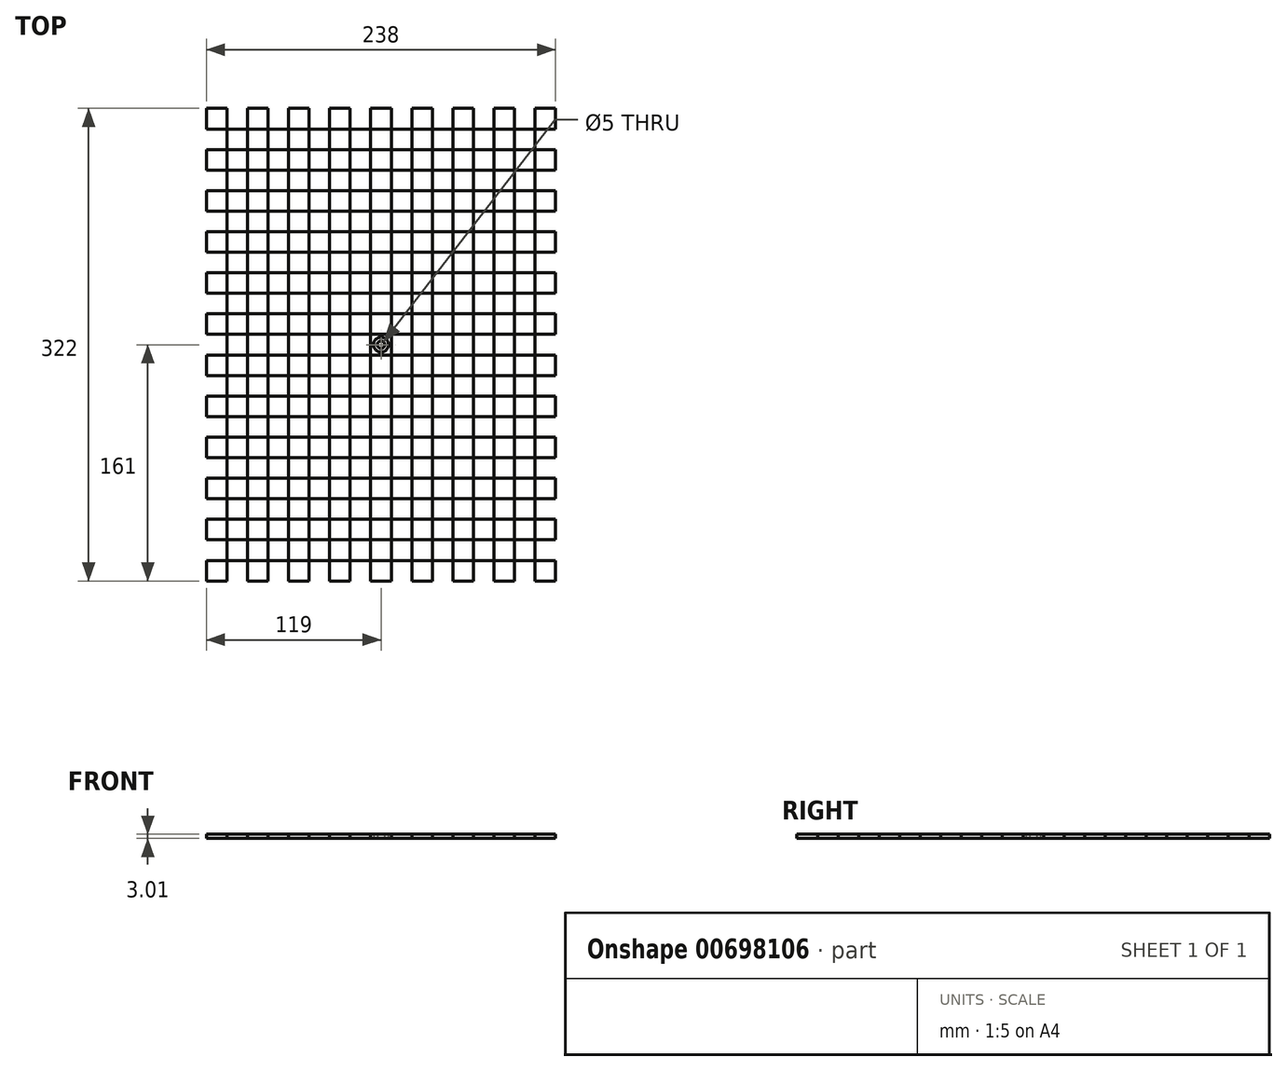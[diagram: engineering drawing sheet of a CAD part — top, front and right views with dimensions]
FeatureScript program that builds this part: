
annotation { "Feature Type Name" : "Feature", "Feature Type Description" : "" }
export const myFeature = defineFeature(function(context is Context, id is Id, definition is map)
    precondition{}
    {
        {
            var Q0;
            Q0=qCreatedBy(makeId("Top.planeOp"),FACE);
            var sketch = newSketch(context, id + "F0", { "sketchPlane" : qUnion([Q0])});
            skLineSegment(sketch, "E0.bottom", {"start": v(145.7, -177.6) * mm, "end": v(-139.3, -177.6) * mm});
            skLineSegment(sketch, "E0.top", {"start": v(145.7, 189.9) * mm, "end": v(-139.3, 189.9) * mm});
            skLineSegment(sketch, "E0.left", {"start": v(145.7, -177.6) * mm, "end": v(145.7, 189.9) * mm});
            skLineSegment(sketch, "E0.right", {"start": v(-139.3, -177.6) * mm, "end": v(-139.3, 189.9) * mm});
            skSolve(sketch);
        }
        {
            var Q0;
            Q0=qCreatedBy(makeId("Top.planeOp"),FACE);
            var sketch = newSketch(context, id + "F1", { "sketchPlane" : qUnion([Q0])});
            skLineSegment(sketch, "E1.bottom", {"start": v(-115.8, -155.6) * mm, "end": v(-101.8, -155.6) * mm});
            skLineSegment(sketch, "E1.top", {"start": v(-115.8, -141.6) * mm, "end": v(-101.8, -141.6) * mm});
            skLineSegment(sketch, "E1.left", {"start": v(-115.8, -155.6) * mm, "end": v(-115.8, -141.6) * mm});
            skLineSegment(sketch, "E1.right", {"start": v(-101.8, -155.6) * mm, "end": v(-101.8, -141.6) * mm});
            skLineSegment(sketch, "E2.direction1", {"start": v(-115.8, -155.6) * mm, "end": v(-87.8, -155.6) * mm, "construction": true});
            skLineSegment(sketch, "E2.direction2", {"start": v(-115.8, -155.6) * mm, "end": v(-115.8, -127.6) * mm, "construction": true});
            skLineSegment(sketch, "E3.bottom", {"start": v(94.2, -127.6) * mm, "end": v(108.2, -127.6) * mm});
            skLineSegment(sketch, "E3.top", {"start": v(94.2, -141.6) * mm, "end": v(108.2, -141.6) * mm});
            skLineSegment(sketch, "E3.left", {"start": v(94.2, -127.6) * mm, "end": v(94.2, -141.6) * mm});
            skLineSegment(sketch, "E3.right", {"start": v(108.2, -127.6) * mm, "end": v(108.2, -141.6) * mm});
            skLineSegment(sketch, "E4.direction1", {"start": v(94.2, -141.6) * mm, "end": v(66.2, -141.6) * mm, "construction": true});
            skLineSegment(sketch, "E4.direction2", {"start": v(94.2, -141.6) * mm, "end": v(94.2, -113.6) * mm, "construction": true});
            skLineSegment(sketch, "E5.0.1.0", {"start": v(-87.8, -155.6) * mm, "end": v(-73.8, -155.6) * mm});
            skLineSegment(sketch, "E5.3.1.0", {"start": v(-87.8, -141.6) * mm, "end": v(-73.8, -141.6) * mm});
            skLineSegment(sketch, "E5.6.1.0", {"start": v(-87.8, -155.6) * mm, "end": v(-87.8, -141.6) * mm});
            skLineSegment(sketch, "E5.9.1.0", {"start": v(-73.8, -155.6) * mm, "end": v(-73.8, -141.6) * mm});
            skLineSegment(sketch, "E5.0.2.0", {"start": v(-59.8, -155.6) * mm, "end": v(-45.8, -155.6) * mm});
            skLineSegment(sketch, "E5.3.2.0", {"start": v(-59.8, -141.6) * mm, "end": v(-45.8, -141.6) * mm});
            skLineSegment(sketch, "E5.6.2.0", {"start": v(-59.8, -155.6) * mm, "end": v(-59.8, -141.6) * mm});
            skLineSegment(sketch, "E5.9.2.0", {"start": v(-45.8, -155.6) * mm, "end": v(-45.8, -141.6) * mm});
            skLineSegment(sketch, "E5.0.3.0", {"start": v(-31.8, -155.6) * mm, "end": v(-17.8, -155.6) * mm});
            skLineSegment(sketch, "E5.3.3.0", {"start": v(-31.8, -141.6) * mm, "end": v(-17.8, -141.6) * mm});
            skLineSegment(sketch, "E5.6.3.0", {"start": v(-31.8, -155.6) * mm, "end": v(-31.8, -141.6) * mm});
            skLineSegment(sketch, "E5.9.3.0", {"start": v(-17.8, -155.6) * mm, "end": v(-17.8, -141.6) * mm});
            skLineSegment(sketch, "E5.0.4.0", {"start": v(-3.8, -155.6) * mm, "end": v(10.2, -155.6) * mm});
            skLineSegment(sketch, "E5.3.4.0", {"start": v(-3.8, -141.6) * mm, "end": v(10.2, -141.6) * mm});
            skLineSegment(sketch, "E5.6.4.0", {"start": v(-3.8, -155.6) * mm, "end": v(-3.8, -141.6) * mm});
            skLineSegment(sketch, "E5.9.4.0", {"start": v(10.2, -155.6) * mm, "end": v(10.2, -141.6) * mm});
            skLineSegment(sketch, "E5.0.5.0", {"start": v(24.2, -155.6) * mm, "end": v(38.2, -155.6) * mm});
            skLineSegment(sketch, "E5.3.5.0", {"start": v(24.2, -141.6) * mm, "end": v(38.2, -141.6) * mm});
            skLineSegment(sketch, "E5.6.5.0", {"start": v(24.2, -155.6) * mm, "end": v(24.2, -141.6) * mm});
            skLineSegment(sketch, "E5.9.5.0", {"start": v(38.2, -155.6) * mm, "end": v(38.2, -141.6) * mm});
            skLineSegment(sketch, "E5.0.6.0", {"start": v(52.2, -155.6) * mm, "end": v(66.2, -155.6) * mm});
            skLineSegment(sketch, "E5.3.6.0", {"start": v(52.2, -141.6) * mm, "end": v(66.2, -141.6) * mm});
            skLineSegment(sketch, "E5.6.6.0", {"start": v(52.2, -155.6) * mm, "end": v(52.2, -141.6) * mm});
            skLineSegment(sketch, "E5.9.6.0", {"start": v(66.2, -155.6) * mm, "end": v(66.2, -141.6) * mm});
            skLineSegment(sketch, "E5.0.7.0", {"start": v(80.2, -155.6) * mm, "end": v(94.2, -155.6) * mm});
            skLineSegment(sketch, "E5.3.7.0", {"start": v(80.2, -141.6) * mm, "end": v(94.2, -141.6) * mm});
            skLineSegment(sketch, "E5.6.7.0", {"start": v(80.2, -155.6) * mm, "end": v(80.2, -141.6) * mm});
            skLineSegment(sketch, "E5.9.7.0", {"start": v(94.2, -155.6) * mm, "end": v(94.2, -141.6) * mm});
            skLineSegment(sketch, "E5.0.8.0", {"start": v(108.2, -155.6) * mm, "end": v(122.2, -155.6) * mm});
            skLineSegment(sketch, "E5.3.8.0", {"start": v(108.2, -141.6) * mm, "end": v(122.2, -141.6) * mm});
            skLineSegment(sketch, "E5.6.8.0", {"start": v(108.2, -155.6) * mm, "end": v(108.2, -141.6) * mm});
            skLineSegment(sketch, "E5.9.8.0", {"start": v(122.2, -155.6) * mm, "end": v(122.2, -141.6) * mm});
            skLineSegment(sketch, "E6.0.0.1", {"start": v(-115.8, -127.6) * mm, "end": v(-101.8, -127.6) * mm});
            skLineSegment(sketch, "E6.3.0.1", {"start": v(-115.8, -113.6) * mm, "end": v(-101.8, -113.6) * mm});
            skLineSegment(sketch, "E6.6.0.1", {"start": v(-115.8, -127.6) * mm, "end": v(-115.8, -113.6) * mm});
            skLineSegment(sketch, "E6.9.0.1", {"start": v(-101.8, -127.6) * mm, "end": v(-101.8, -113.6) * mm});
            skLineSegment(sketch, "E6.0.0.2", {"start": v(-115.8, -99.6) * mm, "end": v(-101.8, -99.6) * mm});
            skLineSegment(sketch, "E6.3.0.2", {"start": v(-115.8, -85.6) * mm, "end": v(-101.8, -85.6) * mm});
            skLineSegment(sketch, "E6.6.0.2", {"start": v(-115.8, -99.6) * mm, "end": v(-115.8, -85.6) * mm});
            skLineSegment(sketch, "E6.9.0.2", {"start": v(-101.8, -99.6) * mm, "end": v(-101.8, -85.6) * mm});
            skLineSegment(sketch, "E6.0.0.3", {"start": v(-115.8, -71.6) * mm, "end": v(-101.8, -71.6) * mm});
            skLineSegment(sketch, "E6.3.0.3", {"start": v(-115.8, -57.6) * mm, "end": v(-101.8, -57.6) * mm});
            skLineSegment(sketch, "E6.6.0.3", {"start": v(-115.8, -71.6) * mm, "end": v(-115.8, -57.6) * mm});
            skLineSegment(sketch, "E6.9.0.3", {"start": v(-101.8, -71.6) * mm, "end": v(-101.8, -57.6) * mm});
            skLineSegment(sketch, "E6.0.0.4", {"start": v(-115.8, -43.6) * mm, "end": v(-101.8, -43.6) * mm});
            skLineSegment(sketch, "E6.3.0.4", {"start": v(-115.8, -29.6) * mm, "end": v(-101.8, -29.6) * mm});
            skLineSegment(sketch, "E6.6.0.4", {"start": v(-115.8, -43.6) * mm, "end": v(-115.8, -29.6) * mm});
            skLineSegment(sketch, "E6.9.0.4", {"start": v(-101.8, -43.6) * mm, "end": v(-101.8, -29.6) * mm});
            skLineSegment(sketch, "E6.0.0.5", {"start": v(-115.8, -15.6) * mm, "end": v(-101.8, -15.6) * mm});
            skLineSegment(sketch, "E6.3.0.5", {"start": v(-115.8, -1.6) * mm, "end": v(-101.8, -1.6) * mm});
            skLineSegment(sketch, "E6.6.0.5", {"start": v(-115.8, -15.6) * mm, "end": v(-115.8, -1.6) * mm});
            skLineSegment(sketch, "E6.9.0.5", {"start": v(-101.8, -15.6) * mm, "end": v(-101.8, -1.6) * mm});
            skLineSegment(sketch, "E6.0.0.6", {"start": v(-115.8, 12.4) * mm, "end": v(-101.8, 12.4) * mm});
            skLineSegment(sketch, "E6.3.0.6", {"start": v(-115.8, 26.4) * mm, "end": v(-101.8, 26.4) * mm});
            skLineSegment(sketch, "E6.6.0.6", {"start": v(-115.8, 12.4) * mm, "end": v(-115.8, 26.4) * mm});
            skLineSegment(sketch, "E6.9.0.6", {"start": v(-101.8, 12.4) * mm, "end": v(-101.8, 26.4) * mm});
            skLineSegment(sketch, "E6.0.0.7", {"start": v(-115.8, 40.4) * mm, "end": v(-101.8, 40.4) * mm});
            skLineSegment(sketch, "E6.3.0.7", {"start": v(-115.8, 54.4) * mm, "end": v(-101.8, 54.4) * mm});
            skLineSegment(sketch, "E6.6.0.7", {"start": v(-115.8, 40.4) * mm, "end": v(-115.8, 54.4) * mm});
            skLineSegment(sketch, "E6.9.0.7", {"start": v(-101.8, 40.4) * mm, "end": v(-101.8, 54.4) * mm});
            skLineSegment(sketch, "E6.0.0.8", {"start": v(-115.8, 68.4) * mm, "end": v(-101.8, 68.4) * mm});
            skLineSegment(sketch, "E6.3.0.8", {"start": v(-115.8, 82.4) * mm, "end": v(-101.8, 82.4) * mm});
            skLineSegment(sketch, "E6.6.0.8", {"start": v(-115.8, 68.4) * mm, "end": v(-115.8, 82.4) * mm});
            skLineSegment(sketch, "E6.9.0.8", {"start": v(-101.8, 68.4) * mm, "end": v(-101.8, 82.4) * mm});
            skLineSegment(sketch, "E6.0.0.9", {"start": v(-115.8, 96.4) * mm, "end": v(-101.8, 96.4) * mm});
            skLineSegment(sketch, "E6.3.0.9", {"start": v(-115.8, 110.4) * mm, "end": v(-101.8, 110.4) * mm});
            skLineSegment(sketch, "E6.6.0.9", {"start": v(-115.8, 96.4) * mm, "end": v(-115.8, 110.4) * mm});
            skLineSegment(sketch, "E6.9.0.9", {"start": v(-101.8, 96.4) * mm, "end": v(-101.8, 110.4) * mm});
            skLineSegment(sketch, "E6.0.0.10", {"start": v(-115.8, 124.4) * mm, "end": v(-101.8, 124.4) * mm});
            skLineSegment(sketch, "E6.3.0.10", {"start": v(-115.8, 138.4) * mm, "end": v(-101.8, 138.4) * mm});
            skLineSegment(sketch, "E6.6.0.10", {"start": v(-115.8, 124.4) * mm, "end": v(-115.8, 138.4) * mm});
            skLineSegment(sketch, "E6.9.0.10", {"start": v(-101.8, 124.4) * mm, "end": v(-101.8, 138.4) * mm});
            skLineSegment(sketch, "E6.0.0.11", {"start": v(-115.8, 152.4) * mm, "end": v(-101.8, 152.4) * mm});
            skLineSegment(sketch, "E6.3.0.11", {"start": v(-115.8, 166.4) * mm, "end": v(-101.8, 166.4) * mm});
            skLineSegment(sketch, "E6.6.0.11", {"start": v(-115.8, 152.4) * mm, "end": v(-115.8, 166.4) * mm});
            skLineSegment(sketch, "E6.9.0.11", {"start": v(-101.8, 152.4) * mm, "end": v(-101.8, 166.4) * mm});
            skLineSegment(sketch, "E6.0.1.1", {"start": v(-87.8, -127.6) * mm, "end": v(-73.8, -127.6) * mm});
            skLineSegment(sketch, "E6.3.1.1", {"start": v(-87.8, -113.6) * mm, "end": v(-73.8, -113.6) * mm});
            skLineSegment(sketch, "E6.6.1.1", {"start": v(-87.8, -127.6) * mm, "end": v(-87.8, -113.6) * mm});
            skLineSegment(sketch, "E6.9.1.1", {"start": v(-73.8, -127.6) * mm, "end": v(-73.8, -113.6) * mm});
            skLineSegment(sketch, "E6.0.1.2", {"start": v(-87.8, -99.6) * mm, "end": v(-73.8, -99.6) * mm});
            skLineSegment(sketch, "E6.3.1.2", {"start": v(-87.8, -85.6) * mm, "end": v(-73.8, -85.6) * mm});
            skLineSegment(sketch, "E6.6.1.2", {"start": v(-87.8, -99.6) * mm, "end": v(-87.8, -85.6) * mm});
            skLineSegment(sketch, "E6.9.1.2", {"start": v(-73.8, -99.6) * mm, "end": v(-73.8, -85.6) * mm});
            skLineSegment(sketch, "E6.0.1.3", {"start": v(-87.8, -71.6) * mm, "end": v(-73.8, -71.6) * mm});
            skLineSegment(sketch, "E6.3.1.3", {"start": v(-87.8, -57.6) * mm, "end": v(-73.8, -57.6) * mm});
            skLineSegment(sketch, "E6.6.1.3", {"start": v(-87.8, -71.6) * mm, "end": v(-87.8, -57.6) * mm});
            skLineSegment(sketch, "E6.9.1.3", {"start": v(-73.8, -71.6) * mm, "end": v(-73.8, -57.6) * mm});
            skLineSegment(sketch, "E6.0.1.4", {"start": v(-87.8, -43.6) * mm, "end": v(-73.8, -43.6) * mm});
            skLineSegment(sketch, "E6.3.1.4", {"start": v(-87.8, -29.6) * mm, "end": v(-73.8, -29.6) * mm});
            skLineSegment(sketch, "E6.6.1.4", {"start": v(-87.8, -43.6) * mm, "end": v(-87.8, -29.6) * mm});
            skLineSegment(sketch, "E6.9.1.4", {"start": v(-73.8, -43.6) * mm, "end": v(-73.8, -29.6) * mm});
            skLineSegment(sketch, "E6.0.1.5", {"start": v(-87.8, -15.6) * mm, "end": v(-73.8, -15.6) * mm});
            skLineSegment(sketch, "E6.3.1.5", {"start": v(-87.8, -1.6) * mm, "end": v(-73.8, -1.6) * mm});
            skLineSegment(sketch, "E6.6.1.5", {"start": v(-87.8, -15.6) * mm, "end": v(-87.8, -1.6) * mm});
            skLineSegment(sketch, "E6.9.1.5", {"start": v(-73.8, -15.6) * mm, "end": v(-73.8, -1.6) * mm});
            skLineSegment(sketch, "E6.0.1.6", {"start": v(-87.8, 12.4) * mm, "end": v(-73.8, 12.4) * mm});
            skLineSegment(sketch, "E6.3.1.6", {"start": v(-87.8, 26.4) * mm, "end": v(-73.8, 26.4) * mm});
            skLineSegment(sketch, "E6.6.1.6", {"start": v(-87.8, 12.4) * mm, "end": v(-87.8, 26.4) * mm});
            skLineSegment(sketch, "E6.9.1.6", {"start": v(-73.8, 12.4) * mm, "end": v(-73.8, 26.4) * mm});
            skLineSegment(sketch, "E6.0.1.7", {"start": v(-87.8, 40.4) * mm, "end": v(-73.8, 40.4) * mm});
            skLineSegment(sketch, "E6.3.1.7", {"start": v(-87.8, 54.4) * mm, "end": v(-73.8, 54.4) * mm});
            skLineSegment(sketch, "E6.6.1.7", {"start": v(-87.8, 40.4) * mm, "end": v(-87.8, 54.4) * mm});
            skLineSegment(sketch, "E6.9.1.7", {"start": v(-73.8, 40.4) * mm, "end": v(-73.8, 54.4) * mm});
            skLineSegment(sketch, "E6.0.1.8", {"start": v(-87.8, 68.4) * mm, "end": v(-73.8, 68.4) * mm});
            skLineSegment(sketch, "E6.3.1.8", {"start": v(-87.8, 82.4) * mm, "end": v(-73.8, 82.4) * mm});
            skLineSegment(sketch, "E6.6.1.8", {"start": v(-87.8, 68.4) * mm, "end": v(-87.8, 82.4) * mm});
            skLineSegment(sketch, "E6.9.1.8", {"start": v(-73.8, 68.4) * mm, "end": v(-73.8, 82.4) * mm});
            skLineSegment(sketch, "E6.0.1.9", {"start": v(-87.8, 96.4) * mm, "end": v(-73.8, 96.4) * mm});
            skLineSegment(sketch, "E6.3.1.9", {"start": v(-87.8, 110.4) * mm, "end": v(-73.8, 110.4) * mm});
            skLineSegment(sketch, "E6.6.1.9", {"start": v(-87.8, 96.4) * mm, "end": v(-87.8, 110.4) * mm});
            skLineSegment(sketch, "E6.9.1.9", {"start": v(-73.8, 96.4) * mm, "end": v(-73.8, 110.4) * mm});
            skLineSegment(sketch, "E6.0.1.10", {"start": v(-87.8, 124.4) * mm, "end": v(-73.8, 124.4) * mm});
            skLineSegment(sketch, "E6.3.1.10", {"start": v(-87.8, 138.4) * mm, "end": v(-73.8, 138.4) * mm});
            skLineSegment(sketch, "E6.6.1.10", {"start": v(-87.8, 124.4) * mm, "end": v(-87.8, 138.4) * mm});
            skLineSegment(sketch, "E6.9.1.10", {"start": v(-73.8, 124.4) * mm, "end": v(-73.8, 138.4) * mm});
            skLineSegment(sketch, "E6.0.1.11", {"start": v(-87.8, 152.4) * mm, "end": v(-73.8, 152.4) * mm});
            skLineSegment(sketch, "E6.3.1.11", {"start": v(-87.8, 166.4) * mm, "end": v(-73.8, 166.4) * mm});
            skLineSegment(sketch, "E6.6.1.11", {"start": v(-87.8, 152.4) * mm, "end": v(-87.8, 166.4) * mm});
            skLineSegment(sketch, "E6.9.1.11", {"start": v(-73.8, 152.4) * mm, "end": v(-73.8, 166.4) * mm});
            skLineSegment(sketch, "E6.0.2.1", {"start": v(-59.8, -127.6) * mm, "end": v(-45.8, -127.6) * mm});
            skLineSegment(sketch, "E6.3.2.1", {"start": v(-59.8, -113.6) * mm, "end": v(-45.8, -113.6) * mm});
            skLineSegment(sketch, "E6.6.2.1", {"start": v(-59.8, -127.6) * mm, "end": v(-59.8, -113.6) * mm});
            skLineSegment(sketch, "E6.9.2.1", {"start": v(-45.8, -127.6) * mm, "end": v(-45.8, -113.6) * mm});
            skLineSegment(sketch, "E6.0.2.2", {"start": v(-59.8, -99.6) * mm, "end": v(-45.8, -99.6) * mm});
            skLineSegment(sketch, "E6.3.2.2", {"start": v(-59.8, -85.6) * mm, "end": v(-45.8, -85.6) * mm});
            skLineSegment(sketch, "E6.6.2.2", {"start": v(-59.8, -99.6) * mm, "end": v(-59.8, -85.6) * mm});
            skLineSegment(sketch, "E6.9.2.2", {"start": v(-45.8, -99.6) * mm, "end": v(-45.8, -85.6) * mm});
            skLineSegment(sketch, "E6.0.2.3", {"start": v(-59.8, -71.6) * mm, "end": v(-45.8, -71.6) * mm});
            skLineSegment(sketch, "E6.3.2.3", {"start": v(-59.8, -57.6) * mm, "end": v(-45.8, -57.6) * mm});
            skLineSegment(sketch, "E6.6.2.3", {"start": v(-59.8, -71.6) * mm, "end": v(-59.8, -57.6) * mm});
            skLineSegment(sketch, "E6.9.2.3", {"start": v(-45.8, -71.6) * mm, "end": v(-45.8, -57.6) * mm});
            skLineSegment(sketch, "E6.0.2.4", {"start": v(-59.8, -43.6) * mm, "end": v(-45.8, -43.6) * mm});
            skLineSegment(sketch, "E6.3.2.4", {"start": v(-59.8, -29.6) * mm, "end": v(-45.8, -29.6) * mm});
            skLineSegment(sketch, "E6.6.2.4", {"start": v(-59.8, -43.6) * mm, "end": v(-59.8, -29.6) * mm});
            skLineSegment(sketch, "E6.9.2.4", {"start": v(-45.8, -43.6) * mm, "end": v(-45.8, -29.6) * mm});
            skLineSegment(sketch, "E6.0.2.5", {"start": v(-59.8, -15.6) * mm, "end": v(-45.8, -15.6) * mm});
            skLineSegment(sketch, "E6.3.2.5", {"start": v(-59.8, -1.6) * mm, "end": v(-45.8, -1.6) * mm});
            skLineSegment(sketch, "E6.6.2.5", {"start": v(-59.8, -15.6) * mm, "end": v(-59.8, -1.6) * mm});
            skLineSegment(sketch, "E6.9.2.5", {"start": v(-45.8, -15.6) * mm, "end": v(-45.8, -1.6) * mm});
            skLineSegment(sketch, "E6.0.2.6", {"start": v(-59.8, 12.4) * mm, "end": v(-45.8, 12.4) * mm});
            skLineSegment(sketch, "E6.3.2.6", {"start": v(-59.8, 26.4) * mm, "end": v(-45.8, 26.4) * mm});
            skLineSegment(sketch, "E6.6.2.6", {"start": v(-59.8, 12.4) * mm, "end": v(-59.8, 26.4) * mm});
            skLineSegment(sketch, "E6.9.2.6", {"start": v(-45.8, 12.4) * mm, "end": v(-45.8, 26.4) * mm});
            skLineSegment(sketch, "E6.0.2.7", {"start": v(-59.8, 40.4) * mm, "end": v(-45.8, 40.4) * mm});
            skLineSegment(sketch, "E6.3.2.7", {"start": v(-59.8, 54.4) * mm, "end": v(-45.8, 54.4) * mm});
            skLineSegment(sketch, "E6.6.2.7", {"start": v(-59.8, 40.4) * mm, "end": v(-59.8, 54.4) * mm});
            skLineSegment(sketch, "E6.9.2.7", {"start": v(-45.8, 40.4) * mm, "end": v(-45.8, 54.4) * mm});
            skLineSegment(sketch, "E6.0.2.8", {"start": v(-59.8, 68.4) * mm, "end": v(-45.8, 68.4) * mm});
            skLineSegment(sketch, "E6.3.2.8", {"start": v(-59.8, 82.4) * mm, "end": v(-45.8, 82.4) * mm});
            skLineSegment(sketch, "E6.6.2.8", {"start": v(-59.8, 68.4) * mm, "end": v(-59.8, 82.4) * mm});
            skLineSegment(sketch, "E6.9.2.8", {"start": v(-45.8, 68.4) * mm, "end": v(-45.8, 82.4) * mm});
            skLineSegment(sketch, "E6.0.2.9", {"start": v(-59.8, 96.4) * mm, "end": v(-45.8, 96.4) * mm});
            skLineSegment(sketch, "E6.3.2.9", {"start": v(-59.8, 110.4) * mm, "end": v(-45.8, 110.4) * mm});
            skLineSegment(sketch, "E6.6.2.9", {"start": v(-59.8, 96.4) * mm, "end": v(-59.8, 110.4) * mm});
            skLineSegment(sketch, "E6.9.2.9", {"start": v(-45.8, 96.4) * mm, "end": v(-45.8, 110.4) * mm});
            skLineSegment(sketch, "E6.0.2.10", {"start": v(-59.8, 124.4) * mm, "end": v(-45.8, 124.4) * mm});
            skLineSegment(sketch, "E6.3.2.10", {"start": v(-59.8, 138.4) * mm, "end": v(-45.8, 138.4) * mm});
            skLineSegment(sketch, "E6.6.2.10", {"start": v(-59.8, 124.4) * mm, "end": v(-59.8, 138.4) * mm});
            skLineSegment(sketch, "E6.9.2.10", {"start": v(-45.8, 124.4) * mm, "end": v(-45.8, 138.4) * mm});
            skLineSegment(sketch, "E6.0.2.11", {"start": v(-59.8, 152.4) * mm, "end": v(-45.8, 152.4) * mm});
            skLineSegment(sketch, "E6.3.2.11", {"start": v(-59.8, 166.4) * mm, "end": v(-45.8, 166.4) * mm});
            skLineSegment(sketch, "E6.6.2.11", {"start": v(-59.8, 152.4) * mm, "end": v(-59.8, 166.4) * mm});
            skLineSegment(sketch, "E6.9.2.11", {"start": v(-45.8, 152.4) * mm, "end": v(-45.8, 166.4) * mm});
            skLineSegment(sketch, "E6.0.3.1", {"start": v(-31.8, -127.6) * mm, "end": v(-17.8, -127.6) * mm});
            skLineSegment(sketch, "E6.3.3.1", {"start": v(-31.8, -113.6) * mm, "end": v(-17.8, -113.6) * mm});
            skLineSegment(sketch, "E6.6.3.1", {"start": v(-31.8, -127.6) * mm, "end": v(-31.8, -113.6) * mm});
            skLineSegment(sketch, "E6.9.3.1", {"start": v(-17.8, -127.6) * mm, "end": v(-17.8, -113.6) * mm});
            skLineSegment(sketch, "E6.0.3.2", {"start": v(-31.8, -99.6) * mm, "end": v(-17.8, -99.6) * mm});
            skLineSegment(sketch, "E6.3.3.2", {"start": v(-31.8, -85.6) * mm, "end": v(-17.8, -85.6) * mm});
            skLineSegment(sketch, "E6.6.3.2", {"start": v(-31.8, -99.6) * mm, "end": v(-31.8, -85.6) * mm});
            skLineSegment(sketch, "E6.9.3.2", {"start": v(-17.8, -99.6) * mm, "end": v(-17.8, -85.6) * mm});
            skLineSegment(sketch, "E6.0.3.3", {"start": v(-31.8, -71.6) * mm, "end": v(-17.8, -71.6) * mm});
            skLineSegment(sketch, "E6.3.3.3", {"start": v(-31.8, -57.6) * mm, "end": v(-17.8, -57.6) * mm});
            skLineSegment(sketch, "E6.6.3.3", {"start": v(-31.8, -71.6) * mm, "end": v(-31.8, -57.6) * mm});
            skLineSegment(sketch, "E6.9.3.3", {"start": v(-17.8, -71.6) * mm, "end": v(-17.8, -57.6) * mm});
            skLineSegment(sketch, "E6.0.3.4", {"start": v(-31.8, -43.6) * mm, "end": v(-17.8, -43.6) * mm});
            skLineSegment(sketch, "E6.3.3.4", {"start": v(-31.8, -29.6) * mm, "end": v(-17.8, -29.6) * mm});
            skLineSegment(sketch, "E6.6.3.4", {"start": v(-31.8, -43.6) * mm, "end": v(-31.8, -29.6) * mm});
            skLineSegment(sketch, "E6.9.3.4", {"start": v(-17.8, -43.6) * mm, "end": v(-17.8, -29.6) * mm});
            skLineSegment(sketch, "E6.0.3.5", {"start": v(-31.8, -15.6) * mm, "end": v(-17.8, -15.6) * mm});
            skLineSegment(sketch, "E6.3.3.5", {"start": v(-31.8, -1.6) * mm, "end": v(-17.8, -1.6) * mm});
            skLineSegment(sketch, "E6.6.3.5", {"start": v(-31.8, -15.6) * mm, "end": v(-31.8, -1.6) * mm});
            skLineSegment(sketch, "E6.9.3.5", {"start": v(-17.8, -15.6) * mm, "end": v(-17.8, -1.6) * mm});
            skLineSegment(sketch, "E6.0.3.6", {"start": v(-31.8, 12.4) * mm, "end": v(-17.8, 12.4) * mm});
            skLineSegment(sketch, "E6.3.3.6", {"start": v(-31.8, 26.4) * mm, "end": v(-17.8, 26.4) * mm});
            skLineSegment(sketch, "E6.6.3.6", {"start": v(-31.8, 12.4) * mm, "end": v(-31.8, 26.4) * mm});
            skLineSegment(sketch, "E6.9.3.6", {"start": v(-17.8, 12.4) * mm, "end": v(-17.8, 26.4) * mm});
            skLineSegment(sketch, "E6.0.3.7", {"start": v(-31.8, 40.4) * mm, "end": v(-17.8, 40.4) * mm});
            skLineSegment(sketch, "E6.3.3.7", {"start": v(-31.8, 54.4) * mm, "end": v(-17.8, 54.4) * mm});
            skLineSegment(sketch, "E6.6.3.7", {"start": v(-31.8, 40.4) * mm, "end": v(-31.8, 54.4) * mm});
            skLineSegment(sketch, "E6.9.3.7", {"start": v(-17.8, 40.4) * mm, "end": v(-17.8, 54.4) * mm});
            skLineSegment(sketch, "E6.0.3.8", {"start": v(-31.8, 68.4) * mm, "end": v(-17.8, 68.4) * mm});
            skLineSegment(sketch, "E6.3.3.8", {"start": v(-31.8, 82.4) * mm, "end": v(-17.8, 82.4) * mm});
            skLineSegment(sketch, "E6.6.3.8", {"start": v(-31.8, 68.4) * mm, "end": v(-31.8, 82.4) * mm});
            skLineSegment(sketch, "E6.9.3.8", {"start": v(-17.8, 68.4) * mm, "end": v(-17.8, 82.4) * mm});
            skLineSegment(sketch, "E6.0.3.9", {"start": v(-31.8, 96.4) * mm, "end": v(-17.8, 96.4) * mm});
            skLineSegment(sketch, "E6.3.3.9", {"start": v(-31.8, 110.4) * mm, "end": v(-17.8, 110.4) * mm});
            skLineSegment(sketch, "E6.6.3.9", {"start": v(-31.8, 96.4) * mm, "end": v(-31.8, 110.4) * mm});
            skLineSegment(sketch, "E6.9.3.9", {"start": v(-17.8, 96.4) * mm, "end": v(-17.8, 110.4) * mm});
            skLineSegment(sketch, "E6.0.3.10", {"start": v(-31.8, 124.4) * mm, "end": v(-17.8, 124.4) * mm});
            skLineSegment(sketch, "E6.3.3.10", {"start": v(-31.8, 138.4) * mm, "end": v(-17.8, 138.4) * mm});
            skLineSegment(sketch, "E6.6.3.10", {"start": v(-31.8, 124.4) * mm, "end": v(-31.8, 138.4) * mm});
            skLineSegment(sketch, "E6.9.3.10", {"start": v(-17.8, 124.4) * mm, "end": v(-17.8, 138.4) * mm});
            skLineSegment(sketch, "E6.0.3.11", {"start": v(-31.8, 152.4) * mm, "end": v(-17.8, 152.4) * mm});
            skLineSegment(sketch, "E6.3.3.11", {"start": v(-31.8, 166.4) * mm, "end": v(-17.8, 166.4) * mm});
            skLineSegment(sketch, "E6.6.3.11", {"start": v(-31.8, 152.4) * mm, "end": v(-31.8, 166.4) * mm});
            skLineSegment(sketch, "E6.9.3.11", {"start": v(-17.8, 152.4) * mm, "end": v(-17.8, 166.4) * mm});
            skLineSegment(sketch, "E6.0.4.1", {"start": v(-3.8, -127.6) * mm, "end": v(10.2, -127.6) * mm});
            skLineSegment(sketch, "E6.3.4.1", {"start": v(-3.8, -113.6) * mm, "end": v(10.2, -113.6) * mm});
            skLineSegment(sketch, "E6.6.4.1", {"start": v(-3.8, -127.6) * mm, "end": v(-3.8, -113.6) * mm});
            skLineSegment(sketch, "E6.9.4.1", {"start": v(10.2, -127.6) * mm, "end": v(10.2, -113.6) * mm});
            skLineSegment(sketch, "E6.0.4.2", {"start": v(-3.8, -99.6) * mm, "end": v(10.2, -99.6) * mm});
            skLineSegment(sketch, "E6.3.4.2", {"start": v(-3.8, -85.6) * mm, "end": v(10.2, -85.6) * mm});
            skLineSegment(sketch, "E6.6.4.2", {"start": v(-3.8, -99.6) * mm, "end": v(-3.8, -85.6) * mm});
            skLineSegment(sketch, "E6.9.4.2", {"start": v(10.2, -99.6) * mm, "end": v(10.2, -85.6) * mm});
            skLineSegment(sketch, "E6.0.4.3", {"start": v(-3.8, -71.6) * mm, "end": v(10.2, -71.6) * mm});
            skLineSegment(sketch, "E6.3.4.3", {"start": v(-3.8, -57.6) * mm, "end": v(10.2, -57.6) * mm});
            skLineSegment(sketch, "E6.6.4.3", {"start": v(-3.8, -71.6) * mm, "end": v(-3.8, -57.6) * mm});
            skLineSegment(sketch, "E6.9.4.3", {"start": v(10.2, -71.6) * mm, "end": v(10.2, -57.6) * mm});
            skLineSegment(sketch, "E6.0.4.4", {"start": v(-3.8, -43.6) * mm, "end": v(10.2, -43.6) * mm});
            skLineSegment(sketch, "E6.3.4.4", {"start": v(-3.8, -29.6) * mm, "end": v(10.2, -29.6) * mm});
            skLineSegment(sketch, "E6.6.4.4", {"start": v(-3.8, -43.6) * mm, "end": v(-3.8, -29.6) * mm});
            skLineSegment(sketch, "E6.9.4.4", {"start": v(10.2, -43.6) * mm, "end": v(10.2, -29.6) * mm});
            skLineSegment(sketch, "E6.0.4.5", {"start": v(-3.8, -15.6) * mm, "end": v(10.2, -15.6) * mm});
            skLineSegment(sketch, "E6.3.4.5", {"start": v(-3.8, -1.6) * mm, "end": v(10.2, -1.6) * mm});
            skLineSegment(sketch, "E6.6.4.5", {"start": v(-3.8, -15.6) * mm, "end": v(-3.8, -1.6) * mm});
            skLineSegment(sketch, "E6.9.4.5", {"start": v(10.2, -15.6) * mm, "end": v(10.2, -1.6) * mm});
            skLineSegment(sketch, "E6.0.4.6", {"start": v(-3.8, 12.4) * mm, "end": v(10.2, 12.4) * mm});
            skLineSegment(sketch, "E6.3.4.6", {"start": v(-3.8, 26.4) * mm, "end": v(10.2, 26.4) * mm});
            skLineSegment(sketch, "E6.6.4.6", {"start": v(-3.8, 12.4) * mm, "end": v(-3.8, 26.4) * mm});
            skLineSegment(sketch, "E6.9.4.6", {"start": v(10.2, 12.4) * mm, "end": v(10.2, 26.4) * mm});
            skLineSegment(sketch, "E6.0.4.7", {"start": v(-3.8, 40.4) * mm, "end": v(10.2, 40.4) * mm});
            skLineSegment(sketch, "E6.3.4.7", {"start": v(-3.8, 54.4) * mm, "end": v(10.2, 54.4) * mm});
            skLineSegment(sketch, "E6.6.4.7", {"start": v(-3.8, 40.4) * mm, "end": v(-3.8, 54.4) * mm});
            skLineSegment(sketch, "E6.9.4.7", {"start": v(10.2, 40.4) * mm, "end": v(10.2, 54.4) * mm});
            skLineSegment(sketch, "E6.0.4.8", {"start": v(-3.8, 68.4) * mm, "end": v(10.2, 68.4) * mm});
            skLineSegment(sketch, "E6.3.4.8", {"start": v(-3.8, 82.4) * mm, "end": v(10.2, 82.4) * mm});
            skLineSegment(sketch, "E6.6.4.8", {"start": v(-3.8, 68.4) * mm, "end": v(-3.8, 82.4) * mm});
            skLineSegment(sketch, "E6.9.4.8", {"start": v(10.2, 68.4) * mm, "end": v(10.2, 82.4) * mm});
            skLineSegment(sketch, "E6.0.4.9", {"start": v(-3.8, 96.4) * mm, "end": v(10.2, 96.4) * mm});
            skLineSegment(sketch, "E6.3.4.9", {"start": v(-3.8, 110.4) * mm, "end": v(10.2, 110.4) * mm});
            skLineSegment(sketch, "E6.6.4.9", {"start": v(-3.8, 96.4) * mm, "end": v(-3.8, 110.4) * mm});
            skLineSegment(sketch, "E6.9.4.9", {"start": v(10.2, 96.4) * mm, "end": v(10.2, 110.4) * mm});
            skLineSegment(sketch, "E6.0.4.10", {"start": v(-3.8, 124.4) * mm, "end": v(10.2, 124.4) * mm});
            skLineSegment(sketch, "E6.3.4.10", {"start": v(-3.8, 138.4) * mm, "end": v(10.2, 138.4) * mm});
            skLineSegment(sketch, "E6.6.4.10", {"start": v(-3.8, 124.4) * mm, "end": v(-3.8, 138.4) * mm});
            skLineSegment(sketch, "E6.9.4.10", {"start": v(10.2, 124.4) * mm, "end": v(10.2, 138.4) * mm});
            skLineSegment(sketch, "E6.0.4.11", {"start": v(-3.8, 152.4) * mm, "end": v(10.2, 152.4) * mm});
            skLineSegment(sketch, "E6.3.4.11", {"start": v(-3.8, 166.4) * mm, "end": v(10.2, 166.4) * mm});
            skLineSegment(sketch, "E6.6.4.11", {"start": v(-3.8, 152.4) * mm, "end": v(-3.8, 166.4) * mm});
            skLineSegment(sketch, "E6.9.4.11", {"start": v(10.2, 152.4) * mm, "end": v(10.2, 166.4) * mm});
            skLineSegment(sketch, "E6.0.5.1", {"start": v(24.2, -127.6) * mm, "end": v(38.2, -127.6) * mm});
            skLineSegment(sketch, "E6.3.5.1", {"start": v(24.2, -113.6) * mm, "end": v(38.2, -113.6) * mm});
            skLineSegment(sketch, "E6.6.5.1", {"start": v(24.2, -127.6) * mm, "end": v(24.2, -113.6) * mm});
            skLineSegment(sketch, "E6.9.5.1", {"start": v(38.2, -127.6) * mm, "end": v(38.2, -113.6) * mm});
            skLineSegment(sketch, "E6.0.5.2", {"start": v(24.2, -99.6) * mm, "end": v(38.2, -99.6) * mm});
            skLineSegment(sketch, "E6.3.5.2", {"start": v(24.2, -85.6) * mm, "end": v(38.2, -85.6) * mm});
            skLineSegment(sketch, "E6.6.5.2", {"start": v(24.2, -99.6) * mm, "end": v(24.2, -85.6) * mm});
            skLineSegment(sketch, "E6.9.5.2", {"start": v(38.2, -99.6) * mm, "end": v(38.2, -85.6) * mm});
            skLineSegment(sketch, "E6.0.5.3", {"start": v(24.2, -71.6) * mm, "end": v(38.2, -71.6) * mm});
            skLineSegment(sketch, "E6.3.5.3", {"start": v(24.2, -57.6) * mm, "end": v(38.2, -57.6) * mm});
            skLineSegment(sketch, "E6.6.5.3", {"start": v(24.2, -71.6) * mm, "end": v(24.2, -57.6) * mm});
            skLineSegment(sketch, "E6.9.5.3", {"start": v(38.2, -71.6) * mm, "end": v(38.2, -57.6) * mm});
            skLineSegment(sketch, "E6.0.5.4", {"start": v(24.2, -43.6) * mm, "end": v(38.2, -43.6) * mm});
            skLineSegment(sketch, "E6.3.5.4", {"start": v(24.2, -29.6) * mm, "end": v(38.2, -29.6) * mm});
            skLineSegment(sketch, "E6.6.5.4", {"start": v(24.2, -43.6) * mm, "end": v(24.2, -29.6) * mm});
            skLineSegment(sketch, "E6.9.5.4", {"start": v(38.2, -43.6) * mm, "end": v(38.2, -29.6) * mm});
            skLineSegment(sketch, "E6.0.5.5", {"start": v(24.2, -15.6) * mm, "end": v(38.2, -15.6) * mm});
            skLineSegment(sketch, "E6.3.5.5", {"start": v(24.2, -1.6) * mm, "end": v(38.2, -1.6) * mm});
            skLineSegment(sketch, "E6.6.5.5", {"start": v(24.2, -15.6) * mm, "end": v(24.2, -1.6) * mm});
            skLineSegment(sketch, "E6.9.5.5", {"start": v(38.2, -15.6) * mm, "end": v(38.2, -1.6) * mm});
            skLineSegment(sketch, "E6.0.5.6", {"start": v(24.2, 12.4) * mm, "end": v(38.2, 12.4) * mm});
            skLineSegment(sketch, "E6.3.5.6", {"start": v(24.2, 26.4) * mm, "end": v(38.2, 26.4) * mm});
            skLineSegment(sketch, "E6.6.5.6", {"start": v(24.2, 12.4) * mm, "end": v(24.2, 26.4) * mm});
            skLineSegment(sketch, "E6.9.5.6", {"start": v(38.2, 12.4) * mm, "end": v(38.2, 26.4) * mm});
            skLineSegment(sketch, "E6.0.5.7", {"start": v(24.2, 40.4) * mm, "end": v(38.2, 40.4) * mm});
            skLineSegment(sketch, "E6.3.5.7", {"start": v(24.2, 54.4) * mm, "end": v(38.2, 54.4) * mm});
            skLineSegment(sketch, "E6.6.5.7", {"start": v(24.2, 40.4) * mm, "end": v(24.2, 54.4) * mm});
            skLineSegment(sketch, "E6.9.5.7", {"start": v(38.2, 40.4) * mm, "end": v(38.2, 54.4) * mm});
            skLineSegment(sketch, "E6.0.5.8", {"start": v(24.2, 68.4) * mm, "end": v(38.2, 68.4) * mm});
            skLineSegment(sketch, "E6.3.5.8", {"start": v(24.2, 82.4) * mm, "end": v(38.2, 82.4) * mm});
            skLineSegment(sketch, "E6.6.5.8", {"start": v(24.2, 68.4) * mm, "end": v(24.2, 82.4) * mm});
            skLineSegment(sketch, "E6.9.5.8", {"start": v(38.2, 68.4) * mm, "end": v(38.2, 82.4) * mm});
            skLineSegment(sketch, "E6.0.5.9", {"start": v(24.2, 96.4) * mm, "end": v(38.2, 96.4) * mm});
            skLineSegment(sketch, "E6.3.5.9", {"start": v(24.2, 110.4) * mm, "end": v(38.2, 110.4) * mm});
            skLineSegment(sketch, "E6.6.5.9", {"start": v(24.2, 96.4) * mm, "end": v(24.2, 110.4) * mm});
            skLineSegment(sketch, "E6.9.5.9", {"start": v(38.2, 96.4) * mm, "end": v(38.2, 110.4) * mm});
            skLineSegment(sketch, "E6.0.5.10", {"start": v(24.2, 124.4) * mm, "end": v(38.2, 124.4) * mm});
            skLineSegment(sketch, "E6.3.5.10", {"start": v(24.2, 138.4) * mm, "end": v(38.2, 138.4) * mm});
            skLineSegment(sketch, "E6.6.5.10", {"start": v(24.2, 124.4) * mm, "end": v(24.2, 138.4) * mm});
            skLineSegment(sketch, "E6.9.5.10", {"start": v(38.2, 124.4) * mm, "end": v(38.2, 138.4) * mm});
            skLineSegment(sketch, "E6.0.5.11", {"start": v(24.2, 152.4) * mm, "end": v(38.2, 152.4) * mm});
            skLineSegment(sketch, "E6.3.5.11", {"start": v(24.2, 166.4) * mm, "end": v(38.2, 166.4) * mm});
            skLineSegment(sketch, "E6.6.5.11", {"start": v(24.2, 152.4) * mm, "end": v(24.2, 166.4) * mm});
            skLineSegment(sketch, "E6.9.5.11", {"start": v(38.2, 152.4) * mm, "end": v(38.2, 166.4) * mm});
            skLineSegment(sketch, "E6.0.6.1", {"start": v(52.2, -127.6) * mm, "end": v(66.2, -127.6) * mm});
            skLineSegment(sketch, "E6.3.6.1", {"start": v(52.2, -113.6) * mm, "end": v(66.2, -113.6) * mm});
            skLineSegment(sketch, "E6.6.6.1", {"start": v(52.2, -127.6) * mm, "end": v(52.2, -113.6) * mm});
            skLineSegment(sketch, "E6.9.6.1", {"start": v(66.2, -127.6) * mm, "end": v(66.2, -113.6) * mm});
            skLineSegment(sketch, "E6.0.6.2", {"start": v(52.2, -99.6) * mm, "end": v(66.2, -99.6) * mm});
            skLineSegment(sketch, "E6.3.6.2", {"start": v(52.2, -85.6) * mm, "end": v(66.2, -85.6) * mm});
            skLineSegment(sketch, "E6.6.6.2", {"start": v(52.2, -99.6) * mm, "end": v(52.2, -85.6) * mm});
            skLineSegment(sketch, "E6.9.6.2", {"start": v(66.2, -99.6) * mm, "end": v(66.2, -85.6) * mm});
            skLineSegment(sketch, "E6.0.6.3", {"start": v(52.2, -71.6) * mm, "end": v(66.2, -71.6) * mm});
            skLineSegment(sketch, "E6.3.6.3", {"start": v(52.2, -57.6) * mm, "end": v(66.2, -57.6) * mm});
            skLineSegment(sketch, "E6.6.6.3", {"start": v(52.2, -71.6) * mm, "end": v(52.2, -57.6) * mm});
            skLineSegment(sketch, "E6.9.6.3", {"start": v(66.2, -71.6) * mm, "end": v(66.2, -57.6) * mm});
            skLineSegment(sketch, "E6.0.6.4", {"start": v(52.2, -43.6) * mm, "end": v(66.2, -43.6) * mm});
            skLineSegment(sketch, "E6.3.6.4", {"start": v(52.2, -29.6) * mm, "end": v(66.2, -29.6) * mm});
            skLineSegment(sketch, "E6.6.6.4", {"start": v(52.2, -43.6) * mm, "end": v(52.2, -29.6) * mm});
            skLineSegment(sketch, "E6.9.6.4", {"start": v(66.2, -43.6) * mm, "end": v(66.2, -29.6) * mm});
            skLineSegment(sketch, "E6.0.6.5", {"start": v(52.2, -15.6) * mm, "end": v(66.2, -15.6) * mm});
            skLineSegment(sketch, "E6.3.6.5", {"start": v(52.2, -1.6) * mm, "end": v(66.2, -1.6) * mm});
            skLineSegment(sketch, "E6.6.6.5", {"start": v(52.2, -15.6) * mm, "end": v(52.2, -1.6) * mm});
            skLineSegment(sketch, "E6.9.6.5", {"start": v(66.2, -15.6) * mm, "end": v(66.2, -1.6) * mm});
            skLineSegment(sketch, "E6.0.6.6", {"start": v(52.2, 12.4) * mm, "end": v(66.2, 12.4) * mm});
            skLineSegment(sketch, "E6.3.6.6", {"start": v(52.2, 26.4) * mm, "end": v(66.2, 26.4) * mm});
            skLineSegment(sketch, "E6.6.6.6", {"start": v(52.2, 12.4) * mm, "end": v(52.2, 26.4) * mm});
            skLineSegment(sketch, "E6.9.6.6", {"start": v(66.2, 12.4) * mm, "end": v(66.2, 26.4) * mm});
            skLineSegment(sketch, "E6.0.6.7", {"start": v(52.2, 40.4) * mm, "end": v(66.2, 40.4) * mm});
            skLineSegment(sketch, "E6.3.6.7", {"start": v(52.2, 54.4) * mm, "end": v(66.2, 54.4) * mm});
            skLineSegment(sketch, "E6.6.6.7", {"start": v(52.2, 40.4) * mm, "end": v(52.2, 54.4) * mm});
            skLineSegment(sketch, "E6.9.6.7", {"start": v(66.2, 40.4) * mm, "end": v(66.2, 54.4) * mm});
            skLineSegment(sketch, "E6.0.6.8", {"start": v(52.2, 68.4) * mm, "end": v(66.2, 68.4) * mm});
            skLineSegment(sketch, "E6.3.6.8", {"start": v(52.2, 82.4) * mm, "end": v(66.2, 82.4) * mm});
            skLineSegment(sketch, "E6.6.6.8", {"start": v(52.2, 68.4) * mm, "end": v(52.2, 82.4) * mm});
            skLineSegment(sketch, "E6.9.6.8", {"start": v(66.2, 68.4) * mm, "end": v(66.2, 82.4) * mm});
            skLineSegment(sketch, "E6.0.6.9", {"start": v(52.2, 96.4) * mm, "end": v(66.2, 96.4) * mm});
            skLineSegment(sketch, "E6.3.6.9", {"start": v(52.2, 110.4) * mm, "end": v(66.2, 110.4) * mm});
            skLineSegment(sketch, "E6.6.6.9", {"start": v(52.2, 96.4) * mm, "end": v(52.2, 110.4) * mm});
            skLineSegment(sketch, "E6.9.6.9", {"start": v(66.2, 96.4) * mm, "end": v(66.2, 110.4) * mm});
            skLineSegment(sketch, "E6.0.6.10", {"start": v(52.2, 124.4) * mm, "end": v(66.2, 124.4) * mm});
            skLineSegment(sketch, "E6.3.6.10", {"start": v(52.2, 138.4) * mm, "end": v(66.2, 138.4) * mm});
            skLineSegment(sketch, "E6.6.6.10", {"start": v(52.2, 124.4) * mm, "end": v(52.2, 138.4) * mm});
            skLineSegment(sketch, "E6.9.6.10", {"start": v(66.2, 124.4) * mm, "end": v(66.2, 138.4) * mm});
            skLineSegment(sketch, "E6.0.6.11", {"start": v(52.2, 152.4) * mm, "end": v(66.2, 152.4) * mm});
            skLineSegment(sketch, "E6.3.6.11", {"start": v(52.2, 166.4) * mm, "end": v(66.2, 166.4) * mm});
            skLineSegment(sketch, "E6.6.6.11", {"start": v(52.2, 152.4) * mm, "end": v(52.2, 166.4) * mm});
            skLineSegment(sketch, "E6.9.6.11", {"start": v(66.2, 152.4) * mm, "end": v(66.2, 166.4) * mm});
            skLineSegment(sketch, "E6.0.7.1", {"start": v(80.2, -127.6) * mm, "end": v(94.2, -127.6) * mm});
            skLineSegment(sketch, "E6.3.7.1", {"start": v(80.2, -113.6) * mm, "end": v(94.2, -113.6) * mm});
            skLineSegment(sketch, "E6.6.7.1", {"start": v(80.2, -127.6) * mm, "end": v(80.2, -113.6) * mm});
            skLineSegment(sketch, "E6.9.7.1", {"start": v(94.2, -127.6) * mm, "end": v(94.2, -113.6) * mm});
            skLineSegment(sketch, "E6.0.7.2", {"start": v(80.2, -99.6) * mm, "end": v(94.2, -99.6) * mm});
            skLineSegment(sketch, "E6.3.7.2", {"start": v(80.2, -85.6) * mm, "end": v(94.2, -85.6) * mm});
            skLineSegment(sketch, "E6.6.7.2", {"start": v(80.2, -99.6) * mm, "end": v(80.2, -85.6) * mm});
            skLineSegment(sketch, "E6.9.7.2", {"start": v(94.2, -99.6) * mm, "end": v(94.2, -85.6) * mm});
            skLineSegment(sketch, "E6.0.7.3", {"start": v(80.2, -71.6) * mm, "end": v(94.2, -71.6) * mm});
            skLineSegment(sketch, "E6.3.7.3", {"start": v(80.2, -57.6) * mm, "end": v(94.2, -57.6) * mm});
            skLineSegment(sketch, "E6.6.7.3", {"start": v(80.2, -71.6) * mm, "end": v(80.2, -57.6) * mm});
            skLineSegment(sketch, "E6.9.7.3", {"start": v(94.2, -71.6) * mm, "end": v(94.2, -57.6) * mm});
            skLineSegment(sketch, "E6.0.7.4", {"start": v(80.2, -43.6) * mm, "end": v(94.2, -43.6) * mm});
            skLineSegment(sketch, "E6.3.7.4", {"start": v(80.2, -29.6) * mm, "end": v(94.2, -29.6) * mm});
            skLineSegment(sketch, "E6.6.7.4", {"start": v(80.2, -43.6) * mm, "end": v(80.2, -29.6) * mm});
            skLineSegment(sketch, "E6.9.7.4", {"start": v(94.2, -43.6) * mm, "end": v(94.2, -29.6) * mm});
            skLineSegment(sketch, "E6.0.7.5", {"start": v(80.2, -15.6) * mm, "end": v(94.2, -15.6) * mm});
            skLineSegment(sketch, "E6.3.7.5", {"start": v(80.2, -1.6) * mm, "end": v(94.2, -1.6) * mm});
            skLineSegment(sketch, "E6.6.7.5", {"start": v(80.2, -15.6) * mm, "end": v(80.2, -1.6) * mm});
            skLineSegment(sketch, "E6.9.7.5", {"start": v(94.2, -15.6) * mm, "end": v(94.2, -1.6) * mm});
            skLineSegment(sketch, "E6.0.7.6", {"start": v(80.2, 12.4) * mm, "end": v(94.2, 12.4) * mm});
            skLineSegment(sketch, "E6.3.7.6", {"start": v(80.2, 26.4) * mm, "end": v(94.2, 26.4) * mm});
            skLineSegment(sketch, "E6.6.7.6", {"start": v(80.2, 12.4) * mm, "end": v(80.2, 26.4) * mm});
            skLineSegment(sketch, "E6.9.7.6", {"start": v(94.2, 12.4) * mm, "end": v(94.2, 26.4) * mm});
            skLineSegment(sketch, "E6.0.7.7", {"start": v(80.2, 40.4) * mm, "end": v(94.2, 40.4) * mm});
            skLineSegment(sketch, "E6.3.7.7", {"start": v(80.2, 54.4) * mm, "end": v(94.2, 54.4) * mm});
            skLineSegment(sketch, "E6.6.7.7", {"start": v(80.2, 40.4) * mm, "end": v(80.2, 54.4) * mm});
            skLineSegment(sketch, "E6.9.7.7", {"start": v(94.2, 40.4) * mm, "end": v(94.2, 54.4) * mm});
            skLineSegment(sketch, "E6.0.7.8", {"start": v(80.2, 68.4) * mm, "end": v(94.2, 68.4) * mm});
            skLineSegment(sketch, "E6.3.7.8", {"start": v(80.2, 82.4) * mm, "end": v(94.2, 82.4) * mm});
            skLineSegment(sketch, "E6.6.7.8", {"start": v(80.2, 68.4) * mm, "end": v(80.2, 82.4) * mm});
            skLineSegment(sketch, "E6.9.7.8", {"start": v(94.2, 68.4) * mm, "end": v(94.2, 82.4) * mm});
            skLineSegment(sketch, "E6.0.7.9", {"start": v(80.2, 96.4) * mm, "end": v(94.2, 96.4) * mm});
            skLineSegment(sketch, "E6.3.7.9", {"start": v(80.2, 110.4) * mm, "end": v(94.2, 110.4) * mm});
            skLineSegment(sketch, "E6.6.7.9", {"start": v(80.2, 96.4) * mm, "end": v(80.2, 110.4) * mm});
            skLineSegment(sketch, "E6.9.7.9", {"start": v(94.2, 96.4) * mm, "end": v(94.2, 110.4) * mm});
            skLineSegment(sketch, "E6.0.7.10", {"start": v(80.2, 124.4) * mm, "end": v(94.2, 124.4) * mm});
            skLineSegment(sketch, "E6.3.7.10", {"start": v(80.2, 138.4) * mm, "end": v(94.2, 138.4) * mm});
            skLineSegment(sketch, "E6.6.7.10", {"start": v(80.2, 124.4) * mm, "end": v(80.2, 138.4) * mm});
            skLineSegment(sketch, "E6.9.7.10", {"start": v(94.2, 124.4) * mm, "end": v(94.2, 138.4) * mm});
            skLineSegment(sketch, "E6.0.7.11", {"start": v(80.2, 152.4) * mm, "end": v(94.2, 152.4) * mm});
            skLineSegment(sketch, "E6.3.7.11", {"start": v(80.2, 166.4) * mm, "end": v(94.2, 166.4) * mm});
            skLineSegment(sketch, "E6.6.7.11", {"start": v(80.2, 152.4) * mm, "end": v(80.2, 166.4) * mm});
            skLineSegment(sketch, "E6.9.7.11", {"start": v(94.2, 152.4) * mm, "end": v(94.2, 166.4) * mm});
            skLineSegment(sketch, "E6.0.8.1", {"start": v(108.2, -127.6) * mm, "end": v(122.2, -127.6) * mm});
            skLineSegment(sketch, "E6.3.8.1", {"start": v(108.2, -113.6) * mm, "end": v(122.2, -113.6) * mm});
            skLineSegment(sketch, "E6.6.8.1", {"start": v(108.2, -127.6) * mm, "end": v(108.2, -113.6) * mm});
            skLineSegment(sketch, "E6.9.8.1", {"start": v(122.2, -127.6) * mm, "end": v(122.2, -113.6) * mm});
            skLineSegment(sketch, "E6.0.8.2", {"start": v(108.2, -99.6) * mm, "end": v(122.2, -99.6) * mm});
            skLineSegment(sketch, "E6.3.8.2", {"start": v(108.2, -85.6) * mm, "end": v(122.2, -85.6) * mm});
            skLineSegment(sketch, "E6.6.8.2", {"start": v(108.2, -99.6) * mm, "end": v(108.2, -85.6) * mm});
            skLineSegment(sketch, "E6.9.8.2", {"start": v(122.2, -99.6) * mm, "end": v(122.2, -85.6) * mm});
            skLineSegment(sketch, "E6.0.8.3", {"start": v(108.2, -71.6) * mm, "end": v(122.2, -71.6) * mm});
            skLineSegment(sketch, "E6.3.8.3", {"start": v(108.2, -57.6) * mm, "end": v(122.2, -57.6) * mm});
            skLineSegment(sketch, "E6.6.8.3", {"start": v(108.2, -71.6) * mm, "end": v(108.2, -57.6) * mm});
            skLineSegment(sketch, "E6.9.8.3", {"start": v(122.2, -71.6) * mm, "end": v(122.2, -57.6) * mm});
            skLineSegment(sketch, "E6.0.8.4", {"start": v(108.2, -43.6) * mm, "end": v(122.2, -43.6) * mm});
            skLineSegment(sketch, "E6.3.8.4", {"start": v(108.2, -29.6) * mm, "end": v(122.2, -29.6) * mm});
            skLineSegment(sketch, "E6.6.8.4", {"start": v(108.2, -43.6) * mm, "end": v(108.2, -29.6) * mm});
            skLineSegment(sketch, "E6.9.8.4", {"start": v(122.2, -43.6) * mm, "end": v(122.2, -29.6) * mm});
            skLineSegment(sketch, "E6.0.8.5", {"start": v(108.2, -15.6) * mm, "end": v(122.2, -15.6) * mm});
            skLineSegment(sketch, "E6.3.8.5", {"start": v(108.2, -1.6) * mm, "end": v(122.2, -1.6) * mm});
            skLineSegment(sketch, "E6.6.8.5", {"start": v(108.2, -15.6) * mm, "end": v(108.2, -1.6) * mm});
            skLineSegment(sketch, "E6.9.8.5", {"start": v(122.2, -15.6) * mm, "end": v(122.2, -1.6) * mm});
            skLineSegment(sketch, "E6.0.8.6", {"start": v(108.2, 12.4) * mm, "end": v(122.2, 12.4) * mm});
            skLineSegment(sketch, "E6.3.8.6", {"start": v(108.2, 26.4) * mm, "end": v(122.2, 26.4) * mm});
            skLineSegment(sketch, "E6.6.8.6", {"start": v(108.2, 12.4) * mm, "end": v(108.2, 26.4) * mm});
            skLineSegment(sketch, "E6.9.8.6", {"start": v(122.2, 12.4) * mm, "end": v(122.2, 26.4) * mm});
            skLineSegment(sketch, "E6.0.8.7", {"start": v(108.2, 40.4) * mm, "end": v(122.2, 40.4) * mm});
            skLineSegment(sketch, "E6.3.8.7", {"start": v(108.2, 54.4) * mm, "end": v(122.2, 54.4) * mm});
            skLineSegment(sketch, "E6.6.8.7", {"start": v(108.2, 40.4) * mm, "end": v(108.2, 54.4) * mm});
            skLineSegment(sketch, "E6.9.8.7", {"start": v(122.2, 40.4) * mm, "end": v(122.2, 54.4) * mm});
            skLineSegment(sketch, "E6.0.8.8", {"start": v(108.2, 68.4) * mm, "end": v(122.2, 68.4) * mm});
            skLineSegment(sketch, "E6.3.8.8", {"start": v(108.2, 82.4) * mm, "end": v(122.2, 82.4) * mm});
            skLineSegment(sketch, "E6.6.8.8", {"start": v(108.2, 68.4) * mm, "end": v(108.2, 82.4) * mm});
            skLineSegment(sketch, "E6.9.8.8", {"start": v(122.2, 68.4) * mm, "end": v(122.2, 82.4) * mm});
            skLineSegment(sketch, "E6.0.8.9", {"start": v(108.2, 96.4) * mm, "end": v(122.2, 96.4) * mm});
            skLineSegment(sketch, "E6.3.8.9", {"start": v(108.2, 110.4) * mm, "end": v(122.2, 110.4) * mm});
            skLineSegment(sketch, "E6.6.8.9", {"start": v(108.2, 96.4) * mm, "end": v(108.2, 110.4) * mm});
            skLineSegment(sketch, "E6.9.8.9", {"start": v(122.2, 96.4) * mm, "end": v(122.2, 110.4) * mm});
            skLineSegment(sketch, "E6.0.8.10", {"start": v(108.2, 124.4) * mm, "end": v(122.2, 124.4) * mm});
            skLineSegment(sketch, "E6.3.8.10", {"start": v(108.2, 138.4) * mm, "end": v(122.2, 138.4) * mm});
            skLineSegment(sketch, "E6.6.8.10", {"start": v(108.2, 124.4) * mm, "end": v(108.2, 138.4) * mm});
            skLineSegment(sketch, "E6.9.8.10", {"start": v(122.2, 124.4) * mm, "end": v(122.2, 138.4) * mm});
            skLineSegment(sketch, "E6.0.8.11", {"start": v(108.2, 152.4) * mm, "end": v(122.2, 152.4) * mm});
            skLineSegment(sketch, "E6.3.8.11", {"start": v(108.2, 166.4) * mm, "end": v(122.2, 166.4) * mm});
            skLineSegment(sketch, "E6.6.8.11", {"start": v(108.2, 152.4) * mm, "end": v(108.2, 166.4) * mm});
            skLineSegment(sketch, "E6.9.8.11", {"start": v(122.2, 152.4) * mm, "end": v(122.2, 166.4) * mm});
            skLineSegment(sketch, "E7.0.0.1", {"start": v(94.2, -113.6) * mm, "end": v(108.2, -113.6) * mm});
            skLineSegment(sketch, "E7.3.0.1", {"start": v(94.2, -99.6) * mm, "end": v(108.2, -99.6) * mm});
            skLineSegment(sketch, "E7.6.0.1", {"start": v(108.2, -99.6) * mm, "end": v(108.2, -113.6) * mm});
            skLineSegment(sketch, "E7.9.0.1", {"start": v(94.2, -99.6) * mm, "end": v(94.2, -113.6) * mm});
            skLineSegment(sketch, "E7.0.0.2", {"start": v(94.2, -85.6) * mm, "end": v(108.2, -85.6) * mm});
            skLineSegment(sketch, "E7.3.0.2", {"start": v(94.2, -71.6) * mm, "end": v(108.2, -71.6) * mm});
            skLineSegment(sketch, "E7.6.0.2", {"start": v(108.2, -71.6) * mm, "end": v(108.2, -85.6) * mm});
            skLineSegment(sketch, "E7.9.0.2", {"start": v(94.2, -71.6) * mm, "end": v(94.2, -85.6) * mm});
            skLineSegment(sketch, "E7.0.0.3", {"start": v(94.2, -57.6) * mm, "end": v(108.2, -57.6) * mm});
            skLineSegment(sketch, "E7.3.0.3", {"start": v(94.2, -43.6) * mm, "end": v(108.2, -43.6) * mm});
            skLineSegment(sketch, "E7.6.0.3", {"start": v(108.2, -43.6) * mm, "end": v(108.2, -57.6) * mm});
            skLineSegment(sketch, "E7.9.0.3", {"start": v(94.2, -43.6) * mm, "end": v(94.2, -57.6) * mm});
            skLineSegment(sketch, "E7.0.0.4", {"start": v(94.2, -29.6) * mm, "end": v(108.2, -29.6) * mm});
            skLineSegment(sketch, "E7.3.0.4", {"start": v(94.2, -15.6) * mm, "end": v(108.2, -15.6) * mm});
            skLineSegment(sketch, "E7.6.0.4", {"start": v(108.2, -15.6) * mm, "end": v(108.2, -29.6) * mm});
            skLineSegment(sketch, "E7.9.0.4", {"start": v(94.2, -15.6) * mm, "end": v(94.2, -29.6) * mm});
            skLineSegment(sketch, "E7.0.0.5", {"start": v(94.2, -1.6) * mm, "end": v(108.2, -1.6) * mm});
            skLineSegment(sketch, "E7.3.0.5", {"start": v(94.2, 12.4) * mm, "end": v(108.2, 12.4) * mm});
            skLineSegment(sketch, "E7.6.0.5", {"start": v(108.2, 12.4) * mm, "end": v(108.2, -1.6) * mm});
            skLineSegment(sketch, "E7.9.0.5", {"start": v(94.2, 12.4) * mm, "end": v(94.2, -1.6) * mm});
            skLineSegment(sketch, "E7.0.0.6", {"start": v(94.2, 26.4) * mm, "end": v(108.2, 26.4) * mm});
            skLineSegment(sketch, "E7.3.0.6", {"start": v(94.2, 40.4) * mm, "end": v(108.2, 40.4) * mm});
            skLineSegment(sketch, "E7.6.0.6", {"start": v(108.2, 40.4) * mm, "end": v(108.2, 26.4) * mm});
            skLineSegment(sketch, "E7.9.0.6", {"start": v(94.2, 40.4) * mm, "end": v(94.2, 26.4) * mm});
            skLineSegment(sketch, "E7.0.0.7", {"start": v(94.2, 54.4) * mm, "end": v(108.2, 54.4) * mm});
            skLineSegment(sketch, "E7.3.0.7", {"start": v(94.2, 68.4) * mm, "end": v(108.2, 68.4) * mm});
            skLineSegment(sketch, "E7.6.0.7", {"start": v(108.2, 68.4) * mm, "end": v(108.2, 54.4) * mm});
            skLineSegment(sketch, "E7.9.0.7", {"start": v(94.2, 68.4) * mm, "end": v(94.2, 54.4) * mm});
            skLineSegment(sketch, "E7.0.0.8", {"start": v(94.2, 82.4) * mm, "end": v(108.2, 82.4) * mm});
            skLineSegment(sketch, "E7.3.0.8", {"start": v(94.2, 96.4) * mm, "end": v(108.2, 96.4) * mm});
            skLineSegment(sketch, "E7.6.0.8", {"start": v(108.2, 96.4) * mm, "end": v(108.2, 82.4) * mm});
            skLineSegment(sketch, "E7.9.0.8", {"start": v(94.2, 96.4) * mm, "end": v(94.2, 82.4) * mm});
            skLineSegment(sketch, "E7.0.0.9", {"start": v(94.2, 110.4) * mm, "end": v(108.2, 110.4) * mm});
            skLineSegment(sketch, "E7.3.0.9", {"start": v(94.2, 124.4) * mm, "end": v(108.2, 124.4) * mm});
            skLineSegment(sketch, "E7.6.0.9", {"start": v(108.2, 124.4) * mm, "end": v(108.2, 110.4) * mm});
            skLineSegment(sketch, "E7.9.0.9", {"start": v(94.2, 124.4) * mm, "end": v(94.2, 110.4) * mm});
            skLineSegment(sketch, "E7.0.0.10", {"start": v(94.2, 138.4) * mm, "end": v(108.2, 138.4) * mm});
            skLineSegment(sketch, "E7.3.0.10", {"start": v(94.2, 152.4) * mm, "end": v(108.2, 152.4) * mm});
            skLineSegment(sketch, "E7.6.0.10", {"start": v(108.2, 152.4) * mm, "end": v(108.2, 138.4) * mm});
            skLineSegment(sketch, "E7.9.0.10", {"start": v(94.2, 152.4) * mm, "end": v(94.2, 138.4) * mm});
            skLineSegment(sketch, "E8.0.1.0", {"start": v(66.2, -141.6) * mm, "end": v(80.2, -141.6) * mm});
            skLineSegment(sketch, "E8.3.1.0", {"start": v(66.2, -127.6) * mm, "end": v(80.2, -127.6) * mm});
            skLineSegment(sketch, "E8.6.1.0", {"start": v(80.2, -127.6) * mm, "end": v(80.2, -141.6) * mm});
            skLineSegment(sketch, "E8.9.1.0", {"start": v(66.2, -127.6) * mm, "end": v(66.2, -141.6) * mm});
            skLineSegment(sketch, "E8.0.1.1", {"start": v(66.2, -113.6) * mm, "end": v(80.2, -113.6) * mm});
            skLineSegment(sketch, "E8.3.1.1", {"start": v(66.2, -99.6) * mm, "end": v(80.2, -99.6) * mm});
            skLineSegment(sketch, "E8.6.1.1", {"start": v(80.2, -99.6) * mm, "end": v(80.2, -113.6) * mm});
            skLineSegment(sketch, "E8.9.1.1", {"start": v(66.2, -99.6) * mm, "end": v(66.2, -113.6) * mm});
            skLineSegment(sketch, "E8.0.1.2", {"start": v(66.2, -85.6) * mm, "end": v(80.2, -85.6) * mm});
            skLineSegment(sketch, "E8.3.1.2", {"start": v(66.2, -71.6) * mm, "end": v(80.2, -71.6) * mm});
            skLineSegment(sketch, "E8.6.1.2", {"start": v(80.2, -71.6) * mm, "end": v(80.2, -85.6) * mm});
            skLineSegment(sketch, "E8.9.1.2", {"start": v(66.2, -71.6) * mm, "end": v(66.2, -85.6) * mm});
            skLineSegment(sketch, "E8.0.1.3", {"start": v(66.2, -57.6) * mm, "end": v(80.2, -57.6) * mm});
            skLineSegment(sketch, "E8.3.1.3", {"start": v(66.2, -43.6) * mm, "end": v(80.2, -43.6) * mm});
            skLineSegment(sketch, "E8.6.1.3", {"start": v(80.2, -43.6) * mm, "end": v(80.2, -57.6) * mm});
            skLineSegment(sketch, "E8.9.1.3", {"start": v(66.2, -43.6) * mm, "end": v(66.2, -57.6) * mm});
            skLineSegment(sketch, "E8.0.1.4", {"start": v(66.2, -29.6) * mm, "end": v(80.2, -29.6) * mm});
            skLineSegment(sketch, "E8.3.1.4", {"start": v(66.2, -15.6) * mm, "end": v(80.2, -15.6) * mm});
            skLineSegment(sketch, "E8.6.1.4", {"start": v(80.2, -15.6) * mm, "end": v(80.2, -29.6) * mm});
            skLineSegment(sketch, "E8.9.1.4", {"start": v(66.2, -15.6) * mm, "end": v(66.2, -29.6) * mm});
            skLineSegment(sketch, "E8.0.1.5", {"start": v(66.2, -1.6) * mm, "end": v(80.2, -1.6) * mm});
            skLineSegment(sketch, "E8.3.1.5", {"start": v(66.2, 12.4) * mm, "end": v(80.2, 12.4) * mm});
            skLineSegment(sketch, "E8.6.1.5", {"start": v(80.2, 12.4) * mm, "end": v(80.2, -1.6) * mm});
            skLineSegment(sketch, "E8.9.1.5", {"start": v(66.2, 12.4) * mm, "end": v(66.2, -1.6) * mm});
            skLineSegment(sketch, "E8.0.1.6", {"start": v(66.2, 26.4) * mm, "end": v(80.2, 26.4) * mm});
            skLineSegment(sketch, "E8.3.1.6", {"start": v(66.2, 40.4) * mm, "end": v(80.2, 40.4) * mm});
            skLineSegment(sketch, "E8.6.1.6", {"start": v(80.2, 40.4) * mm, "end": v(80.2, 26.4) * mm});
            skLineSegment(sketch, "E8.9.1.6", {"start": v(66.2, 40.4) * mm, "end": v(66.2, 26.4) * mm});
            skLineSegment(sketch, "E8.0.1.7", {"start": v(66.2, 54.4) * mm, "end": v(80.2, 54.4) * mm});
            skLineSegment(sketch, "E8.3.1.7", {"start": v(66.2, 68.4) * mm, "end": v(80.2, 68.4) * mm});
            skLineSegment(sketch, "E8.6.1.7", {"start": v(80.2, 68.4) * mm, "end": v(80.2, 54.4) * mm});
            skLineSegment(sketch, "E8.9.1.7", {"start": v(66.2, 68.4) * mm, "end": v(66.2, 54.4) * mm});
            skLineSegment(sketch, "E8.0.1.8", {"start": v(66.2, 82.4) * mm, "end": v(80.2, 82.4) * mm});
            skLineSegment(sketch, "E8.3.1.8", {"start": v(66.2, 96.4) * mm, "end": v(80.2, 96.4) * mm});
            skLineSegment(sketch, "E8.6.1.8", {"start": v(80.2, 96.4) * mm, "end": v(80.2, 82.4) * mm});
            skLineSegment(sketch, "E8.9.1.8", {"start": v(66.2, 96.4) * mm, "end": v(66.2, 82.4) * mm});
            skLineSegment(sketch, "E8.0.1.9", {"start": v(66.2, 110.4) * mm, "end": v(80.2, 110.4) * mm});
            skLineSegment(sketch, "E8.3.1.9", {"start": v(66.2, 124.4) * mm, "end": v(80.2, 124.4) * mm});
            skLineSegment(sketch, "E8.6.1.9", {"start": v(80.2, 124.4) * mm, "end": v(80.2, 110.4) * mm});
            skLineSegment(sketch, "E8.9.1.9", {"start": v(66.2, 124.4) * mm, "end": v(66.2, 110.4) * mm});
            skLineSegment(sketch, "E8.0.1.10", {"start": v(66.2, 138.4) * mm, "end": v(80.2, 138.4) * mm});
            skLineSegment(sketch, "E8.3.1.10", {"start": v(66.2, 152.4) * mm, "end": v(80.2, 152.4) * mm});
            skLineSegment(sketch, "E8.6.1.10", {"start": v(80.2, 152.4) * mm, "end": v(80.2, 138.4) * mm});
            skLineSegment(sketch, "E8.9.1.10", {"start": v(66.2, 152.4) * mm, "end": v(66.2, 138.4) * mm});
            skLineSegment(sketch, "E8.0.2.0", {"start": v(38.2, -141.6) * mm, "end": v(52.2, -141.6) * mm});
            skLineSegment(sketch, "E8.3.2.0", {"start": v(38.2, -127.6) * mm, "end": v(52.2, -127.6) * mm});
            skLineSegment(sketch, "E8.6.2.0", {"start": v(52.2, -127.6) * mm, "end": v(52.2, -141.6) * mm});
            skLineSegment(sketch, "E8.9.2.0", {"start": v(38.2, -127.6) * mm, "end": v(38.2, -141.6) * mm});
            skLineSegment(sketch, "E8.0.2.1", {"start": v(38.2, -113.6) * mm, "end": v(52.2, -113.6) * mm});
            skLineSegment(sketch, "E8.3.2.1", {"start": v(38.2, -99.6) * mm, "end": v(52.2, -99.6) * mm});
            skLineSegment(sketch, "E8.6.2.1", {"start": v(52.2, -99.6) * mm, "end": v(52.2, -113.6) * mm});
            skLineSegment(sketch, "E8.9.2.1", {"start": v(38.2, -99.6) * mm, "end": v(38.2, -113.6) * mm});
            skLineSegment(sketch, "E8.0.2.2", {"start": v(38.2, -85.6) * mm, "end": v(52.2, -85.6) * mm});
            skLineSegment(sketch, "E8.3.2.2", {"start": v(38.2, -71.6) * mm, "end": v(52.2, -71.6) * mm});
            skLineSegment(sketch, "E8.6.2.2", {"start": v(52.2, -71.6) * mm, "end": v(52.2, -85.6) * mm});
            skLineSegment(sketch, "E8.9.2.2", {"start": v(38.2, -71.6) * mm, "end": v(38.2, -85.6) * mm});
            skLineSegment(sketch, "E8.0.2.3", {"start": v(38.2, -57.6) * mm, "end": v(52.2, -57.6) * mm});
            skLineSegment(sketch, "E8.3.2.3", {"start": v(38.2, -43.6) * mm, "end": v(52.2, -43.6) * mm});
            skLineSegment(sketch, "E8.6.2.3", {"start": v(52.2, -43.6) * mm, "end": v(52.2, -57.6) * mm});
            skLineSegment(sketch, "E8.9.2.3", {"start": v(38.2, -43.6) * mm, "end": v(38.2, -57.6) * mm});
            skLineSegment(sketch, "E8.0.2.4", {"start": v(38.2, -29.6) * mm, "end": v(52.2, -29.6) * mm});
            skLineSegment(sketch, "E8.3.2.4", {"start": v(38.2, -15.6) * mm, "end": v(52.2, -15.6) * mm});
            skLineSegment(sketch, "E8.6.2.4", {"start": v(52.2, -15.6) * mm, "end": v(52.2, -29.6) * mm});
            skLineSegment(sketch, "E8.9.2.4", {"start": v(38.2, -15.6) * mm, "end": v(38.2, -29.6) * mm});
            skLineSegment(sketch, "E8.0.2.5", {"start": v(38.2, -1.6) * mm, "end": v(52.2, -1.6) * mm});
            skLineSegment(sketch, "E8.3.2.5", {"start": v(38.2, 12.4) * mm, "end": v(52.2, 12.4) * mm});
            skLineSegment(sketch, "E8.6.2.5", {"start": v(52.2, 12.4) * mm, "end": v(52.2, -1.6) * mm});
            skLineSegment(sketch, "E8.9.2.5", {"start": v(38.2, 12.4) * mm, "end": v(38.2, -1.6) * mm});
            skLineSegment(sketch, "E8.0.2.6", {"start": v(38.2, 26.4) * mm, "end": v(52.2, 26.4) * mm});
            skLineSegment(sketch, "E8.3.2.6", {"start": v(38.2, 40.4) * mm, "end": v(52.2, 40.4) * mm});
            skLineSegment(sketch, "E8.6.2.6", {"start": v(52.2, 40.4) * mm, "end": v(52.2, 26.4) * mm});
            skLineSegment(sketch, "E8.9.2.6", {"start": v(38.2, 40.4) * mm, "end": v(38.2, 26.4) * mm});
            skLineSegment(sketch, "E8.0.2.7", {"start": v(38.2, 54.4) * mm, "end": v(52.2, 54.4) * mm});
            skLineSegment(sketch, "E8.3.2.7", {"start": v(38.2, 68.4) * mm, "end": v(52.2, 68.4) * mm});
            skLineSegment(sketch, "E8.6.2.7", {"start": v(52.2, 68.4) * mm, "end": v(52.2, 54.4) * mm});
            skLineSegment(sketch, "E8.9.2.7", {"start": v(38.2, 68.4) * mm, "end": v(38.2, 54.4) * mm});
            skLineSegment(sketch, "E8.0.2.8", {"start": v(38.2, 82.4) * mm, "end": v(52.2, 82.4) * mm});
            skLineSegment(sketch, "E8.3.2.8", {"start": v(38.2, 96.4) * mm, "end": v(52.2, 96.4) * mm});
            skLineSegment(sketch, "E8.6.2.8", {"start": v(52.2, 96.4) * mm, "end": v(52.2, 82.4) * mm});
            skLineSegment(sketch, "E8.9.2.8", {"start": v(38.2, 96.4) * mm, "end": v(38.2, 82.4) * mm});
            skLineSegment(sketch, "E8.0.2.9", {"start": v(38.2, 110.4) * mm, "end": v(52.2, 110.4) * mm});
            skLineSegment(sketch, "E8.3.2.9", {"start": v(38.2, 124.4) * mm, "end": v(52.2, 124.4) * mm});
            skLineSegment(sketch, "E8.6.2.9", {"start": v(52.2, 124.4) * mm, "end": v(52.2, 110.4) * mm});
            skLineSegment(sketch, "E8.9.2.9", {"start": v(38.2, 124.4) * mm, "end": v(38.2, 110.4) * mm});
            skLineSegment(sketch, "E8.0.2.10", {"start": v(38.2, 138.4) * mm, "end": v(52.2, 138.4) * mm});
            skLineSegment(sketch, "E8.3.2.10", {"start": v(38.2, 152.4) * mm, "end": v(52.2, 152.4) * mm});
            skLineSegment(sketch, "E8.6.2.10", {"start": v(52.2, 152.4) * mm, "end": v(52.2, 138.4) * mm});
            skLineSegment(sketch, "E8.9.2.10", {"start": v(38.2, 152.4) * mm, "end": v(38.2, 138.4) * mm});
            skLineSegment(sketch, "E8.0.3.0", {"start": v(10.2, -141.6) * mm, "end": v(24.2, -141.6) * mm});
            skLineSegment(sketch, "E8.3.3.0", {"start": v(10.2, -127.6) * mm, "end": v(24.2, -127.6) * mm});
            skLineSegment(sketch, "E8.6.3.0", {"start": v(24.2, -127.6) * mm, "end": v(24.2, -141.6) * mm});
            skLineSegment(sketch, "E8.9.3.0", {"start": v(10.2, -127.6) * mm, "end": v(10.2, -141.6) * mm});
            skLineSegment(sketch, "E8.0.3.1", {"start": v(10.2, -113.6) * mm, "end": v(24.2, -113.6) * mm});
            skLineSegment(sketch, "E8.3.3.1", {"start": v(10.2, -99.6) * mm, "end": v(24.2, -99.6) * mm});
            skLineSegment(sketch, "E8.6.3.1", {"start": v(24.2, -99.6) * mm, "end": v(24.2, -113.6) * mm});
            skLineSegment(sketch, "E8.9.3.1", {"start": v(10.2, -99.6) * mm, "end": v(10.2, -113.6) * mm});
            skLineSegment(sketch, "E8.0.3.2", {"start": v(10.2, -85.6) * mm, "end": v(24.2, -85.6) * mm});
            skLineSegment(sketch, "E8.3.3.2", {"start": v(10.2, -71.6) * mm, "end": v(24.2, -71.6) * mm});
            skLineSegment(sketch, "E8.6.3.2", {"start": v(24.2, -71.6) * mm, "end": v(24.2, -85.6) * mm});
            skLineSegment(sketch, "E8.9.3.2", {"start": v(10.2, -71.6) * mm, "end": v(10.2, -85.6) * mm});
            skLineSegment(sketch, "E8.0.3.3", {"start": v(10.2, -57.6) * mm, "end": v(24.2, -57.6) * mm});
            skLineSegment(sketch, "E8.3.3.3", {"start": v(10.2, -43.6) * mm, "end": v(24.2, -43.6) * mm});
            skLineSegment(sketch, "E8.6.3.3", {"start": v(24.2, -43.6) * mm, "end": v(24.2, -57.6) * mm});
            skLineSegment(sketch, "E8.9.3.3", {"start": v(10.2, -43.6) * mm, "end": v(10.2, -57.6) * mm});
            skLineSegment(sketch, "E8.0.3.4", {"start": v(10.2, -29.6) * mm, "end": v(24.2, -29.6) * mm});
            skLineSegment(sketch, "E8.3.3.4", {"start": v(10.2, -15.6) * mm, "end": v(24.2, -15.6) * mm});
            skLineSegment(sketch, "E8.6.3.4", {"start": v(24.2, -15.6) * mm, "end": v(24.2, -29.6) * mm});
            skLineSegment(sketch, "E8.9.3.4", {"start": v(10.2, -15.6) * mm, "end": v(10.2, -29.6) * mm});
            skLineSegment(sketch, "E8.0.3.5", {"start": v(10.2, -1.6) * mm, "end": v(24.2, -1.6) * mm});
            skLineSegment(sketch, "E8.3.3.5", {"start": v(10.2, 12.4) * mm, "end": v(24.2, 12.4) * mm});
            skLineSegment(sketch, "E8.6.3.5", {"start": v(24.2, 12.4) * mm, "end": v(24.2, -1.6) * mm});
            skLineSegment(sketch, "E8.9.3.5", {"start": v(10.2, 12.4) * mm, "end": v(10.2, -1.6) * mm});
            skLineSegment(sketch, "E8.0.3.6", {"start": v(10.2, 26.4) * mm, "end": v(24.2, 26.4) * mm});
            skLineSegment(sketch, "E8.3.3.6", {"start": v(10.2, 40.4) * mm, "end": v(24.2, 40.4) * mm});
            skLineSegment(sketch, "E8.6.3.6", {"start": v(24.2, 40.4) * mm, "end": v(24.2, 26.4) * mm});
            skLineSegment(sketch, "E8.9.3.6", {"start": v(10.2, 40.4) * mm, "end": v(10.2, 26.4) * mm});
            skLineSegment(sketch, "E8.0.3.7", {"start": v(10.2, 54.4) * mm, "end": v(24.2, 54.4) * mm});
            skLineSegment(sketch, "E8.3.3.7", {"start": v(10.2, 68.4) * mm, "end": v(24.2, 68.4) * mm});
            skLineSegment(sketch, "E8.6.3.7", {"start": v(24.2, 68.4) * mm, "end": v(24.2, 54.4) * mm});
            skLineSegment(sketch, "E8.9.3.7", {"start": v(10.2, 68.4) * mm, "end": v(10.2, 54.4) * mm});
            skLineSegment(sketch, "E8.0.3.8", {"start": v(10.2, 82.4) * mm, "end": v(24.2, 82.4) * mm});
            skLineSegment(sketch, "E8.3.3.8", {"start": v(10.2, 96.4) * mm, "end": v(24.2, 96.4) * mm});
            skLineSegment(sketch, "E8.6.3.8", {"start": v(24.2, 96.4) * mm, "end": v(24.2, 82.4) * mm});
            skLineSegment(sketch, "E8.9.3.8", {"start": v(10.2, 96.4) * mm, "end": v(10.2, 82.4) * mm});
            skLineSegment(sketch, "E8.0.3.9", {"start": v(10.2, 110.4) * mm, "end": v(24.2, 110.4) * mm});
            skLineSegment(sketch, "E8.3.3.9", {"start": v(10.2, 124.4) * mm, "end": v(24.2, 124.4) * mm});
            skLineSegment(sketch, "E8.6.3.9", {"start": v(24.2, 124.4) * mm, "end": v(24.2, 110.4) * mm});
            skLineSegment(sketch, "E8.9.3.9", {"start": v(10.2, 124.4) * mm, "end": v(10.2, 110.4) * mm});
            skLineSegment(sketch, "E8.0.3.10", {"start": v(10.2, 138.4) * mm, "end": v(24.2, 138.4) * mm});
            skLineSegment(sketch, "E8.3.3.10", {"start": v(10.2, 152.4) * mm, "end": v(24.2, 152.4) * mm});
            skLineSegment(sketch, "E8.6.3.10", {"start": v(24.2, 152.4) * mm, "end": v(24.2, 138.4) * mm});
            skLineSegment(sketch, "E8.9.3.10", {"start": v(10.2, 152.4) * mm, "end": v(10.2, 138.4) * mm});
            skLineSegment(sketch, "E8.0.4.0", {"start": v(-17.8, -141.6) * mm, "end": v(-3.8, -141.6) * mm});
            skLineSegment(sketch, "E8.3.4.0", {"start": v(-17.8, -127.6) * mm, "end": v(-3.8, -127.6) * mm});
            skLineSegment(sketch, "E8.6.4.0", {"start": v(-3.8, -127.6) * mm, "end": v(-3.8, -141.6) * mm});
            skLineSegment(sketch, "E8.9.4.0", {"start": v(-17.8, -127.6) * mm, "end": v(-17.8, -141.6) * mm});
            skLineSegment(sketch, "E8.0.4.1", {"start": v(-17.8, -113.6) * mm, "end": v(-3.8, -113.6) * mm});
            skLineSegment(sketch, "E8.3.4.1", {"start": v(-17.8, -99.6) * mm, "end": v(-3.8, -99.6) * mm});
            skLineSegment(sketch, "E8.6.4.1", {"start": v(-3.8, -99.6) * mm, "end": v(-3.8, -113.6) * mm});
            skLineSegment(sketch, "E8.9.4.1", {"start": v(-17.8, -99.6) * mm, "end": v(-17.8, -113.6) * mm});
            skLineSegment(sketch, "E8.0.4.2", {"start": v(-17.8, -85.6) * mm, "end": v(-3.8, -85.6) * mm});
            skLineSegment(sketch, "E8.3.4.2", {"start": v(-17.8, -71.6) * mm, "end": v(-3.8, -71.6) * mm});
            skLineSegment(sketch, "E8.6.4.2", {"start": v(-3.8, -71.6) * mm, "end": v(-3.8, -85.6) * mm});
            skLineSegment(sketch, "E8.9.4.2", {"start": v(-17.8, -71.6) * mm, "end": v(-17.8, -85.6) * mm});
            skLineSegment(sketch, "E8.0.4.3", {"start": v(-17.8, -57.6) * mm, "end": v(-3.8, -57.6) * mm});
            skLineSegment(sketch, "E8.3.4.3", {"start": v(-17.8, -43.6) * mm, "end": v(-3.8, -43.6) * mm});
            skLineSegment(sketch, "E8.6.4.3", {"start": v(-3.8, -43.6) * mm, "end": v(-3.8, -57.6) * mm});
            skLineSegment(sketch, "E8.9.4.3", {"start": v(-17.8, -43.6) * mm, "end": v(-17.8, -57.6) * mm});
            skLineSegment(sketch, "E8.0.4.4", {"start": v(-17.8, -29.6) * mm, "end": v(-3.8, -29.6) * mm});
            skLineSegment(sketch, "E8.3.4.4", {"start": v(-17.8, -15.6) * mm, "end": v(-3.8, -15.6) * mm});
            skLineSegment(sketch, "E8.6.4.4", {"start": v(-3.8, -15.6) * mm, "end": v(-3.8, -29.6) * mm});
            skLineSegment(sketch, "E8.9.4.4", {"start": v(-17.8, -15.6) * mm, "end": v(-17.8, -29.6) * mm});
            skLineSegment(sketch, "E8.0.4.5", {"start": v(-17.8, -1.6) * mm, "end": v(-3.8, -1.6) * mm});
            skLineSegment(sketch, "E8.3.4.5", {"start": v(-17.8, 12.4) * mm, "end": v(-3.8, 12.4) * mm});
            skLineSegment(sketch, "E8.6.4.5", {"start": v(-3.8, 12.4) * mm, "end": v(-3.8, -1.6) * mm});
            skLineSegment(sketch, "E8.9.4.5", {"start": v(-17.8, 12.4) * mm, "end": v(-17.8, -1.6) * mm});
            skLineSegment(sketch, "E8.0.4.6", {"start": v(-17.8, 26.4) * mm, "end": v(-3.8, 26.4) * mm});
            skLineSegment(sketch, "E8.3.4.6", {"start": v(-17.8, 40.4) * mm, "end": v(-3.8, 40.4) * mm});
            skLineSegment(sketch, "E8.6.4.6", {"start": v(-3.8, 40.4) * mm, "end": v(-3.8, 26.4) * mm});
            skLineSegment(sketch, "E8.9.4.6", {"start": v(-17.8, 40.4) * mm, "end": v(-17.8, 26.4) * mm});
            skLineSegment(sketch, "E8.0.4.7", {"start": v(-17.8, 54.4) * mm, "end": v(-3.8, 54.4) * mm});
            skLineSegment(sketch, "E8.3.4.7", {"start": v(-17.8, 68.4) * mm, "end": v(-3.8, 68.4) * mm});
            skLineSegment(sketch, "E8.6.4.7", {"start": v(-3.8, 68.4) * mm, "end": v(-3.8, 54.4) * mm});
            skLineSegment(sketch, "E8.9.4.7", {"start": v(-17.8, 68.4) * mm, "end": v(-17.8, 54.4) * mm});
            skLineSegment(sketch, "E8.0.4.8", {"start": v(-17.8, 82.4) * mm, "end": v(-3.8, 82.4) * mm});
            skLineSegment(sketch, "E8.3.4.8", {"start": v(-17.8, 96.4) * mm, "end": v(-3.8, 96.4) * mm});
            skLineSegment(sketch, "E8.6.4.8", {"start": v(-3.8, 96.4) * mm, "end": v(-3.8, 82.4) * mm});
            skLineSegment(sketch, "E8.9.4.8", {"start": v(-17.8, 96.4) * mm, "end": v(-17.8, 82.4) * mm});
            skLineSegment(sketch, "E8.0.4.9", {"start": v(-17.8, 110.4) * mm, "end": v(-3.8, 110.4) * mm});
            skLineSegment(sketch, "E8.3.4.9", {"start": v(-17.8, 124.4) * mm, "end": v(-3.8, 124.4) * mm});
            skLineSegment(sketch, "E8.6.4.9", {"start": v(-3.8, 124.4) * mm, "end": v(-3.8, 110.4) * mm});
            skLineSegment(sketch, "E8.9.4.9", {"start": v(-17.8, 124.4) * mm, "end": v(-17.8, 110.4) * mm});
            skLineSegment(sketch, "E8.0.4.10", {"start": v(-17.8, 138.4) * mm, "end": v(-3.8, 138.4) * mm});
            skLineSegment(sketch, "E8.3.4.10", {"start": v(-17.8, 152.4) * mm, "end": v(-3.8, 152.4) * mm});
            skLineSegment(sketch, "E8.6.4.10", {"start": v(-3.8, 152.4) * mm, "end": v(-3.8, 138.4) * mm});
            skLineSegment(sketch, "E8.9.4.10", {"start": v(-17.8, 152.4) * mm, "end": v(-17.8, 138.4) * mm});
            skLineSegment(sketch, "E8.0.5.0", {"start": v(-45.8, -141.6) * mm, "end": v(-31.8, -141.6) * mm});
            skLineSegment(sketch, "E8.3.5.0", {"start": v(-45.8, -127.6) * mm, "end": v(-31.8, -127.6) * mm});
            skLineSegment(sketch, "E8.6.5.0", {"start": v(-31.8, -127.6) * mm, "end": v(-31.8, -141.6) * mm});
            skLineSegment(sketch, "E8.9.5.0", {"start": v(-45.8, -127.6) * mm, "end": v(-45.8, -141.6) * mm});
            skLineSegment(sketch, "E8.0.5.1", {"start": v(-45.8, -113.6) * mm, "end": v(-31.8, -113.6) * mm});
            skLineSegment(sketch, "E8.3.5.1", {"start": v(-45.8, -99.6) * mm, "end": v(-31.8, -99.6) * mm});
            skLineSegment(sketch, "E8.6.5.1", {"start": v(-31.8, -99.6) * mm, "end": v(-31.8, -113.6) * mm});
            skLineSegment(sketch, "E8.9.5.1", {"start": v(-45.8, -99.6) * mm, "end": v(-45.8, -113.6) * mm});
            skLineSegment(sketch, "E8.0.5.2", {"start": v(-45.8, -85.6) * mm, "end": v(-31.8, -85.6) * mm});
            skLineSegment(sketch, "E8.3.5.2", {"start": v(-45.8, -71.6) * mm, "end": v(-31.8, -71.6) * mm});
            skLineSegment(sketch, "E8.6.5.2", {"start": v(-31.8, -71.6) * mm, "end": v(-31.8, -85.6) * mm});
            skLineSegment(sketch, "E8.9.5.2", {"start": v(-45.8, -71.6) * mm, "end": v(-45.8, -85.6) * mm});
            skLineSegment(sketch, "E8.0.5.3", {"start": v(-45.8, -57.6) * mm, "end": v(-31.8, -57.6) * mm});
            skLineSegment(sketch, "E8.3.5.3", {"start": v(-45.8, -43.6) * mm, "end": v(-31.8, -43.6) * mm});
            skLineSegment(sketch, "E8.6.5.3", {"start": v(-31.8, -43.6) * mm, "end": v(-31.8, -57.6) * mm});
            skLineSegment(sketch, "E8.9.5.3", {"start": v(-45.8, -43.6) * mm, "end": v(-45.8, -57.6) * mm});
            skLineSegment(sketch, "E8.0.5.4", {"start": v(-45.8, -29.6) * mm, "end": v(-31.8, -29.6) * mm});
            skLineSegment(sketch, "E8.3.5.4", {"start": v(-45.8, -15.6) * mm, "end": v(-31.8, -15.6) * mm});
            skLineSegment(sketch, "E8.6.5.4", {"start": v(-31.8, -15.6) * mm, "end": v(-31.8, -29.6) * mm});
            skLineSegment(sketch, "E8.9.5.4", {"start": v(-45.8, -15.6) * mm, "end": v(-45.8, -29.6) * mm});
            skLineSegment(sketch, "E8.0.5.5", {"start": v(-45.8, -1.6) * mm, "end": v(-31.8, -1.6) * mm});
            skLineSegment(sketch, "E8.3.5.5", {"start": v(-45.8, 12.4) * mm, "end": v(-31.8, 12.4) * mm});
            skLineSegment(sketch, "E8.6.5.5", {"start": v(-31.8, 12.4) * mm, "end": v(-31.8, -1.6) * mm});
            skLineSegment(sketch, "E8.9.5.5", {"start": v(-45.8, 12.4) * mm, "end": v(-45.8, -1.6) * mm});
            skLineSegment(sketch, "E8.0.5.6", {"start": v(-45.8, 26.4) * mm, "end": v(-31.8, 26.4) * mm});
            skLineSegment(sketch, "E8.3.5.6", {"start": v(-45.8, 40.4) * mm, "end": v(-31.8, 40.4) * mm});
            skLineSegment(sketch, "E8.6.5.6", {"start": v(-31.8, 40.4) * mm, "end": v(-31.8, 26.4) * mm});
            skLineSegment(sketch, "E8.9.5.6", {"start": v(-45.8, 40.4) * mm, "end": v(-45.8, 26.4) * mm});
            skLineSegment(sketch, "E8.0.5.7", {"start": v(-45.8, 54.4) * mm, "end": v(-31.8, 54.4) * mm});
            skLineSegment(sketch, "E8.3.5.7", {"start": v(-45.8, 68.4) * mm, "end": v(-31.8, 68.4) * mm});
            skLineSegment(sketch, "E8.6.5.7", {"start": v(-31.8, 68.4) * mm, "end": v(-31.8, 54.4) * mm});
            skLineSegment(sketch, "E8.9.5.7", {"start": v(-45.8, 68.4) * mm, "end": v(-45.8, 54.4) * mm});
            skLineSegment(sketch, "E8.0.5.8", {"start": v(-45.8, 82.4) * mm, "end": v(-31.8, 82.4) * mm});
            skLineSegment(sketch, "E8.3.5.8", {"start": v(-45.8, 96.4) * mm, "end": v(-31.8, 96.4) * mm});
            skLineSegment(sketch, "E8.6.5.8", {"start": v(-31.8, 96.4) * mm, "end": v(-31.8, 82.4) * mm});
            skLineSegment(sketch, "E8.9.5.8", {"start": v(-45.8, 96.4) * mm, "end": v(-45.8, 82.4) * mm});
            skLineSegment(sketch, "E8.0.5.9", {"start": v(-45.8, 110.4) * mm, "end": v(-31.8, 110.4) * mm});
            skLineSegment(sketch, "E8.3.5.9", {"start": v(-45.8, 124.4) * mm, "end": v(-31.8, 124.4) * mm});
            skLineSegment(sketch, "E8.6.5.9", {"start": v(-31.8, 124.4) * mm, "end": v(-31.8, 110.4) * mm});
            skLineSegment(sketch, "E8.9.5.9", {"start": v(-45.8, 124.4) * mm, "end": v(-45.8, 110.4) * mm});
            skLineSegment(sketch, "E8.0.5.10", {"start": v(-45.8, 138.4) * mm, "end": v(-31.8, 138.4) * mm});
            skLineSegment(sketch, "E8.3.5.10", {"start": v(-45.8, 152.4) * mm, "end": v(-31.8, 152.4) * mm});
            skLineSegment(sketch, "E8.6.5.10", {"start": v(-31.8, 152.4) * mm, "end": v(-31.8, 138.4) * mm});
            skLineSegment(sketch, "E8.9.5.10", {"start": v(-45.8, 152.4) * mm, "end": v(-45.8, 138.4) * mm});
            skLineSegment(sketch, "E8.0.6.0", {"start": v(-73.8, -141.6) * mm, "end": v(-59.8, -141.6) * mm});
            skLineSegment(sketch, "E8.3.6.0", {"start": v(-73.8, -127.6) * mm, "end": v(-59.8, -127.6) * mm});
            skLineSegment(sketch, "E8.6.6.0", {"start": v(-59.8, -127.6) * mm, "end": v(-59.8, -141.6) * mm});
            skLineSegment(sketch, "E8.9.6.0", {"start": v(-73.8, -127.6) * mm, "end": v(-73.8, -141.6) * mm});
            skLineSegment(sketch, "E8.0.6.1", {"start": v(-73.8, -113.6) * mm, "end": v(-59.8, -113.6) * mm});
            skLineSegment(sketch, "E8.3.6.1", {"start": v(-73.8, -99.6) * mm, "end": v(-59.8, -99.6) * mm});
            skLineSegment(sketch, "E8.6.6.1", {"start": v(-59.8, -99.6) * mm, "end": v(-59.8, -113.6) * mm});
            skLineSegment(sketch, "E8.9.6.1", {"start": v(-73.8, -99.6) * mm, "end": v(-73.8, -113.6) * mm});
            skLineSegment(sketch, "E8.0.6.2", {"start": v(-73.8, -85.6) * mm, "end": v(-59.8, -85.6) * mm});
            skLineSegment(sketch, "E8.3.6.2", {"start": v(-73.8, -71.6) * mm, "end": v(-59.8, -71.6) * mm});
            skLineSegment(sketch, "E8.6.6.2", {"start": v(-59.8, -71.6) * mm, "end": v(-59.8, -85.6) * mm});
            skLineSegment(sketch, "E8.9.6.2", {"start": v(-73.8, -71.6) * mm, "end": v(-73.8, -85.6) * mm});
            skLineSegment(sketch, "E8.0.6.3", {"start": v(-73.8, -57.6) * mm, "end": v(-59.8, -57.6) * mm});
            skLineSegment(sketch, "E8.3.6.3", {"start": v(-73.8, -43.6) * mm, "end": v(-59.8, -43.6) * mm});
            skLineSegment(sketch, "E8.6.6.3", {"start": v(-59.8, -43.6) * mm, "end": v(-59.8, -57.6) * mm});
            skLineSegment(sketch, "E8.9.6.3", {"start": v(-73.8, -43.6) * mm, "end": v(-73.8, -57.6) * mm});
            skLineSegment(sketch, "E8.0.6.4", {"start": v(-73.8, -29.6) * mm, "end": v(-59.8, -29.6) * mm});
            skLineSegment(sketch, "E8.3.6.4", {"start": v(-73.8, -15.6) * mm, "end": v(-59.8, -15.6) * mm});
            skLineSegment(sketch, "E8.6.6.4", {"start": v(-59.8, -15.6) * mm, "end": v(-59.8, -29.6) * mm});
            skLineSegment(sketch, "E8.9.6.4", {"start": v(-73.8, -15.6) * mm, "end": v(-73.8, -29.6) * mm});
            skLineSegment(sketch, "E8.0.6.5", {"start": v(-73.8, -1.6) * mm, "end": v(-59.8, -1.6) * mm});
            skLineSegment(sketch, "E8.3.6.5", {"start": v(-73.8, 12.4) * mm, "end": v(-59.8, 12.4) * mm});
            skLineSegment(sketch, "E8.6.6.5", {"start": v(-59.8, 12.4) * mm, "end": v(-59.8, -1.6) * mm});
            skLineSegment(sketch, "E8.9.6.5", {"start": v(-73.8, 12.4) * mm, "end": v(-73.8, -1.6) * mm});
            skLineSegment(sketch, "E8.0.6.6", {"start": v(-73.8, 26.4) * mm, "end": v(-59.8, 26.4) * mm});
            skLineSegment(sketch, "E8.3.6.6", {"start": v(-73.8, 40.4) * mm, "end": v(-59.8, 40.4) * mm});
            skLineSegment(sketch, "E8.6.6.6", {"start": v(-59.8, 40.4) * mm, "end": v(-59.8, 26.4) * mm});
            skLineSegment(sketch, "E8.9.6.6", {"start": v(-73.8, 40.4) * mm, "end": v(-73.8, 26.4) * mm});
            skLineSegment(sketch, "E8.0.6.7", {"start": v(-73.8, 54.4) * mm, "end": v(-59.8, 54.4) * mm});
            skLineSegment(sketch, "E8.3.6.7", {"start": v(-73.8, 68.4) * mm, "end": v(-59.8, 68.4) * mm});
            skLineSegment(sketch, "E8.6.6.7", {"start": v(-59.8, 68.4) * mm, "end": v(-59.8, 54.4) * mm});
            skLineSegment(sketch, "E8.9.6.7", {"start": v(-73.8, 68.4) * mm, "end": v(-73.8, 54.4) * mm});
            skLineSegment(sketch, "E8.0.6.8", {"start": v(-73.8, 82.4) * mm, "end": v(-59.8, 82.4) * mm});
            skLineSegment(sketch, "E8.3.6.8", {"start": v(-73.8, 96.4) * mm, "end": v(-59.8, 96.4) * mm});
            skLineSegment(sketch, "E8.6.6.8", {"start": v(-59.8, 96.4) * mm, "end": v(-59.8, 82.4) * mm});
            skLineSegment(sketch, "E8.9.6.8", {"start": v(-73.8, 96.4) * mm, "end": v(-73.8, 82.4) * mm});
            skLineSegment(sketch, "E8.0.6.9", {"start": v(-73.8, 110.4) * mm, "end": v(-59.8, 110.4) * mm});
            skLineSegment(sketch, "E8.3.6.9", {"start": v(-73.8, 124.4) * mm, "end": v(-59.8, 124.4) * mm});
            skLineSegment(sketch, "E8.6.6.9", {"start": v(-59.8, 124.4) * mm, "end": v(-59.8, 110.4) * mm});
            skLineSegment(sketch, "E8.9.6.9", {"start": v(-73.8, 124.4) * mm, "end": v(-73.8, 110.4) * mm});
            skLineSegment(sketch, "E8.0.6.10", {"start": v(-73.8, 138.4) * mm, "end": v(-59.8, 138.4) * mm});
            skLineSegment(sketch, "E8.3.6.10", {"start": v(-73.8, 152.4) * mm, "end": v(-59.8, 152.4) * mm});
            skLineSegment(sketch, "E8.6.6.10", {"start": v(-59.8, 152.4) * mm, "end": v(-59.8, 138.4) * mm});
            skLineSegment(sketch, "E8.9.6.10", {"start": v(-73.8, 152.4) * mm, "end": v(-73.8, 138.4) * mm});
            skLineSegment(sketch, "E8.0.7.0", {"start": v(-101.8, -141.6) * mm, "end": v(-87.8, -141.6) * mm});
            skLineSegment(sketch, "E8.3.7.0", {"start": v(-101.8, -127.6) * mm, "end": v(-87.8, -127.6) * mm});
            skLineSegment(sketch, "E8.6.7.0", {"start": v(-87.8, -127.6) * mm, "end": v(-87.8, -141.6) * mm});
            skLineSegment(sketch, "E8.9.7.0", {"start": v(-101.8, -127.6) * mm, "end": v(-101.8, -141.6) * mm});
            skLineSegment(sketch, "E8.0.7.1", {"start": v(-101.8, -113.6) * mm, "end": v(-87.8, -113.6) * mm});
            skLineSegment(sketch, "E8.3.7.1", {"start": v(-101.8, -99.6) * mm, "end": v(-87.8, -99.6) * mm});
            skLineSegment(sketch, "E8.6.7.1", {"start": v(-87.8, -99.6) * mm, "end": v(-87.8, -113.6) * mm});
            skLineSegment(sketch, "E8.9.7.1", {"start": v(-101.8, -99.6) * mm, "end": v(-101.8, -113.6) * mm});
            skLineSegment(sketch, "E8.0.7.2", {"start": v(-101.8, -85.6) * mm, "end": v(-87.8, -85.6) * mm});
            skLineSegment(sketch, "E8.3.7.2", {"start": v(-101.8, -71.6) * mm, "end": v(-87.8, -71.6) * mm});
            skLineSegment(sketch, "E8.6.7.2", {"start": v(-87.8, -71.6) * mm, "end": v(-87.8, -85.6) * mm});
            skLineSegment(sketch, "E8.9.7.2", {"start": v(-101.8, -71.6) * mm, "end": v(-101.8, -85.6) * mm});
            skLineSegment(sketch, "E8.0.7.3", {"start": v(-101.8, -57.6) * mm, "end": v(-87.8, -57.6) * mm});
            skLineSegment(sketch, "E8.3.7.3", {"start": v(-101.8, -43.6) * mm, "end": v(-87.8, -43.6) * mm});
            skLineSegment(sketch, "E8.6.7.3", {"start": v(-87.8, -43.6) * mm, "end": v(-87.8, -57.6) * mm});
            skLineSegment(sketch, "E8.9.7.3", {"start": v(-101.8, -43.6) * mm, "end": v(-101.8, -57.6) * mm});
            skLineSegment(sketch, "E8.0.7.4", {"start": v(-101.8, -29.6) * mm, "end": v(-87.8, -29.6) * mm});
            skLineSegment(sketch, "E8.3.7.4", {"start": v(-101.8, -15.6) * mm, "end": v(-87.8, -15.6) * mm});
            skLineSegment(sketch, "E8.6.7.4", {"start": v(-87.8, -15.6) * mm, "end": v(-87.8, -29.6) * mm});
            skLineSegment(sketch, "E8.9.7.4", {"start": v(-101.8, -15.6) * mm, "end": v(-101.8, -29.6) * mm});
            skLineSegment(sketch, "E8.0.7.5", {"start": v(-101.8, -1.6) * mm, "end": v(-87.8, -1.6) * mm});
            skLineSegment(sketch, "E8.3.7.5", {"start": v(-101.8, 12.4) * mm, "end": v(-87.8, 12.4) * mm});
            skLineSegment(sketch, "E8.6.7.5", {"start": v(-87.8, 12.4) * mm, "end": v(-87.8, -1.6) * mm});
            skLineSegment(sketch, "E8.9.7.5", {"start": v(-101.8, 12.4) * mm, "end": v(-101.8, -1.6) * mm});
            skLineSegment(sketch, "E8.0.7.6", {"start": v(-101.8, 26.4) * mm, "end": v(-87.8, 26.4) * mm});
            skLineSegment(sketch, "E8.3.7.6", {"start": v(-101.8, 40.4) * mm, "end": v(-87.8, 40.4) * mm});
            skLineSegment(sketch, "E8.6.7.6", {"start": v(-87.8, 40.4) * mm, "end": v(-87.8, 26.4) * mm});
            skLineSegment(sketch, "E8.9.7.6", {"start": v(-101.8, 40.4) * mm, "end": v(-101.8, 26.4) * mm});
            skLineSegment(sketch, "E8.0.7.7", {"start": v(-101.8, 54.4) * mm, "end": v(-87.8, 54.4) * mm});
            skLineSegment(sketch, "E8.3.7.7", {"start": v(-101.8, 68.4) * mm, "end": v(-87.8, 68.4) * mm});
            skLineSegment(sketch, "E8.6.7.7", {"start": v(-87.8, 68.4) * mm, "end": v(-87.8, 54.4) * mm});
            skLineSegment(sketch, "E8.9.7.7", {"start": v(-101.8, 68.4) * mm, "end": v(-101.8, 54.4) * mm});
            skLineSegment(sketch, "E8.0.7.8", {"start": v(-101.8, 82.4) * mm, "end": v(-87.8, 82.4) * mm});
            skLineSegment(sketch, "E8.3.7.8", {"start": v(-101.8, 96.4) * mm, "end": v(-87.8, 96.4) * mm});
            skLineSegment(sketch, "E8.6.7.8", {"start": v(-87.8, 96.4) * mm, "end": v(-87.8, 82.4) * mm});
            skLineSegment(sketch, "E8.9.7.8", {"start": v(-101.8, 96.4) * mm, "end": v(-101.8, 82.4) * mm});
            skLineSegment(sketch, "E8.0.7.9", {"start": v(-101.8, 110.4) * mm, "end": v(-87.8, 110.4) * mm});
            skLineSegment(sketch, "E8.3.7.9", {"start": v(-101.8, 124.4) * mm, "end": v(-87.8, 124.4) * mm});
            skLineSegment(sketch, "E8.6.7.9", {"start": v(-87.8, 124.4) * mm, "end": v(-87.8, 110.4) * mm});
            skLineSegment(sketch, "E8.9.7.9", {"start": v(-101.8, 124.4) * mm, "end": v(-101.8, 110.4) * mm});
            skLineSegment(sketch, "E8.0.7.10", {"start": v(-101.8, 138.4) * mm, "end": v(-87.8, 138.4) * mm});
            skLineSegment(sketch, "E8.3.7.10", {"start": v(-101.8, 152.4) * mm, "end": v(-87.8, 152.4) * mm});
            skLineSegment(sketch, "E8.6.7.10", {"start": v(-87.8, 152.4) * mm, "end": v(-87.8, 138.4) * mm});
            skLineSegment(sketch, "E8.9.7.10", {"start": v(-101.8, 152.4) * mm, "end": v(-101.8, 138.4) * mm});
            skSolve(sketch);
        }
        {
            var Q0;
            Q0=makeQuery(id+"F0.imprint","IMPRINT",FACE,{"disambiguationData":[TD([[makeQuery(id+"F0.imprint","IMPRINT",EDGE,{"derivedFrom":sQuery(id+"F0.wireOp",EDGE,"E0.bottom")}),-1.0]])]});
            var sketch = newSketch(context, id + "F2", { "sketchPlane" : qUnion([Q0])});
            skLineSegment(sketch, "E9.bottom", {"start": v(-102.3, -141.6) * mm, "end": v(-88.3, -141.6) * mm});
            skLineSegment(sketch, "E9.top", {"start": v(-102.3, -155.6) * mm, "end": v(-88.3, -155.6) * mm});
            skLineSegment(sketch, "E9.left", {"start": v(-102.3, -141.6) * mm, "end": v(-102.3, -155.6) * mm});
            skLineSegment(sketch, "E9.right", {"start": v(-88.3, -141.6) * mm, "end": v(-88.3, -155.6) * mm});
            skLineSegment(sketch, "E10.direction1", {"start": v(-102.3, -155.6) * mm, "end": v(-74.3, -155.6) * mm, "construction": true});
            skLineSegment(sketch, "E10.direction2", {"start": v(-102.3, -155.6) * mm, "end": v(-102.3, -127.6) * mm, "construction": true});
            skLineSegment(sketch, "E11.bottom", {"start": v(105, -147.5) * mm, "end": v(119, -147.5) * mm});
            skLineSegment(sketch, "E11.top", {"start": v(105, -133.5) * mm, "end": v(119, -133.5) * mm});
            skLineSegment(sketch, "E11.left", {"start": v(105, -147.5) * mm, "end": v(105, -133.5) * mm});
            skLineSegment(sketch, "E11.right", {"start": v(119, -147.5) * mm, "end": v(119, -133.5) * mm});
            skLineSegment(sketch, "E12.direction1", {"start": v(105, -147.5) * mm, "end": v(77, -147.5) * mm, "construction": true});
            skLineSegment(sketch, "E12.direction2", {"start": v(105, -147.5) * mm, "end": v(105, -119.5) * mm, "construction": true});
            skLineSegment(sketch, "E13.0.1.0", {"start": v(-74.3, -155.6) * mm, "end": v(-60.3, -155.6) * mm});
            skLineSegment(sketch, "E13.3.1.0", {"start": v(-60.3, -141.6) * mm, "end": v(-60.3, -155.6) * mm});
            skLineSegment(sketch, "E13.6.1.0", {"start": v(-74.3, -141.6) * mm, "end": v(-74.3, -155.6) * mm});
            skLineSegment(sketch, "E13.9.1.0", {"start": v(-74.3, -141.6) * mm, "end": v(-60.3, -141.6) * mm});
            skLineSegment(sketch, "E13.0.2.0", {"start": v(-46.3, -155.6) * mm, "end": v(-32.3, -155.6) * mm});
            skLineSegment(sketch, "E13.3.2.0", {"start": v(-32.3, -141.6) * mm, "end": v(-32.3, -155.6) * mm});
            skLineSegment(sketch, "E13.6.2.0", {"start": v(-46.3, -141.6) * mm, "end": v(-46.3, -155.6) * mm});
            skLineSegment(sketch, "E13.9.2.0", {"start": v(-46.3, -141.6) * mm, "end": v(-32.3, -141.6) * mm});
            skLineSegment(sketch, "E13.0.3.0", {"start": v(-18.3, -155.6) * mm, "end": v(-4.3, -155.6) * mm});
            skLineSegment(sketch, "E13.3.3.0", {"start": v(-4.3, -141.6) * mm, "end": v(-4.3, -155.6) * mm});
            skLineSegment(sketch, "E13.6.3.0", {"start": v(-18.3, -141.6) * mm, "end": v(-18.3, -155.6) * mm});
            skLineSegment(sketch, "E13.9.3.0", {"start": v(-18.3, -141.6) * mm, "end": v(-4.3, -141.6) * mm});
            skLineSegment(sketch, "E13.0.4.0", {"start": v(9.7, -155.6) * mm, "end": v(23.7, -155.6) * mm});
            skLineSegment(sketch, "E13.3.4.0", {"start": v(23.7, -141.6) * mm, "end": v(23.7, -155.6) * mm});
            skLineSegment(sketch, "E13.6.4.0", {"start": v(9.7, -141.6) * mm, "end": v(9.7, -155.6) * mm});
            skLineSegment(sketch, "E13.9.4.0", {"start": v(9.7, -141.6) * mm, "end": v(23.7, -141.6) * mm});
            skLineSegment(sketch, "E13.0.5.0", {"start": v(37.7, -155.6) * mm, "end": v(51.7, -155.6) * mm});
            skLineSegment(sketch, "E13.3.5.0", {"start": v(51.7, -141.6) * mm, "end": v(51.7, -155.6) * mm});
            skLineSegment(sketch, "E13.6.5.0", {"start": v(37.7, -141.6) * mm, "end": v(37.7, -155.6) * mm});
            skLineSegment(sketch, "E13.9.5.0", {"start": v(37.7, -141.6) * mm, "end": v(51.7, -141.6) * mm});
            skLineSegment(sketch, "E13.0.6.0", {"start": v(65.7, -155.6) * mm, "end": v(79.7, -155.6) * mm});
            skLineSegment(sketch, "E13.3.6.0", {"start": v(79.7, -141.6) * mm, "end": v(79.7, -155.6) * mm});
            skLineSegment(sketch, "E13.6.6.0", {"start": v(65.7, -141.6) * mm, "end": v(65.7, -155.6) * mm});
            skLineSegment(sketch, "E13.9.6.0", {"start": v(65.7, -141.6) * mm, "end": v(79.7, -141.6) * mm});
            skLineSegment(sketch, "E13.0.7.0", {"start": v(93.7, -155.6) * mm, "end": v(107.7, -155.6) * mm});
            skLineSegment(sketch, "E13.3.7.0", {"start": v(107.7, -141.6) * mm, "end": v(107.7, -155.6) * mm});
            skLineSegment(sketch, "E13.6.7.0", {"start": v(93.7, -141.6) * mm, "end": v(93.7, -155.6) * mm});
            skLineSegment(sketch, "E13.9.7.0", {"start": v(93.7, -141.6) * mm, "end": v(107.7, -141.6) * mm});
            skLineSegment(sketch, "E14.0.0.1", {"start": v(-102.3, -127.6) * mm, "end": v(-88.3, -127.6) * mm});
            skLineSegment(sketch, "E14.3.0.1", {"start": v(-88.3, -113.6) * mm, "end": v(-88.3, -127.6) * mm});
            skLineSegment(sketch, "E14.6.0.1", {"start": v(-102.3, -113.6) * mm, "end": v(-102.3, -127.6) * mm});
            skLineSegment(sketch, "E14.9.0.1", {"start": v(-102.3, -113.6) * mm, "end": v(-88.3, -113.6) * mm});
            skLineSegment(sketch, "E14.0.0.2", {"start": v(-102.3, -99.6) * mm, "end": v(-88.3, -99.6) * mm});
            skLineSegment(sketch, "E14.3.0.2", {"start": v(-88.3, -85.6) * mm, "end": v(-88.3, -99.6) * mm});
            skLineSegment(sketch, "E14.6.0.2", {"start": v(-102.3, -85.6) * mm, "end": v(-102.3, -99.6) * mm});
            skLineSegment(sketch, "E14.9.0.2", {"start": v(-102.3, -85.6) * mm, "end": v(-88.3, -85.6) * mm});
            skLineSegment(sketch, "E14.0.0.3", {"start": v(-102.3, -71.6) * mm, "end": v(-88.3, -71.6) * mm});
            skLineSegment(sketch, "E14.3.0.3", {"start": v(-88.3, -57.6) * mm, "end": v(-88.3, -71.6) * mm});
            skLineSegment(sketch, "E14.6.0.3", {"start": v(-102.3, -57.6) * mm, "end": v(-102.3, -71.6) * mm});
            skLineSegment(sketch, "E14.9.0.3", {"start": v(-102.3, -57.6) * mm, "end": v(-88.3, -57.6) * mm});
            skLineSegment(sketch, "E14.0.0.4", {"start": v(-102.3, -43.6) * mm, "end": v(-88.3, -43.6) * mm});
            skLineSegment(sketch, "E14.3.0.4", {"start": v(-88.3, -29.6) * mm, "end": v(-88.3, -43.6) * mm});
            skLineSegment(sketch, "E14.6.0.4", {"start": v(-102.3, -29.6) * mm, "end": v(-102.3, -43.6) * mm});
            skLineSegment(sketch, "E14.9.0.4", {"start": v(-102.3, -29.6) * mm, "end": v(-88.3, -29.6) * mm});
            skLineSegment(sketch, "E14.0.0.5", {"start": v(-102.3, -15.6) * mm, "end": v(-88.3, -15.6) * mm});
            skLineSegment(sketch, "E14.3.0.5", {"start": v(-88.3, -1.6) * mm, "end": v(-88.3, -15.6) * mm});
            skLineSegment(sketch, "E14.6.0.5", {"start": v(-102.3, -1.6) * mm, "end": v(-102.3, -15.6) * mm});
            skLineSegment(sketch, "E14.9.0.5", {"start": v(-102.3, -1.6) * mm, "end": v(-88.3, -1.6) * mm});
            skLineSegment(sketch, "E14.0.0.6", {"start": v(-102.3, 12.4) * mm, "end": v(-88.3, 12.4) * mm});
            skLineSegment(sketch, "E14.3.0.6", {"start": v(-88.3, 26.4) * mm, "end": v(-88.3, 12.4) * mm});
            skLineSegment(sketch, "E14.6.0.6", {"start": v(-102.3, 26.4) * mm, "end": v(-102.3, 12.4) * mm});
            skLineSegment(sketch, "E14.9.0.6", {"start": v(-102.3, 26.4) * mm, "end": v(-88.3, 26.4) * mm});
            skLineSegment(sketch, "E14.0.0.7", {"start": v(-102.3, 40.4) * mm, "end": v(-88.3, 40.4) * mm});
            skLineSegment(sketch, "E14.3.0.7", {"start": v(-88.3, 54.4) * mm, "end": v(-88.3, 40.4) * mm});
            skLineSegment(sketch, "E14.6.0.7", {"start": v(-102.3, 54.4) * mm, "end": v(-102.3, 40.4) * mm});
            skLineSegment(sketch, "E14.9.0.7", {"start": v(-102.3, 54.4) * mm, "end": v(-88.3, 54.4) * mm});
            skLineSegment(sketch, "E14.0.0.8", {"start": v(-102.3, 68.4) * mm, "end": v(-88.3, 68.4) * mm});
            skLineSegment(sketch, "E14.3.0.8", {"start": v(-88.3, 82.4) * mm, "end": v(-88.3, 68.4) * mm});
            skLineSegment(sketch, "E14.6.0.8", {"start": v(-102.3, 82.4) * mm, "end": v(-102.3, 68.4) * mm});
            skLineSegment(sketch, "E14.9.0.8", {"start": v(-102.3, 82.4) * mm, "end": v(-88.3, 82.4) * mm});
            skLineSegment(sketch, "E14.0.0.9", {"start": v(-102.3, 96.4) * mm, "end": v(-88.3, 96.4) * mm});
            skLineSegment(sketch, "E14.3.0.9", {"start": v(-88.3, 110.4) * mm, "end": v(-88.3, 96.4) * mm});
            skLineSegment(sketch, "E14.6.0.9", {"start": v(-102.3, 110.4) * mm, "end": v(-102.3, 96.4) * mm});
            skLineSegment(sketch, "E14.9.0.9", {"start": v(-102.3, 110.4) * mm, "end": v(-88.3, 110.4) * mm});
            skLineSegment(sketch, "E14.0.0.10", {"start": v(-102.3, 124.4) * mm, "end": v(-88.3, 124.4) * mm});
            skLineSegment(sketch, "E14.3.0.10", {"start": v(-88.3, 138.4) * mm, "end": v(-88.3, 124.4) * mm});
            skLineSegment(sketch, "E14.6.0.10", {"start": v(-102.3, 138.4) * mm, "end": v(-102.3, 124.4) * mm});
            skLineSegment(sketch, "E14.9.0.10", {"start": v(-102.3, 138.4) * mm, "end": v(-88.3, 138.4) * mm});
            skLineSegment(sketch, "E14.0.0.11", {"start": v(-102.3, 152.4) * mm, "end": v(-88.3, 152.4) * mm});
            skLineSegment(sketch, "E14.3.0.11", {"start": v(-88.3, 166.4) * mm, "end": v(-88.3, 152.4) * mm});
            skLineSegment(sketch, "E14.6.0.11", {"start": v(-102.3, 166.4) * mm, "end": v(-102.3, 152.4) * mm});
            skLineSegment(sketch, "E14.9.0.11", {"start": v(-102.3, 166.4) * mm, "end": v(-88.3, 166.4) * mm});
            skLineSegment(sketch, "E14.0.1.1", {"start": v(-74.3, -127.6) * mm, "end": v(-60.3, -127.6) * mm});
            skLineSegment(sketch, "E14.3.1.1", {"start": v(-60.3, -113.6) * mm, "end": v(-60.3, -127.6) * mm});
            skLineSegment(sketch, "E14.6.1.1", {"start": v(-74.3, -113.6) * mm, "end": v(-74.3, -127.6) * mm});
            skLineSegment(sketch, "E14.9.1.1", {"start": v(-74.3, -113.6) * mm, "end": v(-60.3, -113.6) * mm});
            skLineSegment(sketch, "E14.0.1.2", {"start": v(-74.3, -99.6) * mm, "end": v(-60.3, -99.6) * mm});
            skLineSegment(sketch, "E14.3.1.2", {"start": v(-60.3, -85.6) * mm, "end": v(-60.3, -99.6) * mm});
            skLineSegment(sketch, "E14.6.1.2", {"start": v(-74.3, -85.6) * mm, "end": v(-74.3, -99.6) * mm});
            skLineSegment(sketch, "E14.9.1.2", {"start": v(-74.3, -85.6) * mm, "end": v(-60.3, -85.6) * mm});
            skLineSegment(sketch, "E14.0.1.3", {"start": v(-74.3, -71.6) * mm, "end": v(-60.3, -71.6) * mm});
            skLineSegment(sketch, "E14.3.1.3", {"start": v(-60.3, -57.6) * mm, "end": v(-60.3, -71.6) * mm});
            skLineSegment(sketch, "E14.6.1.3", {"start": v(-74.3, -57.6) * mm, "end": v(-74.3, -71.6) * mm});
            skLineSegment(sketch, "E14.9.1.3", {"start": v(-74.3, -57.6) * mm, "end": v(-60.3, -57.6) * mm});
            skLineSegment(sketch, "E14.0.1.4", {"start": v(-74.3, -43.6) * mm, "end": v(-60.3, -43.6) * mm});
            skLineSegment(sketch, "E14.3.1.4", {"start": v(-60.3, -29.6) * mm, "end": v(-60.3, -43.6) * mm});
            skLineSegment(sketch, "E14.6.1.4", {"start": v(-74.3, -29.6) * mm, "end": v(-74.3, -43.6) * mm});
            skLineSegment(sketch, "E14.9.1.4", {"start": v(-74.3, -29.6) * mm, "end": v(-60.3, -29.6) * mm});
            skLineSegment(sketch, "E14.0.1.5", {"start": v(-74.3, -15.6) * mm, "end": v(-60.3, -15.6) * mm});
            skLineSegment(sketch, "E14.3.1.5", {"start": v(-60.3, -1.6) * mm, "end": v(-60.3, -15.6) * mm});
            skLineSegment(sketch, "E14.6.1.5", {"start": v(-74.3, -1.6) * mm, "end": v(-74.3, -15.6) * mm});
            skLineSegment(sketch, "E14.9.1.5", {"start": v(-74.3, -1.6) * mm, "end": v(-60.3, -1.6) * mm});
            skLineSegment(sketch, "E14.0.1.6", {"start": v(-74.3, 12.4) * mm, "end": v(-60.3, 12.4) * mm});
            skLineSegment(sketch, "E14.3.1.6", {"start": v(-60.3, 26.4) * mm, "end": v(-60.3, 12.4) * mm});
            skLineSegment(sketch, "E14.6.1.6", {"start": v(-74.3, 26.4) * mm, "end": v(-74.3, 12.4) * mm});
            skLineSegment(sketch, "E14.9.1.6", {"start": v(-74.3, 26.4) * mm, "end": v(-60.3, 26.4) * mm});
            skLineSegment(sketch, "E14.0.1.7", {"start": v(-74.3, 40.4) * mm, "end": v(-60.3, 40.4) * mm});
            skLineSegment(sketch, "E14.3.1.7", {"start": v(-60.3, 54.4) * mm, "end": v(-60.3, 40.4) * mm});
            skLineSegment(sketch, "E14.6.1.7", {"start": v(-74.3, 54.4) * mm, "end": v(-74.3, 40.4) * mm});
            skLineSegment(sketch, "E14.9.1.7", {"start": v(-74.3, 54.4) * mm, "end": v(-60.3, 54.4) * mm});
            skLineSegment(sketch, "E14.0.1.8", {"start": v(-74.3, 68.4) * mm, "end": v(-60.3, 68.4) * mm});
            skLineSegment(sketch, "E14.3.1.8", {"start": v(-60.3, 82.4) * mm, "end": v(-60.3, 68.4) * mm});
            skLineSegment(sketch, "E14.6.1.8", {"start": v(-74.3, 82.4) * mm, "end": v(-74.3, 68.4) * mm});
            skLineSegment(sketch, "E14.9.1.8", {"start": v(-74.3, 82.4) * mm, "end": v(-60.3, 82.4) * mm});
            skLineSegment(sketch, "E14.0.1.9", {"start": v(-74.3, 96.4) * mm, "end": v(-60.3, 96.4) * mm});
            skLineSegment(sketch, "E14.3.1.9", {"start": v(-60.3, 110.4) * mm, "end": v(-60.3, 96.4) * mm});
            skLineSegment(sketch, "E14.6.1.9", {"start": v(-74.3, 110.4) * mm, "end": v(-74.3, 96.4) * mm});
            skLineSegment(sketch, "E14.9.1.9", {"start": v(-74.3, 110.4) * mm, "end": v(-60.3, 110.4) * mm});
            skLineSegment(sketch, "E14.0.1.10", {"start": v(-74.3, 124.4) * mm, "end": v(-60.3, 124.4) * mm});
            skLineSegment(sketch, "E14.3.1.10", {"start": v(-60.3, 138.4) * mm, "end": v(-60.3, 124.4) * mm});
            skLineSegment(sketch, "E14.6.1.10", {"start": v(-74.3, 138.4) * mm, "end": v(-74.3, 124.4) * mm});
            skLineSegment(sketch, "E14.9.1.10", {"start": v(-74.3, 138.4) * mm, "end": v(-60.3, 138.4) * mm});
            skLineSegment(sketch, "E14.0.1.11", {"start": v(-74.3, 152.4) * mm, "end": v(-60.3, 152.4) * mm});
            skLineSegment(sketch, "E14.3.1.11", {"start": v(-60.3, 166.4) * mm, "end": v(-60.3, 152.4) * mm});
            skLineSegment(sketch, "E14.6.1.11", {"start": v(-74.3, 166.4) * mm, "end": v(-74.3, 152.4) * mm});
            skLineSegment(sketch, "E14.9.1.11", {"start": v(-74.3, 166.4) * mm, "end": v(-60.3, 166.4) * mm});
            skLineSegment(sketch, "E14.0.2.1", {"start": v(-46.3, -127.6) * mm, "end": v(-32.3, -127.6) * mm});
            skLineSegment(sketch, "E14.3.2.1", {"start": v(-32.3, -113.6) * mm, "end": v(-32.3, -127.6) * mm});
            skLineSegment(sketch, "E14.6.2.1", {"start": v(-46.3, -113.6) * mm, "end": v(-46.3, -127.6) * mm});
            skLineSegment(sketch, "E14.9.2.1", {"start": v(-46.3, -113.6) * mm, "end": v(-32.3, -113.6) * mm});
            skLineSegment(sketch, "E14.0.2.2", {"start": v(-46.3, -99.6) * mm, "end": v(-32.3, -99.6) * mm});
            skLineSegment(sketch, "E14.3.2.2", {"start": v(-32.3, -85.6) * mm, "end": v(-32.3, -99.6) * mm});
            skLineSegment(sketch, "E14.6.2.2", {"start": v(-46.3, -85.6) * mm, "end": v(-46.3, -99.6) * mm});
            skLineSegment(sketch, "E14.9.2.2", {"start": v(-46.3, -85.6) * mm, "end": v(-32.3, -85.6) * mm});
            skLineSegment(sketch, "E14.0.2.3", {"start": v(-46.3, -71.6) * mm, "end": v(-32.3, -71.6) * mm});
            skLineSegment(sketch, "E14.3.2.3", {"start": v(-32.3, -57.6) * mm, "end": v(-32.3, -71.6) * mm});
            skLineSegment(sketch, "E14.6.2.3", {"start": v(-46.3, -57.6) * mm, "end": v(-46.3, -71.6) * mm});
            skLineSegment(sketch, "E14.9.2.3", {"start": v(-46.3, -57.6) * mm, "end": v(-32.3, -57.6) * mm});
            skLineSegment(sketch, "E14.0.2.4", {"start": v(-46.3, -43.6) * mm, "end": v(-32.3, -43.6) * mm});
            skLineSegment(sketch, "E14.3.2.4", {"start": v(-32.3, -29.6) * mm, "end": v(-32.3, -43.6) * mm});
            skLineSegment(sketch, "E14.6.2.4", {"start": v(-46.3, -29.6) * mm, "end": v(-46.3, -43.6) * mm});
            skLineSegment(sketch, "E14.9.2.4", {"start": v(-46.3, -29.6) * mm, "end": v(-32.3, -29.6) * mm});
            skLineSegment(sketch, "E14.0.2.5", {"start": v(-46.3, -15.6) * mm, "end": v(-32.3, -15.6) * mm});
            skLineSegment(sketch, "E14.3.2.5", {"start": v(-32.3, -1.6) * mm, "end": v(-32.3, -15.6) * mm});
            skLineSegment(sketch, "E14.6.2.5", {"start": v(-46.3, -1.6) * mm, "end": v(-46.3, -15.6) * mm});
            skLineSegment(sketch, "E14.9.2.5", {"start": v(-46.3, -1.6) * mm, "end": v(-32.3, -1.6) * mm});
            skLineSegment(sketch, "E14.0.2.6", {"start": v(-46.3, 12.4) * mm, "end": v(-32.3, 12.4) * mm});
            skLineSegment(sketch, "E14.3.2.6", {"start": v(-32.3, 26.4) * mm, "end": v(-32.3, 12.4) * mm});
            skLineSegment(sketch, "E14.6.2.6", {"start": v(-46.3, 26.4) * mm, "end": v(-46.3, 12.4) * mm});
            skLineSegment(sketch, "E14.9.2.6", {"start": v(-46.3, 26.4) * mm, "end": v(-32.3, 26.4) * mm});
            skLineSegment(sketch, "E14.0.2.7", {"start": v(-46.3, 40.4) * mm, "end": v(-32.3, 40.4) * mm});
            skLineSegment(sketch, "E14.3.2.7", {"start": v(-32.3, 54.4) * mm, "end": v(-32.3, 40.4) * mm});
            skLineSegment(sketch, "E14.6.2.7", {"start": v(-46.3, 54.4) * mm, "end": v(-46.3, 40.4) * mm});
            skLineSegment(sketch, "E14.9.2.7", {"start": v(-46.3, 54.4) * mm, "end": v(-32.3, 54.4) * mm});
            skLineSegment(sketch, "E14.0.2.8", {"start": v(-46.3, 68.4) * mm, "end": v(-32.3, 68.4) * mm});
            skLineSegment(sketch, "E14.3.2.8", {"start": v(-32.3, 82.4) * mm, "end": v(-32.3, 68.4) * mm});
            skLineSegment(sketch, "E14.6.2.8", {"start": v(-46.3, 82.4) * mm, "end": v(-46.3, 68.4) * mm});
            skLineSegment(sketch, "E14.9.2.8", {"start": v(-46.3, 82.4) * mm, "end": v(-32.3, 82.4) * mm});
            skLineSegment(sketch, "E14.0.2.9", {"start": v(-46.3, 96.4) * mm, "end": v(-32.3, 96.4) * mm});
            skLineSegment(sketch, "E14.3.2.9", {"start": v(-32.3, 110.4) * mm, "end": v(-32.3, 96.4) * mm});
            skLineSegment(sketch, "E14.6.2.9", {"start": v(-46.3, 110.4) * mm, "end": v(-46.3, 96.4) * mm});
            skLineSegment(sketch, "E14.9.2.9", {"start": v(-46.3, 110.4) * mm, "end": v(-32.3, 110.4) * mm});
            skLineSegment(sketch, "E14.0.2.10", {"start": v(-46.3, 124.4) * mm, "end": v(-32.3, 124.4) * mm});
            skLineSegment(sketch, "E14.3.2.10", {"start": v(-32.3, 138.4) * mm, "end": v(-32.3, 124.4) * mm});
            skLineSegment(sketch, "E14.6.2.10", {"start": v(-46.3, 138.4) * mm, "end": v(-46.3, 124.4) * mm});
            skLineSegment(sketch, "E14.9.2.10", {"start": v(-46.3, 138.4) * mm, "end": v(-32.3, 138.4) * mm});
            skLineSegment(sketch, "E14.0.2.11", {"start": v(-46.3, 152.4) * mm, "end": v(-32.3, 152.4) * mm});
            skLineSegment(sketch, "E14.3.2.11", {"start": v(-32.3, 166.4) * mm, "end": v(-32.3, 152.4) * mm});
            skLineSegment(sketch, "E14.6.2.11", {"start": v(-46.3, 166.4) * mm, "end": v(-46.3, 152.4) * mm});
            skLineSegment(sketch, "E14.9.2.11", {"start": v(-46.3, 166.4) * mm, "end": v(-32.3, 166.4) * mm});
            skLineSegment(sketch, "E14.0.3.1", {"start": v(-18.3, -127.6) * mm, "end": v(-4.3, -127.6) * mm});
            skLineSegment(sketch, "E14.3.3.1", {"start": v(-4.3, -113.6) * mm, "end": v(-4.3, -127.6) * mm});
            skLineSegment(sketch, "E14.6.3.1", {"start": v(-18.3, -113.6) * mm, "end": v(-18.3, -127.6) * mm});
            skLineSegment(sketch, "E14.9.3.1", {"start": v(-18.3, -113.6) * mm, "end": v(-4.3, -113.6) * mm});
            skLineSegment(sketch, "E14.0.3.2", {"start": v(-18.3, -99.6) * mm, "end": v(-4.3, -99.6) * mm});
            skLineSegment(sketch, "E14.3.3.2", {"start": v(-4.3, -85.6) * mm, "end": v(-4.3, -99.6) * mm});
            skLineSegment(sketch, "E14.6.3.2", {"start": v(-18.3, -85.6) * mm, "end": v(-18.3, -99.6) * mm});
            skLineSegment(sketch, "E14.9.3.2", {"start": v(-18.3, -85.6) * mm, "end": v(-4.3, -85.6) * mm});
            skLineSegment(sketch, "E14.0.3.3", {"start": v(-18.3, -71.6) * mm, "end": v(-4.3, -71.6) * mm});
            skLineSegment(sketch, "E14.3.3.3", {"start": v(-4.3, -57.6) * mm, "end": v(-4.3, -71.6) * mm});
            skLineSegment(sketch, "E14.6.3.3", {"start": v(-18.3, -57.6) * mm, "end": v(-18.3, -71.6) * mm});
            skLineSegment(sketch, "E14.9.3.3", {"start": v(-18.3, -57.6) * mm, "end": v(-4.3, -57.6) * mm});
            skLineSegment(sketch, "E14.0.3.4", {"start": v(-18.3, -43.6) * mm, "end": v(-4.3, -43.6) * mm});
            skLineSegment(sketch, "E14.3.3.4", {"start": v(-4.3, -29.6) * mm, "end": v(-4.3, -43.6) * mm});
            skLineSegment(sketch, "E14.6.3.4", {"start": v(-18.3, -29.6) * mm, "end": v(-18.3, -43.6) * mm});
            skLineSegment(sketch, "E14.9.3.4", {"start": v(-18.3, -29.6) * mm, "end": v(-4.3, -29.6) * mm});
            skLineSegment(sketch, "E14.0.3.5", {"start": v(-18.3, -15.6) * mm, "end": v(-4.3, -15.6) * mm});
            skLineSegment(sketch, "E14.3.3.5", {"start": v(-4.3, -1.6) * mm, "end": v(-4.3, -15.6) * mm});
            skLineSegment(sketch, "E14.6.3.5", {"start": v(-18.3, -1.6) * mm, "end": v(-18.3, -15.6) * mm});
            skLineSegment(sketch, "E14.9.3.5", {"start": v(-18.3, -1.6) * mm, "end": v(-4.3, -1.6) * mm});
            skLineSegment(sketch, "E14.0.3.6", {"start": v(-18.3, 12.4) * mm, "end": v(-4.3, 12.4) * mm});
            skLineSegment(sketch, "E14.3.3.6", {"start": v(-4.3, 26.4) * mm, "end": v(-4.3, 12.4) * mm});
            skLineSegment(sketch, "E14.6.3.6", {"start": v(-18.3, 26.4) * mm, "end": v(-18.3, 12.4) * mm});
            skLineSegment(sketch, "E14.9.3.6", {"start": v(-18.3, 26.4) * mm, "end": v(-4.3, 26.4) * mm});
            skLineSegment(sketch, "E14.0.3.7", {"start": v(-18.3, 40.4) * mm, "end": v(-4.3, 40.4) * mm});
            skLineSegment(sketch, "E14.3.3.7", {"start": v(-4.3, 54.4) * mm, "end": v(-4.3, 40.4) * mm});
            skLineSegment(sketch, "E14.6.3.7", {"start": v(-18.3, 54.4) * mm, "end": v(-18.3, 40.4) * mm});
            skLineSegment(sketch, "E14.9.3.7", {"start": v(-18.3, 54.4) * mm, "end": v(-4.3, 54.4) * mm});
            skLineSegment(sketch, "E14.0.3.8", {"start": v(-18.3, 68.4) * mm, "end": v(-4.3, 68.4) * mm});
            skLineSegment(sketch, "E14.3.3.8", {"start": v(-4.3, 82.4) * mm, "end": v(-4.3, 68.4) * mm});
            skLineSegment(sketch, "E14.6.3.8", {"start": v(-18.3, 82.4) * mm, "end": v(-18.3, 68.4) * mm});
            skLineSegment(sketch, "E14.9.3.8", {"start": v(-18.3, 82.4) * mm, "end": v(-4.3, 82.4) * mm});
            skLineSegment(sketch, "E14.0.3.9", {"start": v(-18.3, 96.4) * mm, "end": v(-4.3, 96.4) * mm});
            skLineSegment(sketch, "E14.3.3.9", {"start": v(-4.3, 110.4) * mm, "end": v(-4.3, 96.4) * mm});
            skLineSegment(sketch, "E14.6.3.9", {"start": v(-18.3, 110.4) * mm, "end": v(-18.3, 96.4) * mm});
            skLineSegment(sketch, "E14.9.3.9", {"start": v(-18.3, 110.4) * mm, "end": v(-4.3, 110.4) * mm});
            skLineSegment(sketch, "E14.0.3.10", {"start": v(-18.3, 124.4) * mm, "end": v(-4.3, 124.4) * mm});
            skLineSegment(sketch, "E14.3.3.10", {"start": v(-4.3, 138.4) * mm, "end": v(-4.3, 124.4) * mm});
            skLineSegment(sketch, "E14.6.3.10", {"start": v(-18.3, 138.4) * mm, "end": v(-18.3, 124.4) * mm});
            skLineSegment(sketch, "E14.9.3.10", {"start": v(-18.3, 138.4) * mm, "end": v(-4.3, 138.4) * mm});
            skLineSegment(sketch, "E14.0.3.11", {"start": v(-18.3, 152.4) * mm, "end": v(-4.3, 152.4) * mm});
            skLineSegment(sketch, "E14.3.3.11", {"start": v(-4.3, 166.4) * mm, "end": v(-4.3, 152.4) * mm});
            skLineSegment(sketch, "E14.6.3.11", {"start": v(-18.3, 166.4) * mm, "end": v(-18.3, 152.4) * mm});
            skLineSegment(sketch, "E14.9.3.11", {"start": v(-18.3, 166.4) * mm, "end": v(-4.3, 166.4) * mm});
            skLineSegment(sketch, "E14.0.4.1", {"start": v(9.7, -127.6) * mm, "end": v(23.7, -127.6) * mm});
            skLineSegment(sketch, "E14.3.4.1", {"start": v(23.7, -113.6) * mm, "end": v(23.7, -127.6) * mm});
            skLineSegment(sketch, "E14.6.4.1", {"start": v(9.7, -113.6) * mm, "end": v(9.7, -127.6) * mm});
            skLineSegment(sketch, "E14.9.4.1", {"start": v(9.7, -113.6) * mm, "end": v(23.7, -113.6) * mm});
            skLineSegment(sketch, "E14.0.4.2", {"start": v(9.7, -99.6) * mm, "end": v(23.7, -99.6) * mm});
            skLineSegment(sketch, "E14.3.4.2", {"start": v(23.7, -85.6) * mm, "end": v(23.7, -99.6) * mm});
            skLineSegment(sketch, "E14.6.4.2", {"start": v(9.7, -85.6) * mm, "end": v(9.7, -99.6) * mm});
            skLineSegment(sketch, "E14.9.4.2", {"start": v(9.7, -85.6) * mm, "end": v(23.7, -85.6) * mm});
            skLineSegment(sketch, "E14.0.4.3", {"start": v(9.7, -71.6) * mm, "end": v(23.7, -71.6) * mm});
            skLineSegment(sketch, "E14.3.4.3", {"start": v(23.7, -57.6) * mm, "end": v(23.7, -71.6) * mm});
            skLineSegment(sketch, "E14.6.4.3", {"start": v(9.7, -57.6) * mm, "end": v(9.7, -71.6) * mm});
            skLineSegment(sketch, "E14.9.4.3", {"start": v(9.7, -57.6) * mm, "end": v(23.7, -57.6) * mm});
            skLineSegment(sketch, "E14.0.4.4", {"start": v(9.7, -43.6) * mm, "end": v(23.7, -43.6) * mm});
            skLineSegment(sketch, "E14.3.4.4", {"start": v(23.7, -29.6) * mm, "end": v(23.7, -43.6) * mm});
            skLineSegment(sketch, "E14.6.4.4", {"start": v(9.7, -29.6) * mm, "end": v(9.7, -43.6) * mm});
            skLineSegment(sketch, "E14.9.4.4", {"start": v(9.7, -29.6) * mm, "end": v(23.7, -29.6) * mm});
            skLineSegment(sketch, "E14.0.4.5", {"start": v(9.7, -15.6) * mm, "end": v(23.7, -15.6) * mm});
            skLineSegment(sketch, "E14.3.4.5", {"start": v(23.7, -1.6) * mm, "end": v(23.7, -15.6) * mm});
            skLineSegment(sketch, "E14.6.4.5", {"start": v(9.7, -1.6) * mm, "end": v(9.7, -15.6) * mm});
            skLineSegment(sketch, "E14.9.4.5", {"start": v(9.7, -1.6) * mm, "end": v(23.7, -1.6) * mm});
            skLineSegment(sketch, "E14.0.4.6", {"start": v(9.7, 12.4) * mm, "end": v(23.7, 12.4) * mm});
            skLineSegment(sketch, "E14.3.4.6", {"start": v(23.7, 26.4) * mm, "end": v(23.7, 12.4) * mm});
            skLineSegment(sketch, "E14.6.4.6", {"start": v(9.7, 26.4) * mm, "end": v(9.7, 12.4) * mm});
            skLineSegment(sketch, "E14.9.4.6", {"start": v(9.7, 26.4) * mm, "end": v(23.7, 26.4) * mm});
            skLineSegment(sketch, "E14.0.4.7", {"start": v(9.7, 40.4) * mm, "end": v(23.7, 40.4) * mm});
            skLineSegment(sketch, "E14.3.4.7", {"start": v(23.7, 54.4) * mm, "end": v(23.7, 40.4) * mm});
            skLineSegment(sketch, "E14.6.4.7", {"start": v(9.7, 54.4) * mm, "end": v(9.7, 40.4) * mm});
            skLineSegment(sketch, "E14.9.4.7", {"start": v(9.7, 54.4) * mm, "end": v(23.7, 54.4) * mm});
            skLineSegment(sketch, "E14.0.4.8", {"start": v(9.7, 68.4) * mm, "end": v(23.7, 68.4) * mm});
            skLineSegment(sketch, "E14.3.4.8", {"start": v(23.7, 82.4) * mm, "end": v(23.7, 68.4) * mm});
            skLineSegment(sketch, "E14.6.4.8", {"start": v(9.7, 82.4) * mm, "end": v(9.7, 68.4) * mm});
            skLineSegment(sketch, "E14.9.4.8", {"start": v(9.7, 82.4) * mm, "end": v(23.7, 82.4) * mm});
            skLineSegment(sketch, "E14.0.4.9", {"start": v(9.7, 96.4) * mm, "end": v(23.7, 96.4) * mm});
            skLineSegment(sketch, "E14.3.4.9", {"start": v(23.7, 110.4) * mm, "end": v(23.7, 96.4) * mm});
            skLineSegment(sketch, "E14.6.4.9", {"start": v(9.7, 110.4) * mm, "end": v(9.7, 96.4) * mm});
            skLineSegment(sketch, "E14.9.4.9", {"start": v(9.7, 110.4) * mm, "end": v(23.7, 110.4) * mm});
            skLineSegment(sketch, "E14.0.4.10", {"start": v(9.7, 124.4) * mm, "end": v(23.7, 124.4) * mm});
            skLineSegment(sketch, "E14.3.4.10", {"start": v(23.7, 138.4) * mm, "end": v(23.7, 124.4) * mm});
            skLineSegment(sketch, "E14.6.4.10", {"start": v(9.7, 138.4) * mm, "end": v(9.7, 124.4) * mm});
            skLineSegment(sketch, "E14.9.4.10", {"start": v(9.7, 138.4) * mm, "end": v(23.7, 138.4) * mm});
            skLineSegment(sketch, "E14.0.4.11", {"start": v(9.7, 152.4) * mm, "end": v(23.7, 152.4) * mm});
            skLineSegment(sketch, "E14.3.4.11", {"start": v(23.7, 166.4) * mm, "end": v(23.7, 152.4) * mm});
            skLineSegment(sketch, "E14.6.4.11", {"start": v(9.7, 166.4) * mm, "end": v(9.7, 152.4) * mm});
            skLineSegment(sketch, "E14.9.4.11", {"start": v(9.7, 166.4) * mm, "end": v(23.7, 166.4) * mm});
            skLineSegment(sketch, "E14.0.5.1", {"start": v(37.7, -127.6) * mm, "end": v(51.7, -127.6) * mm});
            skLineSegment(sketch, "E14.3.5.1", {"start": v(51.7, -113.6) * mm, "end": v(51.7, -127.6) * mm});
            skLineSegment(sketch, "E14.6.5.1", {"start": v(37.7, -113.6) * mm, "end": v(37.7, -127.6) * mm});
            skLineSegment(sketch, "E14.9.5.1", {"start": v(37.7, -113.6) * mm, "end": v(51.7, -113.6) * mm});
            skLineSegment(sketch, "E14.0.5.2", {"start": v(37.7, -99.6) * mm, "end": v(51.7, -99.6) * mm});
            skLineSegment(sketch, "E14.3.5.2", {"start": v(51.7, -85.6) * mm, "end": v(51.7, -99.6) * mm});
            skLineSegment(sketch, "E14.6.5.2", {"start": v(37.7, -85.6) * mm, "end": v(37.7, -99.6) * mm});
            skLineSegment(sketch, "E14.9.5.2", {"start": v(37.7, -85.6) * mm, "end": v(51.7, -85.6) * mm});
            skLineSegment(sketch, "E14.0.5.3", {"start": v(37.7, -71.6) * mm, "end": v(51.7, -71.6) * mm});
            skLineSegment(sketch, "E14.3.5.3", {"start": v(51.7, -57.6) * mm, "end": v(51.7, -71.6) * mm});
            skLineSegment(sketch, "E14.6.5.3", {"start": v(37.7, -57.6) * mm, "end": v(37.7, -71.6) * mm});
            skLineSegment(sketch, "E14.9.5.3", {"start": v(37.7, -57.6) * mm, "end": v(51.7, -57.6) * mm});
            skLineSegment(sketch, "E14.0.5.4", {"start": v(37.7, -43.6) * mm, "end": v(51.7, -43.6) * mm});
            skLineSegment(sketch, "E14.3.5.4", {"start": v(51.7, -29.6) * mm, "end": v(51.7, -43.6) * mm});
            skLineSegment(sketch, "E14.6.5.4", {"start": v(37.7, -29.6) * mm, "end": v(37.7, -43.6) * mm});
            skLineSegment(sketch, "E14.9.5.4", {"start": v(37.7, -29.6) * mm, "end": v(51.7, -29.6) * mm});
            skLineSegment(sketch, "E14.0.5.5", {"start": v(37.7, -15.6) * mm, "end": v(51.7, -15.6) * mm});
            skLineSegment(sketch, "E14.3.5.5", {"start": v(51.7, -1.6) * mm, "end": v(51.7, -15.6) * mm});
            skLineSegment(sketch, "E14.6.5.5", {"start": v(37.7, -1.6) * mm, "end": v(37.7, -15.6) * mm});
            skLineSegment(sketch, "E14.9.5.5", {"start": v(37.7, -1.6) * mm, "end": v(51.7, -1.6) * mm});
            skLineSegment(sketch, "E14.0.5.6", {"start": v(37.7, 12.4) * mm, "end": v(51.7, 12.4) * mm});
            skLineSegment(sketch, "E14.3.5.6", {"start": v(51.7, 26.4) * mm, "end": v(51.7, 12.4) * mm});
            skLineSegment(sketch, "E14.6.5.6", {"start": v(37.7, 26.4) * mm, "end": v(37.7, 12.4) * mm});
            skLineSegment(sketch, "E14.9.5.6", {"start": v(37.7, 26.4) * mm, "end": v(51.7, 26.4) * mm});
            skLineSegment(sketch, "E14.0.5.7", {"start": v(37.7, 40.4) * mm, "end": v(51.7, 40.4) * mm});
            skLineSegment(sketch, "E14.3.5.7", {"start": v(51.7, 54.4) * mm, "end": v(51.7, 40.4) * mm});
            skLineSegment(sketch, "E14.6.5.7", {"start": v(37.7, 54.4) * mm, "end": v(37.7, 40.4) * mm});
            skLineSegment(sketch, "E14.9.5.7", {"start": v(37.7, 54.4) * mm, "end": v(51.7, 54.4) * mm});
            skLineSegment(sketch, "E14.0.5.8", {"start": v(37.7, 68.4) * mm, "end": v(51.7, 68.4) * mm});
            skLineSegment(sketch, "E14.3.5.8", {"start": v(51.7, 82.4) * mm, "end": v(51.7, 68.4) * mm});
            skLineSegment(sketch, "E14.6.5.8", {"start": v(37.7, 82.4) * mm, "end": v(37.7, 68.4) * mm});
            skLineSegment(sketch, "E14.9.5.8", {"start": v(37.7, 82.4) * mm, "end": v(51.7, 82.4) * mm});
            skLineSegment(sketch, "E14.0.5.9", {"start": v(37.7, 96.4) * mm, "end": v(51.7, 96.4) * mm});
            skLineSegment(sketch, "E14.3.5.9", {"start": v(51.7, 110.4) * mm, "end": v(51.7, 96.4) * mm});
            skLineSegment(sketch, "E14.6.5.9", {"start": v(37.7, 110.4) * mm, "end": v(37.7, 96.4) * mm});
            skLineSegment(sketch, "E14.9.5.9", {"start": v(37.7, 110.4) * mm, "end": v(51.7, 110.4) * mm});
            skLineSegment(sketch, "E14.0.5.10", {"start": v(37.7, 124.4) * mm, "end": v(51.7, 124.4) * mm});
            skLineSegment(sketch, "E14.3.5.10", {"start": v(51.7, 138.4) * mm, "end": v(51.7, 124.4) * mm});
            skLineSegment(sketch, "E14.6.5.10", {"start": v(37.7, 138.4) * mm, "end": v(37.7, 124.4) * mm});
            skLineSegment(sketch, "E14.9.5.10", {"start": v(37.7, 138.4) * mm, "end": v(51.7, 138.4) * mm});
            skLineSegment(sketch, "E14.0.5.11", {"start": v(37.7, 152.4) * mm, "end": v(51.7, 152.4) * mm});
            skLineSegment(sketch, "E14.3.5.11", {"start": v(51.7, 166.4) * mm, "end": v(51.7, 152.4) * mm});
            skLineSegment(sketch, "E14.6.5.11", {"start": v(37.7, 166.4) * mm, "end": v(37.7, 152.4) * mm});
            skLineSegment(sketch, "E14.9.5.11", {"start": v(37.7, 166.4) * mm, "end": v(51.7, 166.4) * mm});
            skLineSegment(sketch, "E14.0.6.1", {"start": v(65.7, -127.6) * mm, "end": v(79.7, -127.6) * mm});
            skLineSegment(sketch, "E14.3.6.1", {"start": v(79.7, -113.6) * mm, "end": v(79.7, -127.6) * mm});
            skLineSegment(sketch, "E14.6.6.1", {"start": v(65.7, -113.6) * mm, "end": v(65.7, -127.6) * mm});
            skLineSegment(sketch, "E14.9.6.1", {"start": v(65.7, -113.6) * mm, "end": v(79.7, -113.6) * mm});
            skLineSegment(sketch, "E14.0.6.2", {"start": v(65.7, -99.6) * mm, "end": v(79.7, -99.6) * mm});
            skLineSegment(sketch, "E14.3.6.2", {"start": v(79.7, -85.6) * mm, "end": v(79.7, -99.6) * mm});
            skLineSegment(sketch, "E14.6.6.2", {"start": v(65.7, -85.6) * mm, "end": v(65.7, -99.6) * mm});
            skLineSegment(sketch, "E14.9.6.2", {"start": v(65.7, -85.6) * mm, "end": v(79.7, -85.6) * mm});
            skLineSegment(sketch, "E14.0.6.3", {"start": v(65.7, -71.6) * mm, "end": v(79.7, -71.6) * mm});
            skLineSegment(sketch, "E14.3.6.3", {"start": v(79.7, -57.6) * mm, "end": v(79.7, -71.6) * mm});
            skLineSegment(sketch, "E14.6.6.3", {"start": v(65.7, -57.6) * mm, "end": v(65.7, -71.6) * mm});
            skLineSegment(sketch, "E14.9.6.3", {"start": v(65.7, -57.6) * mm, "end": v(79.7, -57.6) * mm});
            skLineSegment(sketch, "E14.0.6.4", {"start": v(65.7, -43.6) * mm, "end": v(79.7, -43.6) * mm});
            skLineSegment(sketch, "E14.3.6.4", {"start": v(79.7, -29.6) * mm, "end": v(79.7, -43.6) * mm});
            skLineSegment(sketch, "E14.6.6.4", {"start": v(65.7, -29.6) * mm, "end": v(65.7, -43.6) * mm});
            skLineSegment(sketch, "E14.9.6.4", {"start": v(65.7, -29.6) * mm, "end": v(79.7, -29.6) * mm});
            skLineSegment(sketch, "E14.0.6.5", {"start": v(65.7, -15.6) * mm, "end": v(79.7, -15.6) * mm});
            skLineSegment(sketch, "E14.3.6.5", {"start": v(79.7, -1.6) * mm, "end": v(79.7, -15.6) * mm});
            skLineSegment(sketch, "E14.6.6.5", {"start": v(65.7, -1.6) * mm, "end": v(65.7, -15.6) * mm});
            skLineSegment(sketch, "E14.9.6.5", {"start": v(65.7, -1.6) * mm, "end": v(79.7, -1.6) * mm});
            skLineSegment(sketch, "E14.0.6.6", {"start": v(65.7, 12.4) * mm, "end": v(79.7, 12.4) * mm});
            skLineSegment(sketch, "E14.3.6.6", {"start": v(79.7, 26.4) * mm, "end": v(79.7, 12.4) * mm});
            skLineSegment(sketch, "E14.6.6.6", {"start": v(65.7, 26.4) * mm, "end": v(65.7, 12.4) * mm});
            skLineSegment(sketch, "E14.9.6.6", {"start": v(65.7, 26.4) * mm, "end": v(79.7, 26.4) * mm});
            skLineSegment(sketch, "E14.0.6.7", {"start": v(65.7, 40.4) * mm, "end": v(79.7, 40.4) * mm});
            skLineSegment(sketch, "E14.3.6.7", {"start": v(79.7, 54.4) * mm, "end": v(79.7, 40.4) * mm});
            skLineSegment(sketch, "E14.6.6.7", {"start": v(65.7, 54.4) * mm, "end": v(65.7, 40.4) * mm});
            skLineSegment(sketch, "E14.9.6.7", {"start": v(65.7, 54.4) * mm, "end": v(79.7, 54.4) * mm});
            skLineSegment(sketch, "E14.0.6.8", {"start": v(65.7, 68.4) * mm, "end": v(79.7, 68.4) * mm});
            skLineSegment(sketch, "E14.3.6.8", {"start": v(79.7, 82.4) * mm, "end": v(79.7, 68.4) * mm});
            skLineSegment(sketch, "E14.6.6.8", {"start": v(65.7, 82.4) * mm, "end": v(65.7, 68.4) * mm});
            skLineSegment(sketch, "E14.9.6.8", {"start": v(65.7, 82.4) * mm, "end": v(79.7, 82.4) * mm});
            skLineSegment(sketch, "E14.0.6.9", {"start": v(65.7, 96.4) * mm, "end": v(79.7, 96.4) * mm});
            skLineSegment(sketch, "E14.3.6.9", {"start": v(79.7, 110.4) * mm, "end": v(79.7, 96.4) * mm});
            skLineSegment(sketch, "E14.6.6.9", {"start": v(65.7, 110.4) * mm, "end": v(65.7, 96.4) * mm});
            skLineSegment(sketch, "E14.9.6.9", {"start": v(65.7, 110.4) * mm, "end": v(79.7, 110.4) * mm});
            skLineSegment(sketch, "E14.0.6.10", {"start": v(65.7, 124.4) * mm, "end": v(79.7, 124.4) * mm});
            skLineSegment(sketch, "E14.3.6.10", {"start": v(79.7, 138.4) * mm, "end": v(79.7, 124.4) * mm});
            skLineSegment(sketch, "E14.6.6.10", {"start": v(65.7, 138.4) * mm, "end": v(65.7, 124.4) * mm});
            skLineSegment(sketch, "E14.9.6.10", {"start": v(65.7, 138.4) * mm, "end": v(79.7, 138.4) * mm});
            skLineSegment(sketch, "E14.0.6.11", {"start": v(65.7, 152.4) * mm, "end": v(79.7, 152.4) * mm});
            skLineSegment(sketch, "E14.3.6.11", {"start": v(79.7, 166.4) * mm, "end": v(79.7, 152.4) * mm});
            skLineSegment(sketch, "E14.6.6.11", {"start": v(65.7, 166.4) * mm, "end": v(65.7, 152.4) * mm});
            skLineSegment(sketch, "E14.9.6.11", {"start": v(65.7, 166.4) * mm, "end": v(79.7, 166.4) * mm});
            skLineSegment(sketch, "E14.0.7.1", {"start": v(93.7, -127.6) * mm, "end": v(107.7, -127.6) * mm});
            skLineSegment(sketch, "E14.3.7.1", {"start": v(107.7, -113.6) * mm, "end": v(107.7, -127.6) * mm});
            skLineSegment(sketch, "E14.6.7.1", {"start": v(93.7, -113.6) * mm, "end": v(93.7, -127.6) * mm});
            skLineSegment(sketch, "E14.9.7.1", {"start": v(93.7, -113.6) * mm, "end": v(107.7, -113.6) * mm});
            skLineSegment(sketch, "E14.0.7.2", {"start": v(93.7, -99.6) * mm, "end": v(107.7, -99.6) * mm});
            skLineSegment(sketch, "E14.3.7.2", {"start": v(107.7, -85.6) * mm, "end": v(107.7, -99.6) * mm});
            skLineSegment(sketch, "E14.6.7.2", {"start": v(93.7, -85.6) * mm, "end": v(93.7, -99.6) * mm});
            skLineSegment(sketch, "E14.9.7.2", {"start": v(93.7, -85.6) * mm, "end": v(107.7, -85.6) * mm});
            skLineSegment(sketch, "E14.0.7.3", {"start": v(93.7, -71.6) * mm, "end": v(107.7, -71.6) * mm});
            skLineSegment(sketch, "E14.3.7.3", {"start": v(107.7, -57.6) * mm, "end": v(107.7, -71.6) * mm});
            skLineSegment(sketch, "E14.6.7.3", {"start": v(93.7, -57.6) * mm, "end": v(93.7, -71.6) * mm});
            skLineSegment(sketch, "E14.9.7.3", {"start": v(93.7, -57.6) * mm, "end": v(107.7, -57.6) * mm});
            skLineSegment(sketch, "E14.0.7.4", {"start": v(93.7, -43.6) * mm, "end": v(107.7, -43.6) * mm});
            skLineSegment(sketch, "E14.3.7.4", {"start": v(107.7, -29.6) * mm, "end": v(107.7, -43.6) * mm});
            skLineSegment(sketch, "E14.6.7.4", {"start": v(93.7, -29.6) * mm, "end": v(93.7, -43.6) * mm});
            skLineSegment(sketch, "E14.9.7.4", {"start": v(93.7, -29.6) * mm, "end": v(107.7, -29.6) * mm});
            skLineSegment(sketch, "E14.0.7.5", {"start": v(93.7, -15.6) * mm, "end": v(107.7, -15.6) * mm});
            skLineSegment(sketch, "E14.3.7.5", {"start": v(107.7, -1.6) * mm, "end": v(107.7, -15.6) * mm});
            skLineSegment(sketch, "E14.6.7.5", {"start": v(93.7, -1.6) * mm, "end": v(93.7, -15.6) * mm});
            skLineSegment(sketch, "E14.9.7.5", {"start": v(93.7, -1.6) * mm, "end": v(107.7, -1.6) * mm});
            skLineSegment(sketch, "E14.0.7.6", {"start": v(93.7, 12.4) * mm, "end": v(107.7, 12.4) * mm});
            skLineSegment(sketch, "E14.3.7.6", {"start": v(107.7, 26.4) * mm, "end": v(107.7, 12.4) * mm});
            skLineSegment(sketch, "E14.6.7.6", {"start": v(93.7, 26.4) * mm, "end": v(93.7, 12.4) * mm});
            skLineSegment(sketch, "E14.9.7.6", {"start": v(93.7, 26.4) * mm, "end": v(107.7, 26.4) * mm});
            skLineSegment(sketch, "E14.0.7.7", {"start": v(93.7, 40.4) * mm, "end": v(107.7, 40.4) * mm});
            skLineSegment(sketch, "E14.3.7.7", {"start": v(107.7, 54.4) * mm, "end": v(107.7, 40.4) * mm});
            skLineSegment(sketch, "E14.6.7.7", {"start": v(93.7, 54.4) * mm, "end": v(93.7, 40.4) * mm});
            skLineSegment(sketch, "E14.9.7.7", {"start": v(93.7, 54.4) * mm, "end": v(107.7, 54.4) * mm});
            skLineSegment(sketch, "E14.0.7.8", {"start": v(93.7, 68.4) * mm, "end": v(107.7, 68.4) * mm});
            skLineSegment(sketch, "E14.3.7.8", {"start": v(107.7, 82.4) * mm, "end": v(107.7, 68.4) * mm});
            skLineSegment(sketch, "E14.6.7.8", {"start": v(93.7, 82.4) * mm, "end": v(93.7, 68.4) * mm});
            skLineSegment(sketch, "E14.9.7.8", {"start": v(93.7, 82.4) * mm, "end": v(107.7, 82.4) * mm});
            skLineSegment(sketch, "E14.0.7.9", {"start": v(93.7, 96.4) * mm, "end": v(107.7, 96.4) * mm});
            skLineSegment(sketch, "E14.3.7.9", {"start": v(107.7, 110.4) * mm, "end": v(107.7, 96.4) * mm});
            skLineSegment(sketch, "E14.6.7.9", {"start": v(93.7, 110.4) * mm, "end": v(93.7, 96.4) * mm});
            skLineSegment(sketch, "E14.9.7.9", {"start": v(93.7, 110.4) * mm, "end": v(107.7, 110.4) * mm});
            skLineSegment(sketch, "E14.0.7.10", {"start": v(93.7, 124.4) * mm, "end": v(107.7, 124.4) * mm});
            skLineSegment(sketch, "E14.3.7.10", {"start": v(107.7, 138.4) * mm, "end": v(107.7, 124.4) * mm});
            skLineSegment(sketch, "E14.6.7.10", {"start": v(93.7, 138.4) * mm, "end": v(93.7, 124.4) * mm});
            skLineSegment(sketch, "E14.9.7.10", {"start": v(93.7, 138.4) * mm, "end": v(107.7, 138.4) * mm});
            skLineSegment(sketch, "E14.0.7.11", {"start": v(93.7, 152.4) * mm, "end": v(107.7, 152.4) * mm});
            skLineSegment(sketch, "E14.3.7.11", {"start": v(107.7, 166.4) * mm, "end": v(107.7, 152.4) * mm});
            skLineSegment(sketch, "E14.6.7.11", {"start": v(93.7, 166.4) * mm, "end": v(93.7, 152.4) * mm});
            skLineSegment(sketch, "E14.9.7.11", {"start": v(93.7, 166.4) * mm, "end": v(107.7, 166.4) * mm});
            skLineSegment(sketch, "E15.0.0.1", {"start": v(105, -119.5) * mm, "end": v(119, -119.5) * mm});
            skLineSegment(sketch, "E15.3.0.1", {"start": v(105, -105.5) * mm, "end": v(119, -105.5) * mm});
            skLineSegment(sketch, "E15.6.0.1", {"start": v(105, -119.5) * mm, "end": v(105, -105.5) * mm});
            skLineSegment(sketch, "E15.9.0.1", {"start": v(119, -119.5) * mm, "end": v(119, -105.5) * mm});
            skLineSegment(sketch, "E15.0.0.2", {"start": v(105, -91.5) * mm, "end": v(119, -91.5) * mm});
            skLineSegment(sketch, "E15.3.0.2", {"start": v(105, -77.5) * mm, "end": v(119, -77.5) * mm});
            skLineSegment(sketch, "E15.6.0.2", {"start": v(105, -91.5) * mm, "end": v(105, -77.5) * mm});
            skLineSegment(sketch, "E15.9.0.2", {"start": v(119, -91.5) * mm, "end": v(119, -77.5) * mm});
            skLineSegment(sketch, "E15.0.0.3", {"start": v(105, -63.5) * mm, "end": v(119, -63.5) * mm});
            skLineSegment(sketch, "E15.3.0.3", {"start": v(105, -49.5) * mm, "end": v(119, -49.5) * mm});
            skLineSegment(sketch, "E15.6.0.3", {"start": v(105, -63.5) * mm, "end": v(105, -49.5) * mm});
            skLineSegment(sketch, "E15.9.0.3", {"start": v(119, -63.5) * mm, "end": v(119, -49.5) * mm});
            skLineSegment(sketch, "E15.0.0.4", {"start": v(105, -35.5) * mm, "end": v(119, -35.5) * mm});
            skLineSegment(sketch, "E15.3.0.4", {"start": v(105, -21.5) * mm, "end": v(119, -21.5) * mm});
            skLineSegment(sketch, "E15.6.0.4", {"start": v(105, -35.5) * mm, "end": v(105, -21.5) * mm});
            skLineSegment(sketch, "E15.9.0.4", {"start": v(119, -35.5) * mm, "end": v(119, -21.5) * mm});
            skLineSegment(sketch, "E15.0.0.5", {"start": v(105, -7.5) * mm, "end": v(119, -7.5) * mm});
            skLineSegment(sketch, "E15.3.0.5", {"start": v(105, 6.5) * mm, "end": v(119, 6.5) * mm});
            skLineSegment(sketch, "E15.6.0.5", {"start": v(105, -7.5) * mm, "end": v(105, 6.5) * mm});
            skLineSegment(sketch, "E15.9.0.5", {"start": v(119, -7.5) * mm, "end": v(119, 6.5) * mm});
            skLineSegment(sketch, "E15.0.0.6", {"start": v(105, 20.5) * mm, "end": v(119, 20.5) * mm});
            skLineSegment(sketch, "E15.3.0.6", {"start": v(105, 34.5) * mm, "end": v(119, 34.5) * mm});
            skLineSegment(sketch, "E15.6.0.6", {"start": v(105, 20.5) * mm, "end": v(105, 34.5) * mm});
            skLineSegment(sketch, "E15.9.0.6", {"start": v(119, 20.5) * mm, "end": v(119, 34.5) * mm});
            skLineSegment(sketch, "E15.0.0.7", {"start": v(105, 48.5) * mm, "end": v(119, 48.5) * mm});
            skLineSegment(sketch, "E15.3.0.7", {"start": v(105, 62.5) * mm, "end": v(119, 62.5) * mm});
            skLineSegment(sketch, "E15.6.0.7", {"start": v(105, 48.5) * mm, "end": v(105, 62.5) * mm});
            skLineSegment(sketch, "E15.9.0.7", {"start": v(119, 48.5) * mm, "end": v(119, 62.5) * mm});
            skLineSegment(sketch, "E15.0.0.8", {"start": v(105, 76.5) * mm, "end": v(119, 76.5) * mm});
            skLineSegment(sketch, "E15.3.0.8", {"start": v(105, 90.5) * mm, "end": v(119, 90.5) * mm});
            skLineSegment(sketch, "E15.6.0.8", {"start": v(105, 76.5) * mm, "end": v(105, 90.5) * mm});
            skLineSegment(sketch, "E15.9.0.8", {"start": v(119, 76.5) * mm, "end": v(119, 90.5) * mm});
            skLineSegment(sketch, "E16.0.0.9", {"start": v(105, 104.5) * mm, "end": v(119, 104.5) * mm});
            skLineSegment(sketch, "E16.3.0.9", {"start": v(105, 118.5) * mm, "end": v(119, 118.5) * mm});
            skLineSegment(sketch, "E16.6.0.9", {"start": v(105, 104.5) * mm, "end": v(105, 118.5) * mm});
            skLineSegment(sketch, "E16.9.0.9", {"start": v(119, 104.5) * mm, "end": v(119, 118.5) * mm});
            skLineSegment(sketch, "E16.0.0.10", {"start": v(105, 132.5) * mm, "end": v(119, 132.5) * mm});
            skLineSegment(sketch, "E16.3.0.10", {"start": v(105, 146.5) * mm, "end": v(119, 146.5) * mm});
            skLineSegment(sketch, "E16.6.0.10", {"start": v(105, 132.5) * mm, "end": v(105, 146.5) * mm});
            skLineSegment(sketch, "E16.9.0.10", {"start": v(119, 132.5) * mm, "end": v(119, 146.5) * mm});
            skLineSegment(sketch, "E17.0.1.0", {"start": v(77, -147.5) * mm, "end": v(91, -147.5) * mm});
            skLineSegment(sketch, "E17.3.1.0", {"start": v(77, -133.5) * mm, "end": v(91, -133.5) * mm});
            skLineSegment(sketch, "E17.6.1.0", {"start": v(77, -147.5) * mm, "end": v(77, -133.5) * mm});
            skLineSegment(sketch, "E17.9.1.0", {"start": v(91, -147.5) * mm, "end": v(91, -133.5) * mm});
            skLineSegment(sketch, "E17.0.1.1", {"start": v(77, -119.5) * mm, "end": v(91, -119.5) * mm});
            skLineSegment(sketch, "E17.3.1.1", {"start": v(77, -105.5) * mm, "end": v(91, -105.5) * mm});
            skLineSegment(sketch, "E17.6.1.1", {"start": v(77, -119.5) * mm, "end": v(77, -105.5) * mm});
            skLineSegment(sketch, "E17.9.1.1", {"start": v(91, -119.5) * mm, "end": v(91, -105.5) * mm});
            skLineSegment(sketch, "E17.0.1.2", {"start": v(77, -91.5) * mm, "end": v(91, -91.5) * mm});
            skLineSegment(sketch, "E17.3.1.2", {"start": v(77, -77.5) * mm, "end": v(91, -77.5) * mm});
            skLineSegment(sketch, "E17.6.1.2", {"start": v(77, -91.5) * mm, "end": v(77, -77.5) * mm});
            skLineSegment(sketch, "E17.9.1.2", {"start": v(91, -91.5) * mm, "end": v(91, -77.5) * mm});
            skLineSegment(sketch, "E17.0.1.3", {"start": v(77, -63.5) * mm, "end": v(91, -63.5) * mm});
            skLineSegment(sketch, "E17.3.1.3", {"start": v(77, -49.5) * mm, "end": v(91, -49.5) * mm});
            skLineSegment(sketch, "E17.6.1.3", {"start": v(77, -63.5) * mm, "end": v(77, -49.5) * mm});
            skLineSegment(sketch, "E17.9.1.3", {"start": v(91, -63.5) * mm, "end": v(91, -49.5) * mm});
            skLineSegment(sketch, "E17.0.1.4", {"start": v(77, -35.5) * mm, "end": v(91, -35.5) * mm});
            skLineSegment(sketch, "E17.3.1.4", {"start": v(77, -21.5) * mm, "end": v(91, -21.5) * mm});
            skLineSegment(sketch, "E17.6.1.4", {"start": v(77, -35.5) * mm, "end": v(77, -21.5) * mm});
            skLineSegment(sketch, "E17.9.1.4", {"start": v(91, -35.5) * mm, "end": v(91, -21.5) * mm});
            skLineSegment(sketch, "E17.0.1.5", {"start": v(77, -7.5) * mm, "end": v(91, -7.5) * mm});
            skLineSegment(sketch, "E17.3.1.5", {"start": v(77, 6.5) * mm, "end": v(91, 6.5) * mm});
            skLineSegment(sketch, "E17.6.1.5", {"start": v(77, -7.5) * mm, "end": v(77, 6.5) * mm});
            skLineSegment(sketch, "E17.9.1.5", {"start": v(91, -7.5) * mm, "end": v(91, 6.5) * mm});
            skLineSegment(sketch, "E17.0.1.6", {"start": v(77, 20.5) * mm, "end": v(91, 20.5) * mm});
            skLineSegment(sketch, "E17.3.1.6", {"start": v(77, 34.5) * mm, "end": v(91, 34.5) * mm});
            skLineSegment(sketch, "E17.6.1.6", {"start": v(77, 20.5) * mm, "end": v(77, 34.5) * mm});
            skLineSegment(sketch, "E17.9.1.6", {"start": v(91, 20.5) * mm, "end": v(91, 34.5) * mm});
            skLineSegment(sketch, "E17.0.1.7", {"start": v(77, 48.5) * mm, "end": v(91, 48.5) * mm});
            skLineSegment(sketch, "E17.3.1.7", {"start": v(77, 62.5) * mm, "end": v(91, 62.5) * mm});
            skLineSegment(sketch, "E17.6.1.7", {"start": v(77, 48.5) * mm, "end": v(77, 62.5) * mm});
            skLineSegment(sketch, "E17.9.1.7", {"start": v(91, 48.5) * mm, "end": v(91, 62.5) * mm});
            skLineSegment(sketch, "E17.0.1.8", {"start": v(77, 76.5) * mm, "end": v(91, 76.5) * mm});
            skLineSegment(sketch, "E17.3.1.8", {"start": v(77, 90.5) * mm, "end": v(91, 90.5) * mm});
            skLineSegment(sketch, "E17.6.1.8", {"start": v(77, 76.5) * mm, "end": v(77, 90.5) * mm});
            skLineSegment(sketch, "E17.9.1.8", {"start": v(91, 76.5) * mm, "end": v(91, 90.5) * mm});
            skLineSegment(sketch, "E17.0.1.9", {"start": v(77, 104.5) * mm, "end": v(91, 104.5) * mm});
            skLineSegment(sketch, "E17.3.1.9", {"start": v(77, 118.5) * mm, "end": v(91, 118.5) * mm});
            skLineSegment(sketch, "E17.6.1.9", {"start": v(77, 104.5) * mm, "end": v(77, 118.5) * mm});
            skLineSegment(sketch, "E17.9.1.9", {"start": v(91, 104.5) * mm, "end": v(91, 118.5) * mm});
            skLineSegment(sketch, "E17.0.1.10", {"start": v(77, 132.5) * mm, "end": v(91, 132.5) * mm});
            skLineSegment(sketch, "E17.3.1.10", {"start": v(77, 146.5) * mm, "end": v(91, 146.5) * mm});
            skLineSegment(sketch, "E17.6.1.10", {"start": v(77, 132.5) * mm, "end": v(77, 146.5) * mm});
            skLineSegment(sketch, "E17.9.1.10", {"start": v(91, 132.5) * mm, "end": v(91, 146.5) * mm});
            skLineSegment(sketch, "E17.0.2.0", {"start": v(49, -147.5) * mm, "end": v(63, -147.5) * mm});
            skLineSegment(sketch, "E17.3.2.0", {"start": v(49, -133.5) * mm, "end": v(63, -133.5) * mm});
            skLineSegment(sketch, "E17.6.2.0", {"start": v(49, -147.5) * mm, "end": v(49, -133.5) * mm});
            skLineSegment(sketch, "E17.9.2.0", {"start": v(63, -147.5) * mm, "end": v(63, -133.5) * mm});
            skLineSegment(sketch, "E17.0.2.1", {"start": v(49, -119.5) * mm, "end": v(63, -119.5) * mm});
            skLineSegment(sketch, "E17.3.2.1", {"start": v(49, -105.5) * mm, "end": v(63, -105.5) * mm});
            skLineSegment(sketch, "E17.6.2.1", {"start": v(49, -119.5) * mm, "end": v(49, -105.5) * mm});
            skLineSegment(sketch, "E17.9.2.1", {"start": v(63, -119.5) * mm, "end": v(63, -105.5) * mm});
            skLineSegment(sketch, "E17.0.2.2", {"start": v(49, -91.5) * mm, "end": v(63, -91.5) * mm});
            skLineSegment(sketch, "E17.3.2.2", {"start": v(49, -77.5) * mm, "end": v(63, -77.5) * mm});
            skLineSegment(sketch, "E17.6.2.2", {"start": v(49, -91.5) * mm, "end": v(49, -77.5) * mm});
            skLineSegment(sketch, "E17.9.2.2", {"start": v(63, -91.5) * mm, "end": v(63, -77.5) * mm});
            skLineSegment(sketch, "E17.0.2.3", {"start": v(49, -63.5) * mm, "end": v(63, -63.5) * mm});
            skLineSegment(sketch, "E17.3.2.3", {"start": v(49, -49.5) * mm, "end": v(63, -49.5) * mm});
            skLineSegment(sketch, "E17.6.2.3", {"start": v(49, -63.5) * mm, "end": v(49, -49.5) * mm});
            skLineSegment(sketch, "E17.9.2.3", {"start": v(63, -63.5) * mm, "end": v(63, -49.5) * mm});
            skLineSegment(sketch, "E17.0.2.4", {"start": v(49, -35.5) * mm, "end": v(63, -35.5) * mm});
            skLineSegment(sketch, "E17.3.2.4", {"start": v(49, -21.5) * mm, "end": v(63, -21.5) * mm});
            skLineSegment(sketch, "E17.6.2.4", {"start": v(49, -35.5) * mm, "end": v(49, -21.5) * mm});
            skLineSegment(sketch, "E17.9.2.4", {"start": v(63, -35.5) * mm, "end": v(63, -21.5) * mm});
            skLineSegment(sketch, "E17.0.2.5", {"start": v(49, -7.5) * mm, "end": v(63, -7.5) * mm});
            skLineSegment(sketch, "E17.3.2.5", {"start": v(49, 6.5) * mm, "end": v(63, 6.5) * mm});
            skLineSegment(sketch, "E17.6.2.5", {"start": v(49, -7.5) * mm, "end": v(49, 6.5) * mm});
            skLineSegment(sketch, "E17.9.2.5", {"start": v(63, -7.5) * mm, "end": v(63, 6.5) * mm});
            skLineSegment(sketch, "E17.0.2.6", {"start": v(49, 20.5) * mm, "end": v(63, 20.5) * mm});
            skLineSegment(sketch, "E17.3.2.6", {"start": v(49, 34.5) * mm, "end": v(63, 34.5) * mm});
            skLineSegment(sketch, "E17.6.2.6", {"start": v(49, 20.5) * mm, "end": v(49, 34.5) * mm});
            skLineSegment(sketch, "E17.9.2.6", {"start": v(63, 20.5) * mm, "end": v(63, 34.5) * mm});
            skLineSegment(sketch, "E17.0.2.7", {"start": v(49, 48.5) * mm, "end": v(63, 48.5) * mm});
            skLineSegment(sketch, "E17.3.2.7", {"start": v(49, 62.5) * mm, "end": v(63, 62.5) * mm});
            skLineSegment(sketch, "E17.6.2.7", {"start": v(49, 48.5) * mm, "end": v(49, 62.5) * mm});
            skLineSegment(sketch, "E17.9.2.7", {"start": v(63, 48.5) * mm, "end": v(63, 62.5) * mm});
            skLineSegment(sketch, "E17.0.2.8", {"start": v(49, 76.5) * mm, "end": v(63, 76.5) * mm});
            skLineSegment(sketch, "E17.3.2.8", {"start": v(49, 90.5) * mm, "end": v(63, 90.5) * mm});
            skLineSegment(sketch, "E17.6.2.8", {"start": v(49, 76.5) * mm, "end": v(49, 90.5) * mm});
            skLineSegment(sketch, "E17.9.2.8", {"start": v(63, 76.5) * mm, "end": v(63, 90.5) * mm});
            skLineSegment(sketch, "E17.0.2.9", {"start": v(49, 104.5) * mm, "end": v(63, 104.5) * mm});
            skLineSegment(sketch, "E17.3.2.9", {"start": v(49, 118.5) * mm, "end": v(63, 118.5) * mm});
            skLineSegment(sketch, "E17.6.2.9", {"start": v(49, 104.5) * mm, "end": v(49, 118.5) * mm});
            skLineSegment(sketch, "E17.9.2.9", {"start": v(63, 104.5) * mm, "end": v(63, 118.5) * mm});
            skLineSegment(sketch, "E17.0.2.10", {"start": v(49, 132.5) * mm, "end": v(63, 132.5) * mm});
            skLineSegment(sketch, "E17.3.2.10", {"start": v(49, 146.5) * mm, "end": v(63, 146.5) * mm});
            skLineSegment(sketch, "E17.6.2.10", {"start": v(49, 132.5) * mm, "end": v(49, 146.5) * mm});
            skLineSegment(sketch, "E17.9.2.10", {"start": v(63, 132.5) * mm, "end": v(63, 146.5) * mm});
            skLineSegment(sketch, "E17.0.3.0", {"start": v(21, -147.5) * mm, "end": v(35, -147.5) * mm});
            skLineSegment(sketch, "E17.3.3.0", {"start": v(21, -133.5) * mm, "end": v(35, -133.5) * mm});
            skLineSegment(sketch, "E17.6.3.0", {"start": v(21, -147.5) * mm, "end": v(21, -133.5) * mm});
            skLineSegment(sketch, "E17.9.3.0", {"start": v(35, -147.5) * mm, "end": v(35, -133.5) * mm});
            skLineSegment(sketch, "E17.0.3.1", {"start": v(21, -119.5) * mm, "end": v(35, -119.5) * mm});
            skLineSegment(sketch, "E17.3.3.1", {"start": v(21, -105.5) * mm, "end": v(35, -105.5) * mm});
            skLineSegment(sketch, "E17.6.3.1", {"start": v(21, -119.5) * mm, "end": v(21, -105.5) * mm});
            skLineSegment(sketch, "E17.9.3.1", {"start": v(35, -119.5) * mm, "end": v(35, -105.5) * mm});
            skLineSegment(sketch, "E17.0.3.2", {"start": v(21, -91.5) * mm, "end": v(35, -91.5) * mm});
            skLineSegment(sketch, "E17.3.3.2", {"start": v(21, -77.5) * mm, "end": v(35, -77.5) * mm});
            skLineSegment(sketch, "E17.6.3.2", {"start": v(21, -91.5) * mm, "end": v(21, -77.5) * mm});
            skLineSegment(sketch, "E17.9.3.2", {"start": v(35, -91.5) * mm, "end": v(35, -77.5) * mm});
            skLineSegment(sketch, "E17.0.3.3", {"start": v(21, -63.5) * mm, "end": v(35, -63.5) * mm});
            skLineSegment(sketch, "E17.3.3.3", {"start": v(21, -49.5) * mm, "end": v(35, -49.5) * mm});
            skLineSegment(sketch, "E17.6.3.3", {"start": v(21, -63.5) * mm, "end": v(21, -49.5) * mm});
            skLineSegment(sketch, "E17.9.3.3", {"start": v(35, -63.5) * mm, "end": v(35, -49.5) * mm});
            skLineSegment(sketch, "E17.0.3.4", {"start": v(21, -35.5) * mm, "end": v(35, -35.5) * mm});
            skLineSegment(sketch, "E17.3.3.4", {"start": v(21, -21.5) * mm, "end": v(35, -21.5) * mm});
            skLineSegment(sketch, "E17.6.3.4", {"start": v(21, -35.5) * mm, "end": v(21, -21.5) * mm});
            skLineSegment(sketch, "E17.9.3.4", {"start": v(35, -35.5) * mm, "end": v(35, -21.5) * mm});
            skLineSegment(sketch, "E17.0.3.5", {"start": v(21, -7.5) * mm, "end": v(35, -7.5) * mm});
            skLineSegment(sketch, "E17.3.3.5", {"start": v(21, 6.5) * mm, "end": v(35, 6.5) * mm});
            skLineSegment(sketch, "E17.6.3.5", {"start": v(21, -7.5) * mm, "end": v(21, 6.5) * mm});
            skLineSegment(sketch, "E17.9.3.5", {"start": v(35, -7.5) * mm, "end": v(35, 6.5) * mm});
            skLineSegment(sketch, "E17.0.3.6", {"start": v(21, 20.5) * mm, "end": v(35, 20.5) * mm});
            skLineSegment(sketch, "E17.3.3.6", {"start": v(21, 34.5) * mm, "end": v(35, 34.5) * mm});
            skLineSegment(sketch, "E17.6.3.6", {"start": v(21, 20.5) * mm, "end": v(21, 34.5) * mm});
            skLineSegment(sketch, "E17.9.3.6", {"start": v(35, 20.5) * mm, "end": v(35, 34.5) * mm});
            skLineSegment(sketch, "E17.0.3.7", {"start": v(21, 48.5) * mm, "end": v(35, 48.5) * mm});
            skLineSegment(sketch, "E17.3.3.7", {"start": v(21, 62.5) * mm, "end": v(35, 62.5) * mm});
            skLineSegment(sketch, "E17.6.3.7", {"start": v(21, 48.5) * mm, "end": v(21, 62.5) * mm});
            skLineSegment(sketch, "E17.9.3.7", {"start": v(35, 48.5) * mm, "end": v(35, 62.5) * mm});
            skLineSegment(sketch, "E17.0.3.8", {"start": v(21, 76.5) * mm, "end": v(35, 76.5) * mm});
            skLineSegment(sketch, "E17.3.3.8", {"start": v(21, 90.5) * mm, "end": v(35, 90.5) * mm});
            skLineSegment(sketch, "E17.6.3.8", {"start": v(21, 76.5) * mm, "end": v(21, 90.5) * mm});
            skLineSegment(sketch, "E17.9.3.8", {"start": v(35, 76.5) * mm, "end": v(35, 90.5) * mm});
            skLineSegment(sketch, "E17.0.3.9", {"start": v(21, 104.5) * mm, "end": v(35, 104.5) * mm});
            skLineSegment(sketch, "E17.3.3.9", {"start": v(21, 118.5) * mm, "end": v(35, 118.5) * mm});
            skLineSegment(sketch, "E17.6.3.9", {"start": v(21, 104.5) * mm, "end": v(21, 118.5) * mm});
            skLineSegment(sketch, "E17.9.3.9", {"start": v(35, 104.5) * mm, "end": v(35, 118.5) * mm});
            skLineSegment(sketch, "E17.0.3.10", {"start": v(21, 132.5) * mm, "end": v(35, 132.5) * mm});
            skLineSegment(sketch, "E17.3.3.10", {"start": v(21, 146.5) * mm, "end": v(35, 146.5) * mm});
            skLineSegment(sketch, "E17.6.3.10", {"start": v(21, 132.5) * mm, "end": v(21, 146.5) * mm});
            skLineSegment(sketch, "E17.9.3.10", {"start": v(35, 132.5) * mm, "end": v(35, 146.5) * mm});
            skLineSegment(sketch, "E17.0.4.0", {"start": v(-7, -147.5) * mm, "end": v(7, -147.5) * mm});
            skLineSegment(sketch, "E17.3.4.0", {"start": v(-7, -133.5) * mm, "end": v(7, -133.5) * mm});
            skLineSegment(sketch, "E17.6.4.0", {"start": v(-7, -147.5) * mm, "end": v(-7, -133.5) * mm});
            skLineSegment(sketch, "E17.9.4.0", {"start": v(7, -147.5) * mm, "end": v(7, -133.5) * mm});
            skLineSegment(sketch, "E17.0.4.1", {"start": v(-7, -119.5) * mm, "end": v(7, -119.5) * mm});
            skLineSegment(sketch, "E17.3.4.1", {"start": v(-7, -105.5) * mm, "end": v(7, -105.5) * mm});
            skLineSegment(sketch, "E17.6.4.1", {"start": v(-7, -119.5) * mm, "end": v(-7, -105.5) * mm});
            skLineSegment(sketch, "E17.9.4.1", {"start": v(7, -119.5) * mm, "end": v(7, -105.5) * mm});
            skLineSegment(sketch, "E17.0.4.2", {"start": v(-7, -91.5) * mm, "end": v(7, -91.5) * mm});
            skLineSegment(sketch, "E17.3.4.2", {"start": v(-7, -77.5) * mm, "end": v(7, -77.5) * mm});
            skLineSegment(sketch, "E17.6.4.2", {"start": v(-7, -91.5) * mm, "end": v(-7, -77.5) * mm});
            skLineSegment(sketch, "E17.9.4.2", {"start": v(7, -91.5) * mm, "end": v(7, -77.5) * mm});
            skLineSegment(sketch, "E17.0.4.3", {"start": v(-7, -63.5) * mm, "end": v(7, -63.5) * mm});
            skLineSegment(sketch, "E17.3.4.3", {"start": v(-7, -49.5) * mm, "end": v(7, -49.5) * mm});
            skLineSegment(sketch, "E17.6.4.3", {"start": v(-7, -63.5) * mm, "end": v(-7, -49.5) * mm});
            skLineSegment(sketch, "E17.9.4.3", {"start": v(7, -63.5) * mm, "end": v(7, -49.5) * mm});
            skLineSegment(sketch, "E17.0.4.4", {"start": v(-7, -35.5) * mm, "end": v(7, -35.5) * mm});
            skLineSegment(sketch, "E17.3.4.4", {"start": v(-7, -21.5) * mm, "end": v(7, -21.5) * mm});
            skLineSegment(sketch, "E17.6.4.4", {"start": v(-7, -35.5) * mm, "end": v(-7, -21.5) * mm});
            skLineSegment(sketch, "E17.9.4.4", {"start": v(7, -35.5) * mm, "end": v(7, -21.5) * mm});
            skLineSegment(sketch, "E17.0.4.5", {"start": v(-7, -7.5) * mm, "end": v(7, -7.5) * mm});
            skLineSegment(sketch, "E17.3.4.5", {"start": v(-7, 6.5) * mm, "end": v(7, 6.5) * mm});
            skLineSegment(sketch, "E17.6.4.5", {"start": v(-7, -7.5) * mm, "end": v(-7, 6.5) * mm});
            skLineSegment(sketch, "E17.9.4.5", {"start": v(7, -7.5) * mm, "end": v(7, 6.5) * mm});
            skLineSegment(sketch, "E17.0.4.6", {"start": v(-7, 20.5) * mm, "end": v(7, 20.5) * mm});
            skLineSegment(sketch, "E17.3.4.6", {"start": v(-7, 34.5) * mm, "end": v(7, 34.5) * mm});
            skLineSegment(sketch, "E17.6.4.6", {"start": v(-7, 20.5) * mm, "end": v(-7, 34.5) * mm});
            skLineSegment(sketch, "E17.9.4.6", {"start": v(7, 20.5) * mm, "end": v(7, 34.5) * mm});
            skLineSegment(sketch, "E17.0.4.7", {"start": v(-7, 48.5) * mm, "end": v(7, 48.5) * mm});
            skLineSegment(sketch, "E17.3.4.7", {"start": v(-7, 62.5) * mm, "end": v(7, 62.5) * mm});
            skLineSegment(sketch, "E17.6.4.7", {"start": v(-7, 48.5) * mm, "end": v(-7, 62.5) * mm});
            skLineSegment(sketch, "E17.9.4.7", {"start": v(7, 48.5) * mm, "end": v(7, 62.5) * mm});
            skLineSegment(sketch, "E17.0.4.8", {"start": v(-7, 76.5) * mm, "end": v(7, 76.5) * mm});
            skLineSegment(sketch, "E17.3.4.8", {"start": v(-7, 90.5) * mm, "end": v(7, 90.5) * mm});
            skLineSegment(sketch, "E17.6.4.8", {"start": v(-7, 76.5) * mm, "end": v(-7, 90.5) * mm});
            skLineSegment(sketch, "E17.9.4.8", {"start": v(7, 76.5) * mm, "end": v(7, 90.5) * mm});
            skLineSegment(sketch, "E17.0.4.9", {"start": v(-7, 104.5) * mm, "end": v(7, 104.5) * mm});
            skLineSegment(sketch, "E17.3.4.9", {"start": v(-7, 118.5) * mm, "end": v(7, 118.5) * mm});
            skLineSegment(sketch, "E17.6.4.9", {"start": v(-7, 104.5) * mm, "end": v(-7, 118.5) * mm});
            skLineSegment(sketch, "E17.9.4.9", {"start": v(7, 104.5) * mm, "end": v(7, 118.5) * mm});
            skLineSegment(sketch, "E17.0.4.10", {"start": v(-7, 132.5) * mm, "end": v(7, 132.5) * mm});
            skLineSegment(sketch, "E17.3.4.10", {"start": v(-7, 146.5) * mm, "end": v(7, 146.5) * mm});
            skLineSegment(sketch, "E17.6.4.10", {"start": v(-7, 132.5) * mm, "end": v(-7, 146.5) * mm});
            skLineSegment(sketch, "E17.9.4.10", {"start": v(7, 132.5) * mm, "end": v(7, 146.5) * mm});
            skLineSegment(sketch, "E17.0.5.0", {"start": v(-35, -147.5) * mm, "end": v(-21, -147.5) * mm});
            skLineSegment(sketch, "E17.3.5.0", {"start": v(-35, -133.5) * mm, "end": v(-21, -133.5) * mm});
            skLineSegment(sketch, "E17.6.5.0", {"start": v(-35, -147.5) * mm, "end": v(-35, -133.5) * mm});
            skLineSegment(sketch, "E17.9.5.0", {"start": v(-21, -147.5) * mm, "end": v(-21, -133.5) * mm});
            skLineSegment(sketch, "E17.0.5.1", {"start": v(-35, -119.5) * mm, "end": v(-21, -119.5) * mm});
            skLineSegment(sketch, "E17.3.5.1", {"start": v(-35, -105.5) * mm, "end": v(-21, -105.5) * mm});
            skLineSegment(sketch, "E17.6.5.1", {"start": v(-35, -119.5) * mm, "end": v(-35, -105.5) * mm});
            skLineSegment(sketch, "E17.9.5.1", {"start": v(-21, -119.5) * mm, "end": v(-21, -105.5) * mm});
            skLineSegment(sketch, "E17.0.5.2", {"start": v(-35, -91.5) * mm, "end": v(-21, -91.5) * mm});
            skLineSegment(sketch, "E17.3.5.2", {"start": v(-35, -77.5) * mm, "end": v(-21, -77.5) * mm});
            skLineSegment(sketch, "E17.6.5.2", {"start": v(-35, -91.5) * mm, "end": v(-35, -77.5) * mm});
            skLineSegment(sketch, "E17.9.5.2", {"start": v(-21, -91.5) * mm, "end": v(-21, -77.5) * mm});
            skLineSegment(sketch, "E17.0.5.3", {"start": v(-35, -63.5) * mm, "end": v(-21, -63.5) * mm});
            skLineSegment(sketch, "E17.3.5.3", {"start": v(-35, -49.5) * mm, "end": v(-21, -49.5) * mm});
            skLineSegment(sketch, "E17.6.5.3", {"start": v(-35, -63.5) * mm, "end": v(-35, -49.5) * mm});
            skLineSegment(sketch, "E17.9.5.3", {"start": v(-21, -63.5) * mm, "end": v(-21, -49.5) * mm});
            skLineSegment(sketch, "E17.0.5.4", {"start": v(-35, -35.5) * mm, "end": v(-21, -35.5) * mm});
            skLineSegment(sketch, "E17.3.5.4", {"start": v(-35, -21.5) * mm, "end": v(-21, -21.5) * mm});
            skLineSegment(sketch, "E17.6.5.4", {"start": v(-35, -35.5) * mm, "end": v(-35, -21.5) * mm});
            skLineSegment(sketch, "E17.9.5.4", {"start": v(-21, -35.5) * mm, "end": v(-21, -21.5) * mm});
            skLineSegment(sketch, "E17.0.5.5", {"start": v(-35, -7.5) * mm, "end": v(-21, -7.5) * mm});
            skLineSegment(sketch, "E17.3.5.5", {"start": v(-35, 6.5) * mm, "end": v(-21, 6.5) * mm});
            skLineSegment(sketch, "E17.6.5.5", {"start": v(-35, -7.5) * mm, "end": v(-35, 6.5) * mm});
            skLineSegment(sketch, "E17.9.5.5", {"start": v(-21, -7.5) * mm, "end": v(-21, 6.5) * mm});
            skLineSegment(sketch, "E17.0.5.6", {"start": v(-35, 20.5) * mm, "end": v(-21, 20.5) * mm});
            skLineSegment(sketch, "E17.3.5.6", {"start": v(-35, 34.5) * mm, "end": v(-21, 34.5) * mm});
            skLineSegment(sketch, "E17.6.5.6", {"start": v(-35, 20.5) * mm, "end": v(-35, 34.5) * mm});
            skLineSegment(sketch, "E17.9.5.6", {"start": v(-21, 20.5) * mm, "end": v(-21, 34.5) * mm});
            skLineSegment(sketch, "E17.0.5.7", {"start": v(-35, 48.5) * mm, "end": v(-21, 48.5) * mm});
            skLineSegment(sketch, "E17.3.5.7", {"start": v(-35, 62.5) * mm, "end": v(-21, 62.5) * mm});
            skLineSegment(sketch, "E17.6.5.7", {"start": v(-35, 48.5) * mm, "end": v(-35, 62.5) * mm});
            skLineSegment(sketch, "E17.9.5.7", {"start": v(-21, 48.5) * mm, "end": v(-21, 62.5) * mm});
            skLineSegment(sketch, "E17.0.5.8", {"start": v(-35, 76.5) * mm, "end": v(-21, 76.5) * mm});
            skLineSegment(sketch, "E17.3.5.8", {"start": v(-35, 90.5) * mm, "end": v(-21, 90.5) * mm});
            skLineSegment(sketch, "E17.6.5.8", {"start": v(-35, 76.5) * mm, "end": v(-35, 90.5) * mm});
            skLineSegment(sketch, "E17.9.5.8", {"start": v(-21, 76.5) * mm, "end": v(-21, 90.5) * mm});
            skLineSegment(sketch, "E17.0.5.9", {"start": v(-35, 104.5) * mm, "end": v(-21, 104.5) * mm});
            skLineSegment(sketch, "E17.3.5.9", {"start": v(-35, 118.5) * mm, "end": v(-21, 118.5) * mm});
            skLineSegment(sketch, "E17.6.5.9", {"start": v(-35, 104.5) * mm, "end": v(-35, 118.5) * mm});
            skLineSegment(sketch, "E17.9.5.9", {"start": v(-21, 104.5) * mm, "end": v(-21, 118.5) * mm});
            skLineSegment(sketch, "E17.0.5.10", {"start": v(-35, 132.5) * mm, "end": v(-21, 132.5) * mm});
            skLineSegment(sketch, "E17.3.5.10", {"start": v(-35, 146.5) * mm, "end": v(-21, 146.5) * mm});
            skLineSegment(sketch, "E17.6.5.10", {"start": v(-35, 132.5) * mm, "end": v(-35, 146.5) * mm});
            skLineSegment(sketch, "E17.9.5.10", {"start": v(-21, 132.5) * mm, "end": v(-21, 146.5) * mm});
            skLineSegment(sketch, "E17.0.6.0", {"start": v(-63, -147.5) * mm, "end": v(-49, -147.5) * mm});
            skLineSegment(sketch, "E17.3.6.0", {"start": v(-63, -133.5) * mm, "end": v(-49, -133.5) * mm});
            skLineSegment(sketch, "E17.6.6.0", {"start": v(-63, -147.5) * mm, "end": v(-63, -133.5) * mm});
            skLineSegment(sketch, "E17.9.6.0", {"start": v(-49, -147.5) * mm, "end": v(-49, -133.5) * mm});
            skLineSegment(sketch, "E17.0.6.1", {"start": v(-63, -119.5) * mm, "end": v(-49, -119.5) * mm});
            skLineSegment(sketch, "E17.3.6.1", {"start": v(-63, -105.5) * mm, "end": v(-49, -105.5) * mm});
            skLineSegment(sketch, "E17.6.6.1", {"start": v(-63, -119.5) * mm, "end": v(-63, -105.5) * mm});
            skLineSegment(sketch, "E17.9.6.1", {"start": v(-49, -119.5) * mm, "end": v(-49, -105.5) * mm});
            skLineSegment(sketch, "E17.0.6.2", {"start": v(-63, -91.5) * mm, "end": v(-49, -91.5) * mm});
            skLineSegment(sketch, "E17.3.6.2", {"start": v(-63, -77.5) * mm, "end": v(-49, -77.5) * mm});
            skLineSegment(sketch, "E17.6.6.2", {"start": v(-63, -91.5) * mm, "end": v(-63, -77.5) * mm});
            skLineSegment(sketch, "E17.9.6.2", {"start": v(-49, -91.5) * mm, "end": v(-49, -77.5) * mm});
            skLineSegment(sketch, "E17.0.6.3", {"start": v(-63, -63.5) * mm, "end": v(-49, -63.5) * mm});
            skLineSegment(sketch, "E17.3.6.3", {"start": v(-63, -49.5) * mm, "end": v(-49, -49.5) * mm});
            skLineSegment(sketch, "E17.6.6.3", {"start": v(-63, -63.5) * mm, "end": v(-63, -49.5) * mm});
            skLineSegment(sketch, "E17.9.6.3", {"start": v(-49, -63.5) * mm, "end": v(-49, -49.5) * mm});
            skLineSegment(sketch, "E17.0.6.4", {"start": v(-63, -35.5) * mm, "end": v(-49, -35.5) * mm});
            skLineSegment(sketch, "E17.3.6.4", {"start": v(-63, -21.5) * mm, "end": v(-49, -21.5) * mm});
            skLineSegment(sketch, "E17.6.6.4", {"start": v(-63, -35.5) * mm, "end": v(-63, -21.5) * mm});
            skLineSegment(sketch, "E17.9.6.4", {"start": v(-49, -35.5) * mm, "end": v(-49, -21.5) * mm});
            skLineSegment(sketch, "E17.0.6.5", {"start": v(-63, -7.5) * mm, "end": v(-49, -7.5) * mm});
            skLineSegment(sketch, "E17.3.6.5", {"start": v(-63, 6.5) * mm, "end": v(-49, 6.5) * mm});
            skLineSegment(sketch, "E17.6.6.5", {"start": v(-63, -7.5) * mm, "end": v(-63, 6.5) * mm});
            skLineSegment(sketch, "E17.9.6.5", {"start": v(-49, -7.5) * mm, "end": v(-49, 6.5) * mm});
            skLineSegment(sketch, "E17.0.6.6", {"start": v(-63, 20.5) * mm, "end": v(-49, 20.5) * mm});
            skLineSegment(sketch, "E17.3.6.6", {"start": v(-63, 34.5) * mm, "end": v(-49, 34.5) * mm});
            skLineSegment(sketch, "E17.6.6.6", {"start": v(-63, 20.5) * mm, "end": v(-63, 34.5) * mm});
            skLineSegment(sketch, "E17.9.6.6", {"start": v(-49, 20.5) * mm, "end": v(-49, 34.5) * mm});
            skLineSegment(sketch, "E17.0.6.7", {"start": v(-63, 48.5) * mm, "end": v(-49, 48.5) * mm});
            skLineSegment(sketch, "E17.3.6.7", {"start": v(-63, 62.5) * mm, "end": v(-49, 62.5) * mm});
            skLineSegment(sketch, "E17.6.6.7", {"start": v(-63, 48.5) * mm, "end": v(-63, 62.5) * mm});
            skLineSegment(sketch, "E17.9.6.7", {"start": v(-49, 48.5) * mm, "end": v(-49, 62.5) * mm});
            skLineSegment(sketch, "E17.0.6.8", {"start": v(-63, 76.5) * mm, "end": v(-49, 76.5) * mm});
            skLineSegment(sketch, "E17.3.6.8", {"start": v(-63, 90.5) * mm, "end": v(-49, 90.5) * mm});
            skLineSegment(sketch, "E17.6.6.8", {"start": v(-63, 76.5) * mm, "end": v(-63, 90.5) * mm});
            skLineSegment(sketch, "E17.9.6.8", {"start": v(-49, 76.5) * mm, "end": v(-49, 90.5) * mm});
            skLineSegment(sketch, "E17.0.6.9", {"start": v(-63, 104.5) * mm, "end": v(-49, 104.5) * mm});
            skLineSegment(sketch, "E17.3.6.9", {"start": v(-63, 118.5) * mm, "end": v(-49, 118.5) * mm});
            skLineSegment(sketch, "E17.6.6.9", {"start": v(-63, 104.5) * mm, "end": v(-63, 118.5) * mm});
            skLineSegment(sketch, "E17.9.6.9", {"start": v(-49, 104.5) * mm, "end": v(-49, 118.5) * mm});
            skLineSegment(sketch, "E17.0.6.10", {"start": v(-63, 132.5) * mm, "end": v(-49, 132.5) * mm});
            skLineSegment(sketch, "E17.3.6.10", {"start": v(-63, 146.5) * mm, "end": v(-49, 146.5) * mm});
            skLineSegment(sketch, "E17.6.6.10", {"start": v(-63, 132.5) * mm, "end": v(-63, 146.5) * mm});
            skLineSegment(sketch, "E17.9.6.10", {"start": v(-49, 132.5) * mm, "end": v(-49, 146.5) * mm});
            skLineSegment(sketch, "E17.0.7.0", {"start": v(-91, -147.5) * mm, "end": v(-77, -147.5) * mm});
            skLineSegment(sketch, "E17.3.7.0", {"start": v(-91, -133.5) * mm, "end": v(-77, -133.5) * mm});
            skLineSegment(sketch, "E17.6.7.0", {"start": v(-91, -147.5) * mm, "end": v(-91, -133.5) * mm});
            skLineSegment(sketch, "E17.9.7.0", {"start": v(-77, -147.5) * mm, "end": v(-77, -133.5) * mm});
            skLineSegment(sketch, "E17.0.7.1", {"start": v(-91, -119.5) * mm, "end": v(-77, -119.5) * mm});
            skLineSegment(sketch, "E17.3.7.1", {"start": v(-91, -105.5) * mm, "end": v(-77, -105.5) * mm});
            skLineSegment(sketch, "E17.6.7.1", {"start": v(-91, -119.5) * mm, "end": v(-91, -105.5) * mm});
            skLineSegment(sketch, "E17.9.7.1", {"start": v(-77, -119.5) * mm, "end": v(-77, -105.5) * mm});
            skLineSegment(sketch, "E17.0.7.2", {"start": v(-91, -91.5) * mm, "end": v(-77, -91.5) * mm});
            skLineSegment(sketch, "E17.3.7.2", {"start": v(-91, -77.5) * mm, "end": v(-77, -77.5) * mm});
            skLineSegment(sketch, "E17.6.7.2", {"start": v(-91, -91.5) * mm, "end": v(-91, -77.5) * mm});
            skLineSegment(sketch, "E17.9.7.2", {"start": v(-77, -91.5) * mm, "end": v(-77, -77.5) * mm});
            skLineSegment(sketch, "E17.0.7.3", {"start": v(-91, -63.5) * mm, "end": v(-77, -63.5) * mm});
            skLineSegment(sketch, "E17.3.7.3", {"start": v(-91, -49.5) * mm, "end": v(-77, -49.5) * mm});
            skLineSegment(sketch, "E17.6.7.3", {"start": v(-91, -63.5) * mm, "end": v(-91, -49.5) * mm});
            skLineSegment(sketch, "E17.9.7.3", {"start": v(-77, -63.5) * mm, "end": v(-77, -49.5) * mm});
            skLineSegment(sketch, "E17.0.7.4", {"start": v(-91, -35.5) * mm, "end": v(-77, -35.5) * mm});
            skLineSegment(sketch, "E17.3.7.4", {"start": v(-91, -21.5) * mm, "end": v(-77, -21.5) * mm});
            skLineSegment(sketch, "E17.6.7.4", {"start": v(-91, -35.5) * mm, "end": v(-91, -21.5) * mm});
            skLineSegment(sketch, "E17.9.7.4", {"start": v(-77, -35.5) * mm, "end": v(-77, -21.5) * mm});
            skLineSegment(sketch, "E17.0.7.5", {"start": v(-91, -7.5) * mm, "end": v(-77, -7.5) * mm});
            skLineSegment(sketch, "E17.3.7.5", {"start": v(-91, 6.5) * mm, "end": v(-77, 6.5) * mm});
            skLineSegment(sketch, "E17.6.7.5", {"start": v(-91, -7.5) * mm, "end": v(-91, 6.5) * mm});
            skLineSegment(sketch, "E17.9.7.5", {"start": v(-77, -7.5) * mm, "end": v(-77, 6.5) * mm});
            skLineSegment(sketch, "E17.0.7.6", {"start": v(-91, 20.5) * mm, "end": v(-77, 20.5) * mm});
            skLineSegment(sketch, "E17.3.7.6", {"start": v(-91, 34.5) * mm, "end": v(-77, 34.5) * mm});
            skLineSegment(sketch, "E17.6.7.6", {"start": v(-91, 20.5) * mm, "end": v(-91, 34.5) * mm});
            skLineSegment(sketch, "E17.9.7.6", {"start": v(-77, 20.5) * mm, "end": v(-77, 34.5) * mm});
            skLineSegment(sketch, "E17.0.7.7", {"start": v(-91, 48.5) * mm, "end": v(-77, 48.5) * mm});
            skLineSegment(sketch, "E17.3.7.7", {"start": v(-91, 62.5) * mm, "end": v(-77, 62.5) * mm});
            skLineSegment(sketch, "E17.6.7.7", {"start": v(-91, 48.5) * mm, "end": v(-91, 62.5) * mm});
            skLineSegment(sketch, "E17.9.7.7", {"start": v(-77, 48.5) * mm, "end": v(-77, 62.5) * mm});
            skLineSegment(sketch, "E17.0.7.8", {"start": v(-91, 76.5) * mm, "end": v(-77, 76.5) * mm});
            skLineSegment(sketch, "E17.3.7.8", {"start": v(-91, 90.5) * mm, "end": v(-77, 90.5) * mm});
            skLineSegment(sketch, "E17.6.7.8", {"start": v(-91, 76.5) * mm, "end": v(-91, 90.5) * mm});
            skLineSegment(sketch, "E17.9.7.8", {"start": v(-77, 76.5) * mm, "end": v(-77, 90.5) * mm});
            skLineSegment(sketch, "E17.0.7.9", {"start": v(-91, 104.5) * mm, "end": v(-77, 104.5) * mm});
            skLineSegment(sketch, "E17.3.7.9", {"start": v(-91, 118.5) * mm, "end": v(-77, 118.5) * mm});
            skLineSegment(sketch, "E17.6.7.9", {"start": v(-91, 104.5) * mm, "end": v(-91, 118.5) * mm});
            skLineSegment(sketch, "E17.9.7.9", {"start": v(-77, 104.5) * mm, "end": v(-77, 118.5) * mm});
            skLineSegment(sketch, "E17.0.7.10", {"start": v(-91, 132.5) * mm, "end": v(-77, 132.5) * mm});
            skLineSegment(sketch, "E17.3.7.10", {"start": v(-91, 146.5) * mm, "end": v(-77, 146.5) * mm});
            skLineSegment(sketch, "E17.6.7.10", {"start": v(-91, 132.5) * mm, "end": v(-91, 146.5) * mm});
            skLineSegment(sketch, "E17.9.7.10", {"start": v(-77, 132.5) * mm, "end": v(-77, 146.5) * mm});
            skLineSegment(sketch, "E17.0.8.0", {"start": v(-119, -147.5) * mm, "end": v(-105, -147.5) * mm});
            skLineSegment(sketch, "E17.3.8.0", {"start": v(-119, -133.5) * mm, "end": v(-105, -133.5) * mm});
            skLineSegment(sketch, "E17.6.8.0", {"start": v(-119, -147.5) * mm, "end": v(-119, -133.5) * mm});
            skLineSegment(sketch, "E17.9.8.0", {"start": v(-105, -147.5) * mm, "end": v(-105, -133.5) * mm});
            skLineSegment(sketch, "E17.0.8.1", {"start": v(-119, -119.5) * mm, "end": v(-105, -119.5) * mm});
            skLineSegment(sketch, "E17.3.8.1", {"start": v(-119, -105.5) * mm, "end": v(-105, -105.5) * mm});
            skLineSegment(sketch, "E17.6.8.1", {"start": v(-119, -119.5) * mm, "end": v(-119, -105.5) * mm});
            skLineSegment(sketch, "E17.9.8.1", {"start": v(-105, -119.5) * mm, "end": v(-105, -105.5) * mm});
            skLineSegment(sketch, "E17.0.8.2", {"start": v(-119, -91.5) * mm, "end": v(-105, -91.5) * mm});
            skLineSegment(sketch, "E17.3.8.2", {"start": v(-119, -77.5) * mm, "end": v(-105, -77.5) * mm});
            skLineSegment(sketch, "E17.6.8.2", {"start": v(-119, -91.5) * mm, "end": v(-119, -77.5) * mm});
            skLineSegment(sketch, "E17.9.8.2", {"start": v(-105, -91.5) * mm, "end": v(-105, -77.5) * mm});
            skLineSegment(sketch, "E17.0.8.3", {"start": v(-119, -63.5) * mm, "end": v(-105, -63.5) * mm});
            skLineSegment(sketch, "E17.3.8.3", {"start": v(-119, -49.5) * mm, "end": v(-105, -49.5) * mm});
            skLineSegment(sketch, "E17.6.8.3", {"start": v(-119, -63.5) * mm, "end": v(-119, -49.5) * mm});
            skLineSegment(sketch, "E17.9.8.3", {"start": v(-105, -63.5) * mm, "end": v(-105, -49.5) * mm});
            skLineSegment(sketch, "E17.0.8.4", {"start": v(-119, -35.5) * mm, "end": v(-105, -35.5) * mm});
            skLineSegment(sketch, "E17.3.8.4", {"start": v(-119, -21.5) * mm, "end": v(-105, -21.5) * mm});
            skLineSegment(sketch, "E17.6.8.4", {"start": v(-119, -35.5) * mm, "end": v(-119, -21.5) * mm});
            skLineSegment(sketch, "E17.9.8.4", {"start": v(-105, -35.5) * mm, "end": v(-105, -21.5) * mm});
            skLineSegment(sketch, "E17.0.8.5", {"start": v(-119, -7.5) * mm, "end": v(-105, -7.5) * mm});
            skLineSegment(sketch, "E17.3.8.5", {"start": v(-119, 6.5) * mm, "end": v(-105, 6.5) * mm});
            skLineSegment(sketch, "E17.6.8.5", {"start": v(-119, -7.5) * mm, "end": v(-119, 6.5) * mm});
            skLineSegment(sketch, "E17.9.8.5", {"start": v(-105, -7.5) * mm, "end": v(-105, 6.5) * mm});
            skLineSegment(sketch, "E17.0.8.6", {"start": v(-119, 20.5) * mm, "end": v(-105, 20.5) * mm});
            skLineSegment(sketch, "E17.3.8.6", {"start": v(-119, 34.5) * mm, "end": v(-105, 34.5) * mm});
            skLineSegment(sketch, "E17.6.8.6", {"start": v(-119, 20.5) * mm, "end": v(-119, 34.5) * mm});
            skLineSegment(sketch, "E17.9.8.6", {"start": v(-105, 20.5) * mm, "end": v(-105, 34.5) * mm});
            skLineSegment(sketch, "E17.0.8.7", {"start": v(-119, 48.5) * mm, "end": v(-105, 48.5) * mm});
            skLineSegment(sketch, "E17.3.8.7", {"start": v(-119, 62.5) * mm, "end": v(-105, 62.5) * mm});
            skLineSegment(sketch, "E17.6.8.7", {"start": v(-119, 48.5) * mm, "end": v(-119, 62.5) * mm});
            skLineSegment(sketch, "E17.9.8.7", {"start": v(-105, 48.5) * mm, "end": v(-105, 62.5) * mm});
            skLineSegment(sketch, "E17.0.8.8", {"start": v(-119, 76.5) * mm, "end": v(-105, 76.5) * mm});
            skLineSegment(sketch, "E17.3.8.8", {"start": v(-119, 90.5) * mm, "end": v(-105, 90.5) * mm});
            skLineSegment(sketch, "E17.6.8.8", {"start": v(-119, 76.5) * mm, "end": v(-119, 90.5) * mm});
            skLineSegment(sketch, "E17.9.8.8", {"start": v(-105, 76.5) * mm, "end": v(-105, 90.5) * mm});
            skLineSegment(sketch, "E17.0.8.9", {"start": v(-119, 104.5) * mm, "end": v(-105, 104.5) * mm});
            skLineSegment(sketch, "E17.3.8.9", {"start": v(-119, 118.5) * mm, "end": v(-105, 118.5) * mm});
            skLineSegment(sketch, "E17.6.8.9", {"start": v(-119, 104.5) * mm, "end": v(-119, 118.5) * mm});
            skLineSegment(sketch, "E17.9.8.9", {"start": v(-105, 104.5) * mm, "end": v(-105, 118.5) * mm});
            skLineSegment(sketch, "E17.0.8.10", {"start": v(-119, 132.5) * mm, "end": v(-105, 132.5) * mm});
            skLineSegment(sketch, "E17.3.8.10", {"start": v(-119, 146.5) * mm, "end": v(-105, 146.5) * mm});
            skLineSegment(sketch, "E17.6.8.10", {"start": v(-119, 132.5) * mm, "end": v(-119, 146.5) * mm});
            skLineSegment(sketch, "E17.9.8.10", {"start": v(-105, 132.5) * mm, "end": v(-105, 146.5) * mm});
            skPoint(sketch, "E18.endSnap0", {"position": v(0, 6.5) * mm});
            skSolve(sketch);
        }
        {
            var Q0;
            Q0=makeQuery(id+"F1.imprint","IMPRINT",FACE,{"disambiguationData":[TD([[makeQuery(id+"F1.imprint","IMPRINT",EDGE,{"derivedFrom":sQuery(id+"F1.wireOp",EDGE,"E1.bottom")}),1.0]])]});
            var sketch = newSketch(context, id + "F3", { "sketchPlane" : qUnion([Q0])});
            skLineSegment(sketch, "E19", {"start": v(-6.18, 5.4) * mm, "end": v(13.85, 5.4) * mm, "construction": true});
            skLineSegment(sketch, "E20", {"start": v(3.2, -2.42) * mm, "end": v(3.2, 13.1) * mm, "construction": true});
            skCircle(sketch, "E21", {"center": v(3.2, 5.4) * mm, "radius": 2.5 * mm});
            skCircle(sketch, "E22", {"center": v(3.2, 5.4) * mm, "radius": 5 * mm});
            skSolve(sketch);
        }
        {
            var Q0;
            Q0=makeQuery(id+"F0.imprint","IMPRINT",FACE,{"disambiguationData":[TD([[makeQuery(id+"F0.imprint","IMPRINT",EDGE,{"derivedFrom":sQuery(id+"F0.wireOp",EDGE,"E0.bottom")}),-1.0]])]});
            var sketch = newSketch(context, id + "F4", { "sketchPlane" : qUnion([Q0])});
            skArc(sketch, "E23", {"start": v(-110, 146.5) * mm, "mid": v(-108.54, 142.96) * mm, "end": v(-105, 141.5) * mm});
            skArc(sketch, "E24", {"start": v(-105, 151.5) * mm, "mid": v(-108.54, 150.04) * mm, "end": v(-110, 146.5) * mm, "construction": true});
            skArc(sketch, "E25", {"start": v(-105, 156.7) * mm, "mid": v(-112.21, 153.71) * mm, "end": v(-115.2, 146.5) * mm, "construction": true});
            skArc(sketch, "E26", {"start": v(-115.2, 146.5) * mm, "mid": v(-112.21, 139.29) * mm, "end": v(-105, 136.3) * mm});
            skArc(sketch, "E27", {"start": v(-105, 141.5) * mm, "mid": v(-101.47, 142.96) * mm, "end": v(-100, 146.5) * mm, "construction": true});
            skArc(sketch, "E28", {"start": v(-100, 146.5) * mm, "mid": v(-101.46, 150.03) * mm, "end": v(-105, 151.5) * mm});
            skLineSegment(sketch, "E29", {"start": v(-94.8, 146.5) * mm, "end": v(-94.8, 146.5) * mm});
            skLineSegment(sketch, "E30", {"start": v(-105, 136.3) * mm, "end": v(-105, 146.5) * mm, "construction": true});
            skArc(sketch, "E31", {"start": v(-105, 136.3) * mm, "mid": v(-97.79, 139.29) * mm, "end": v(-94.8, 146.5) * mm, "construction": true});
            skArc(sketch, "E32", {"start": v(-94.8, 146.5) * mm, "mid": v(-97.79, 153.71) * mm, "end": v(-105, 156.7) * mm});
            skLineSegment(sketch, "E33", {"start": v(-105, 136.3) * mm, "end": v(-105, 141.5) * mm});
            skLineSegment(sketch, "E34", {"start": v(-100, 146.5) * mm, "end": v(-94.8, 146.5) * mm});
            skLineSegment(sketch, "E35", {"start": v(-110, 146.5) * mm, "end": v(-115.2, 146.5) * mm});
            skLineSegment(sketch, "E36", {"start": v(-105, 151.5) * mm, "end": v(-105, 156.7) * mm});
            skArc(sketch, "E37", {"start": v(105, 141.5) * mm, "mid": v(108.54, 142.97) * mm, "end": v(110, 146.5) * mm});
            skArc(sketch, "E38", {"start": v(110, 146.5) * mm, "mid": v(108.54, 150.03) * mm, "end": v(105, 151.5) * mm, "construction": true});
            skArc(sketch, "E39", {"start": v(115.2, 146.5) * mm, "mid": v(112.22, 153.7) * mm, "end": v(105.02, 156.7) * mm, "construction": true});
            skArc(sketch, "E40", {"start": v(105, 136.3) * mm, "mid": v(112.21, 139.29) * mm, "end": v(115.2, 146.5) * mm});
            skArc(sketch, "E41", {"start": v(100, 146.5) * mm, "mid": v(101.47, 142.96) * mm, "end": v(105, 141.5) * mm, "construction": true});
            skArc(sketch, "E42", {"start": v(105, 151.5) * mm, "mid": v(101.46, 150.03) * mm, "end": v(100, 146.5) * mm});
            skLineSegment(sketch, "E43", {"start": v(105.02, 156.7) * mm, "end": v(105.02, 156.7) * mm});
            skArc(sketch, "E44", {"start": v(105.02, 156.7) * mm, "mid": v(97.8, 153.72) * mm, "end": v(94.8, 146.5) * mm});
            skArc(sketch, "E45", {"start": v(94.8, 146.5) * mm, "mid": v(97.79, 139.29) * mm, "end": v(105, 136.3) * mm, "construction": true});
            skArc(sketch, "E46", {"start": v(105, -152.5) * mm, "mid": v(108.52, -151.05) * mm, "end": v(110, -147.53) * mm, "construction": true});
            skArc(sketch, "E47", {"start": v(110, -147.53) * mm, "mid": v(108.55, -143.98) * mm, "end": v(105, -142.5) * mm});
            skLineSegment(sketch, "E48", {"start": v(100, -147.5) * mm, "end": v(100, -147.5) * mm});
            skArc(sketch, "E49", {"start": v(100, -147.5) * mm, "mid": v(101.46, -151.04) * mm, "end": v(105, -152.5) * mm});
            skArc(sketch, "E50", {"start": v(105, -142.5) * mm, "mid": v(101.46, -143.97) * mm, "end": v(100, -147.5) * mm, "construction": true});
            skArc(sketch, "E51", {"start": v(105, -137.3) * mm, "mid": v(97.79, -140.29) * mm, "end": v(94.8, -147.5) * mm, "construction": true});
            skArc(sketch, "E52", {"start": v(94.8, -147.5) * mm, "mid": v(97.8, -154.72) * mm, "end": v(105.02, -157.7) * mm});
            skArc(sketch, "E53", {"start": v(115.2, -147.51) * mm, "mid": v(112.22, -140.3) * mm, "end": v(105, -137.3) * mm});
            skLineSegment(sketch, "E54", {"start": v(105.02, -157.7) * mm, "end": v(105.02, -157.7) * mm});
            skArc(sketch, "E55", {"start": v(105.02, -157.7) * mm, "mid": v(112.21, -154.71) * mm, "end": v(115.2, -147.51) * mm, "construction": true});
            skLineSegment(sketch, "E56", {"start": v(105, 151.5) * mm, "end": v(105.02, 156.7) * mm});
            skLineSegment(sketch, "E57", {"start": v(105, 141.5) * mm, "end": v(105, 136.3) * mm});
            skLineSegment(sketch, "E58", {"start": v(110, 146.5) * mm, "end": v(115.2, 146.5) * mm});
            skLineSegment(sketch, "E59", {"start": v(100, 146.5) * mm, "end": v(94.8, 146.5) * mm});
            skLineSegment(sketch, "E60", {"start": v(110, -147.53) * mm, "end": v(115.2, -147.51) * mm});
            skLineSegment(sketch, "E61", {"start": v(105, -142.5) * mm, "end": v(105, -137.3) * mm});
            skArc(sketch, "E62", {"start": v(-105, -157.7) * mm, "mid": v(-97.8, -154.7) * mm, "end": v(-94.83, -147.5) * mm});
            skArc(sketch, "E63", {"start": v(-94.83, -147.5) * mm, "mid": v(-97.8, -140.3) * mm, "end": v(-105, -137.3) * mm, "construction": true});
            skArc(sketch, "E64", {"start": v(-105, -137.3) * mm, "mid": v(-112.23, -140.28) * mm, "end": v(-115.23, -147.5) * mm});
            skArc(sketch, "E65", {"start": v(-115.23, -147.5) * mm, "mid": v(-112.23, -154.72) * mm, "end": v(-105, -157.7) * mm, "construction": true});
            skArc(sketch, "E66", {"start": v(-110.03, -147.5) * mm, "mid": v(-108.55, -151.05) * mm, "end": v(-105, -152.5) * mm, "construction": true});
            skArc(sketch, "E67", {"start": v(-105, -142.5) * mm, "mid": v(-108.55, -143.96) * mm, "end": v(-110.03, -147.5) * mm});
            skArc(sketch, "E68", {"start": v(-100.03, -147.5) * mm, "mid": v(-101.48, -143.97) * mm, "end": v(-105, -142.5) * mm, "construction": true});
            skArc(sketch, "E69", {"start": v(-105, -152.5) * mm, "mid": v(-101.48, -151.03) * mm, "end": v(-100.03, -147.5) * mm});
            skLineSegment(sketch, "E70", {"start": v(-105, -157.7) * mm, "end": v(-105, -152.5) * mm});
            skLineSegment(sketch, "E71", {"start": v(-100.03, -147.5) * mm, "end": v(-94.83, -147.5) * mm});
            skLineSegment(sketch, "E72", {"start": v(-105, -142.5) * mm, "end": v(-105, -137.3) * mm});
            skLineSegment(sketch, "E73", {"start": v(-115.23, -147.5) * mm, "end": v(-110.03, -147.5) * mm});
            skLineSegment(sketch, "E74", {"start": v(105.02, -157.7) * mm, "end": v(105, -152.5) * mm});
            skLineSegment(sketch, "E75", {"start": v(94.8, -147.5) * mm, "end": v(100, -147.5) * mm});
            skSolve(sketch);
        }
        {
            var Q0;
            Q0=makeQuery(id+"F1.imprint","IMPRINT",FACE,{"disambiguationData":[TD([[makeQuery(id+"F1.imprint","IMPRINT",EDGE,{"derivedFrom":sQuery(id+"F1.wireOp",EDGE,"E8.0.7.0")}),1.0]])]});
            var Q1;
            Q1=makeQuery(id+"F1.imprint","IMPRINT",FACE,{"disambiguationData":[TD([[makeQuery(id+"F1.imprint","IMPRINT",EDGE,{"derivedFrom":sQuery(id+"F1.wireOp",EDGE,"E7.0.0.4")}),1.0]])]});
            var Q2;
            Q2=makeQuery(id+"F1.imprint","IMPRINT",FACE,{"disambiguationData":[TD([[makeQuery(id+"F1.imprint","IMPRINT",EDGE,{"derivedFrom":sQuery(id+"F1.wireOp",EDGE,"E6.0.5.5")}),1.0]])]});
            var Q3;
            Q3=makeQuery(id+"F1.imprint","IMPRINT",FACE,{"disambiguationData":[TD([[makeQuery(id+"F1.imprint","IMPRINT",EDGE,{"derivedFrom":sQuery(id+"F1.wireOp",EDGE,"E6.0.2.3")}),1.0]])]});
            var Q4;
            Q4=makeQuery(id+"F1.imprint","IMPRINT",FACE,{"disambiguationData":[TD([[makeQuery(id+"F1.imprint","IMPRINT",EDGE,{"derivedFrom":sQuery(id+"F1.wireOp",EDGE,"E8.0.6.10")}),1.0]])]});
            var Q5;
            Q5=makeQuery(id+"F1.imprint","IMPRINT",FACE,{"disambiguationData":[TD([[makeQuery(id+"F1.imprint","IMPRINT",EDGE,{"derivedFrom":sQuery(id+"F1.wireOp",EDGE,"E6.0.3.1")}),1.0]])]});
            var Q6;
            Q6=makeQuery(id+"F1.imprint","IMPRINT",FACE,{"disambiguationData":[TD([[makeQuery(id+"F1.imprint","IMPRINT",EDGE,{"derivedFrom":sQuery(id+"F1.wireOp",EDGE,"E6.0.2.4")}),1.0]])]});
            var Q7;
            Q7=makeQuery(id+"F1.imprint","IMPRINT",FACE,{"disambiguationData":[TD([[makeQuery(id+"F1.imprint","IMPRINT",EDGE,{"derivedFrom":sQuery(id+"F1.wireOp",EDGE,"E8.0.6.6")}),1.0]])]});
            var Q8;
            Q8=makeQuery(id+"F1.imprint","IMPRINT",FACE,{"disambiguationData":[TD([[makeQuery(id+"F1.imprint","IMPRINT",EDGE,{"derivedFrom":sQuery(id+"F1.wireOp",EDGE,"E7.0.0.5")}),1.0]])]});
            var Q9;
            Q9=makeQuery(id+"F1.imprint","IMPRINT",FACE,{"disambiguationData":[TD([[makeQuery(id+"F1.imprint","IMPRINT",EDGE,{"derivedFrom":sQuery(id+"F1.wireOp",EDGE,"E8.0.3.1")}),1.0]])]});
            var Q10;
            Q10=makeQuery(id+"F1.imprint","IMPRINT",FACE,{"disambiguationData":[TD([[makeQuery(id+"F1.imprint","IMPRINT",EDGE,{"derivedFrom":sQuery(id+"F1.wireOp",EDGE,"E6.0.0.4")}),1.0]])]});
            var Q11;
            Q11=makeQuery(id+"F1.imprint","IMPRINT",FACE,{"disambiguationData":[TD([[makeQuery(id+"F1.imprint","IMPRINT",EDGE,{"derivedFrom":sQuery(id+"F1.wireOp",EDGE,"E6.0.0.1")}),1.0]])]});
            var Q12;
            Q12=makeQuery(id+"F1.imprint","IMPRINT",FACE,{"disambiguationData":[TD([[makeQuery(id+"F1.imprint","IMPRINT",EDGE,{"derivedFrom":sQuery(id+"F1.wireOp",EDGE,"E6.0.4.3")}),1.0]])]});
            var Q13;
            Q13=makeQuery(id+"F1.imprint","IMPRINT",FACE,{"disambiguationData":[TD([[makeQuery(id+"F1.imprint","IMPRINT",EDGE,{"derivedFrom":sQuery(id+"F1.wireOp",EDGE,"E8.0.1.1")}),1.0]])]});
            var Q14;
            Q14=makeQuery(id+"F1.imprint","IMPRINT",FACE,{"disambiguationData":[TD([[makeQuery(id+"F1.imprint","IMPRINT",EDGE,{"derivedFrom":sQuery(id+"F1.wireOp",EDGE,"E8.0.1.10")}),1.0]])]});
            var Q15;
            Q15=makeQuery(id+"F1.imprint","IMPRINT",FACE,{"disambiguationData":[TD([[makeQuery(id+"F1.imprint","IMPRINT",EDGE,{"derivedFrom":sQuery(id+"F1.wireOp",EDGE,"E6.0.8.7")}),1.0]])]});
            var Q16;
            Q16=makeQuery(id+"F1.imprint","IMPRINT",FACE,{"disambiguationData":[TD([[makeQuery(id+"F1.imprint","IMPRINT",EDGE,{"derivedFrom":sQuery(id+"F1.wireOp",EDGE,"E8.0.3.4")}),1.0]])]});
            var Q17;
            Q17=makeQuery(id+"F1.imprint","IMPRINT",FACE,{"disambiguationData":[TD([[makeQuery(id+"F1.imprint","IMPRINT",EDGE,{"derivedFrom":sQuery(id+"F1.wireOp",EDGE,"E6.0.1.3")}),1.0]])]});
            var Q18;
            Q18=makeQuery(id+"F1.imprint","IMPRINT",FACE,{"disambiguationData":[TD([[makeQuery(id+"F1.imprint","IMPRINT",EDGE,{"derivedFrom":sQuery(id+"F1.wireOp",EDGE,"E8.0.6.9")}),1.0]])]});
            var Q19;
            Q19=makeQuery(id+"F1.imprint","IMPRINT",FACE,{"disambiguationData":[TD([[makeQuery(id+"F1.imprint","IMPRINT",EDGE,{"derivedFrom":sQuery(id+"F1.wireOp",EDGE,"E8.0.6.2")}),1.0]])]});
            var Q20;
            Q20=makeQuery(id+"F1.imprint","IMPRINT",FACE,{"disambiguationData":[TD([[makeQuery(id+"F1.imprint","IMPRINT",EDGE,{"derivedFrom":sQuery(id+"F1.wireOp",EDGE,"E6.0.8.2")}),1.0]])]});
            var Q21;
            Q21=makeQuery(id+"F1.imprint","IMPRINT",FACE,{"disambiguationData":[TD([[makeQuery(id+"F1.imprint","IMPRINT",EDGE,{"derivedFrom":sQuery(id+"F1.wireOp",EDGE,"E8.0.7.3")}),1.0]])]});
            var Q22;
            Q22=makeQuery(id+"F1.imprint","IMPRINT",FACE,{"disambiguationData":[TD([[makeQuery(id+"F1.imprint","IMPRINT",EDGE,{"derivedFrom":sQuery(id+"F1.wireOp",EDGE,"E8.0.2.6")}),1.0]])]});
            var Q23;
            Q23=makeQuery(id+"F1.imprint","IMPRINT",FACE,{"disambiguationData":[TD([[makeQuery(id+"F1.imprint","IMPRINT",EDGE,{"derivedFrom":sQuery(id+"F1.wireOp",EDGE,"E6.0.6.4")}),1.0]])]});
            var Q24;
            Q24=makeQuery(id+"F1.imprint","IMPRINT",FACE,{"disambiguationData":[TD([[makeQuery(id+"F1.imprint","IMPRINT",EDGE,{"derivedFrom":sQuery(id+"F1.wireOp",EDGE,"E8.0.1.3")}),1.0]])]});
            var Q25;
            Q25=makeQuery(id+"F1.imprint","IMPRINT",FACE,{"disambiguationData":[TD([[makeQuery(id+"F1.imprint","IMPRINT",EDGE,{"derivedFrom":sQuery(id+"F1.wireOp",EDGE,"E8.0.2.2")}),1.0]])]});
            var Q26;
            Q26=makeQuery(id+"F1.imprint","IMPRINT",FACE,{"disambiguationData":[TD([[makeQuery(id+"F1.imprint","IMPRINT",EDGE,{"derivedFrom":sQuery(id+"F1.wireOp",EDGE,"E8.0.6.0")}),1.0]])]});
            var Q27;
            Q27=makeQuery(id+"F1.imprint","IMPRINT",FACE,{"disambiguationData":[TD([[makeQuery(id+"F1.imprint","IMPRINT",EDGE,{"derivedFrom":sQuery(id+"F1.wireOp",EDGE,"E7.0.0.8")}),1.0]])]});
            var Q28;
            Q28=makeQuery(id+"F1.imprint","IMPRINT",FACE,{"disambiguationData":[TD([[makeQuery(id+"F1.imprint","IMPRINT",EDGE,{"derivedFrom":sQuery(id+"F1.wireOp",EDGE,"E6.0.0.7")}),1.0]])]});
            var Q29;
            Q29=makeQuery(id+"F1.imprint","IMPRINT",FACE,{"disambiguationData":[TD([[makeQuery(id+"F1.imprint","IMPRINT",EDGE,{"derivedFrom":sQuery(id+"F1.wireOp",EDGE,"E6.0.8.1")}),1.0]])]});
            var Q30;
            Q30=makeQuery(id+"F1.imprint","IMPRINT",FACE,{"disambiguationData":[TD([[makeQuery(id+"F1.imprint","IMPRINT",EDGE,{"derivedFrom":sQuery(id+"F1.wireOp",EDGE,"E6.0.1.11")}),1.0]])]});
            var Q31;
            Q31=makeQuery(id+"F1.imprint","IMPRINT",FACE,{"disambiguationData":[TD([[makeQuery(id+"F1.imprint","IMPRINT",EDGE,{"derivedFrom":sQuery(id+"F1.wireOp",EDGE,"E8.0.3.7")}),1.0]])]});
            var Q32;
            Q32=makeQuery(id+"F1.imprint","IMPRINT",FACE,{"disambiguationData":[TD([[makeQuery(id+"F1.imprint","IMPRINT",EDGE,{"derivedFrom":sQuery(id+"F1.wireOp",EDGE,"E8.0.2.10")}),1.0]])]});
            var Q33;
            Q33=makeQuery(id+"F1.imprint","IMPRINT",FACE,{"disambiguationData":[TD([[makeQuery(id+"F1.imprint","IMPRINT",EDGE,{"derivedFrom":sQuery(id+"F1.wireOp",EDGE,"E6.0.6.3")}),1.0]])]});
            var Q34;
            Q34=makeQuery(id+"F1.imprint","IMPRINT",FACE,{"disambiguationData":[TD([[makeQuery(id+"F1.imprint","IMPRINT",EDGE,{"derivedFrom":sQuery(id+"F1.wireOp",EDGE,"E8.0.1.9")}),1.0]])]});
            var Q35;
            Q35=makeQuery(id+"F1.imprint","IMPRINT",FACE,{"disambiguationData":[TD([[makeQuery(id+"F1.imprint","IMPRINT",EDGE,{"derivedFrom":sQuery(id+"F1.wireOp",EDGE,"E6.0.7.3")}),1.0]])]});
            var Q36;
            Q36=makeQuery(id+"F1.imprint","IMPRINT",FACE,{"disambiguationData":[TD([[makeQuery(id+"F1.imprint","IMPRINT",EDGE,{"derivedFrom":sQuery(id+"F1.wireOp",EDGE,"E5.0.5.0")}),1.0]])]});
            var Q37;
            Q37=makeQuery(id+"F1.imprint","IMPRINT",FACE,{"disambiguationData":[TD([[makeQuery(id+"F1.imprint","IMPRINT",EDGE,{"derivedFrom":sQuery(id+"F1.wireOp",EDGE,"E6.0.3.9")}),1.0]])]});
            var Q38;
            Q38=makeQuery(id+"F1.imprint","IMPRINT",FACE,{"disambiguationData":[TD([[makeQuery(id+"F1.imprint","IMPRINT",EDGE,{"derivedFrom":sQuery(id+"F1.wireOp",EDGE,"E6.0.1.1")}),1.0]])]});
            var Q39;
            Q39=makeQuery(id+"F1.imprint","IMPRINT",FACE,{"disambiguationData":[TD([[makeQuery(id+"F1.imprint","IMPRINT",EDGE,{"derivedFrom":sQuery(id+"F1.wireOp",EDGE,"E5.0.6.0")}),1.0]])]});
            var Q40;
            Q40=makeQuery(id+"F1.imprint","IMPRINT",FACE,{"disambiguationData":[TD([[makeQuery(id+"F1.imprint","IMPRINT",EDGE,{"derivedFrom":sQuery(id+"F1.wireOp",EDGE,"E6.0.6.1")}),1.0]])]});
            var Q41;
            Q41=makeQuery(id+"F1.imprint","IMPRINT",FACE,{"disambiguationData":[TD([[makeQuery(id+"F1.imprint","IMPRINT",EDGE,{"derivedFrom":sQuery(id+"F1.wireOp",EDGE,"E6.0.2.9")}),1.0]])]});
            var Q42;
            Q42=makeQuery(id+"F1.imprint","IMPRINT",FACE,{"disambiguationData":[TD([[makeQuery(id+"F1.imprint","IMPRINT",EDGE,{"derivedFrom":sQuery(id+"F1.wireOp",EDGE,"E6.0.5.11")}),1.0]])]});
            var Q43;
            Q43=makeQuery(id+"F1.imprint","IMPRINT",FACE,{"disambiguationData":[TD([[makeQuery(id+"F1.imprint","IMPRINT",EDGE,{"derivedFrom":sQuery(id+"F1.wireOp",EDGE,"E6.0.2.5")}),1.0]])]});
            var Q44;
            Q44=makeQuery(id+"F1.imprint","IMPRINT",FACE,{"disambiguationData":[TD([[makeQuery(id+"F1.imprint","IMPRINT",EDGE,{"derivedFrom":sQuery(id+"F1.wireOp",EDGE,"E8.0.1.6")}),1.0]])]});
            var Q45;
            Q45=makeQuery(id+"F1.imprint","IMPRINT",FACE,{"disambiguationData":[TD([[makeQuery(id+"F1.imprint","IMPRINT",EDGE,{"derivedFrom":sQuery(id+"F1.wireOp",EDGE,"E6.0.0.6")}),1.0]])]});
            var Q46;
            Q46=makeQuery(id+"F1.imprint","IMPRINT",FACE,{"disambiguationData":[TD([[makeQuery(id+"F1.imprint","IMPRINT",EDGE,{"derivedFrom":sQuery(id+"F1.wireOp",EDGE,"E6.0.2.2")}),1.0]])]});
            var Q47;
            Q47=makeQuery(id+"F1.imprint","IMPRINT",FACE,{"disambiguationData":[TD([[makeQuery(id+"F1.imprint","IMPRINT",EDGE,{"derivedFrom":sQuery(id+"F1.wireOp",EDGE,"E7.0.0.2")}),1.0]])]});
            var Q48;
            Q48=makeQuery(id+"F1.imprint","IMPRINT",FACE,{"disambiguationData":[TD([[makeQuery(id+"F1.imprint","IMPRINT",EDGE,{"derivedFrom":sQuery(id+"F1.wireOp",EDGE,"E6.0.4.5")}),1.0]])]});
            var Q49;
            Q49=makeQuery(id+"F1.imprint","IMPRINT",FACE,{"disambiguationData":[TD([[makeQuery(id+"F1.imprint","IMPRINT",EDGE,{"derivedFrom":sQuery(id+"F1.wireOp",EDGE,"E6.0.7.2")}),1.0]])]});
            var Q50;
            Q50=makeQuery(id+"F1.imprint","IMPRINT",FACE,{"disambiguationData":[TD([[makeQuery(id+"F1.imprint","IMPRINT",EDGE,{"derivedFrom":sQuery(id+"F1.wireOp",EDGE,"E7.0.0.7")}),1.0]])]});
            var Q51;
            Q51=makeQuery(id+"F1.imprint","IMPRINT",FACE,{"disambiguationData":[TD([[makeQuery(id+"F1.imprint","IMPRINT",EDGE,{"derivedFrom":sQuery(id+"F1.wireOp",EDGE,"E8.0.5.2")}),1.0]])]});
            var Q52;
            Q52=makeQuery(id+"F1.imprint","IMPRINT",FACE,{"disambiguationData":[TD([[makeQuery(id+"F1.imprint","IMPRINT",EDGE,{"derivedFrom":sQuery(id+"F1.wireOp",EDGE,"E8.0.4.6")}),1.0]])]});
            var Q53;
            Q53=makeQuery(id+"F1.imprint","IMPRINT",FACE,{"disambiguationData":[TD([[makeQuery(id+"F1.imprint","IMPRINT",EDGE,{"derivedFrom":sQuery(id+"F1.wireOp",EDGE,"E8.0.3.8")}),1.0]])]});
            var Q54;
            Q54=makeQuery(id+"F1.imprint","IMPRINT",FACE,{"disambiguationData":[TD([[makeQuery(id+"F1.imprint","IMPRINT",EDGE,{"derivedFrom":sQuery(id+"F1.wireOp",EDGE,"E6.0.4.6")}),1.0]])]});
            var Q55;
            Q55=makeQuery(id+"F1.imprint","IMPRINT",FACE,{"disambiguationData":[TD([[makeQuery(id+"F1.imprint","IMPRINT",EDGE,{"derivedFrom":sQuery(id+"F1.wireOp",EDGE,"E6.0.6.6")}),1.0]])]});
            var Q56;
            Q56=makeQuery(id+"F1.imprint","IMPRINT",FACE,{"disambiguationData":[TD([[makeQuery(id+"F1.imprint","IMPRINT",EDGE,{"derivedFrom":sQuery(id+"F1.wireOp",EDGE,"E6.0.4.10")}),1.0]])]});
            var Q57;
            Q57=makeQuery(id+"F1.imprint","IMPRINT",FACE,{"disambiguationData":[TD([[makeQuery(id+"F1.imprint","IMPRINT",EDGE,{"derivedFrom":sQuery(id+"F1.wireOp",EDGE,"E8.0.1.5")}),1.0]])]});
            var Q58;
            Q58=makeQuery(id+"F1.imprint","IMPRINT",FACE,{"disambiguationData":[TD([[makeQuery(id+"F1.imprint","IMPRINT",EDGE,{"derivedFrom":sQuery(id+"F1.wireOp",EDGE,"E6.0.7.7")}),1.0]])]});
            var Q59;
            Q59=makeQuery(id+"F1.imprint","IMPRINT",FACE,{"disambiguationData":[TD([[makeQuery(id+"F1.imprint","IMPRINT",EDGE,{"derivedFrom":sQuery(id+"F1.wireOp",EDGE,"E8.0.3.5")}),1.0]])]});
            var Q60;
            Q60=makeQuery(id+"F1.imprint","IMPRINT",FACE,{"disambiguationData":[TD([[makeQuery(id+"F1.imprint","IMPRINT",EDGE,{"derivedFrom":sQuery(id+"F1.wireOp",EDGE,"E8.0.6.5")}),1.0]])]});
            var Q61;
            Q61=makeQuery(id+"F1.imprint","IMPRINT",FACE,{"disambiguationData":[TD([[makeQuery(id+"F1.imprint","IMPRINT",EDGE,{"derivedFrom":sQuery(id+"F1.wireOp",EDGE,"E6.0.5.7")}),1.0]])]});
            var Q62;
            Q62=makeQuery(id+"F1.imprint","IMPRINT",FACE,{"disambiguationData":[TD([[makeQuery(id+"F1.imprint","IMPRINT",EDGE,{"derivedFrom":sQuery(id+"F1.wireOp",EDGE,"E8.0.5.6")}),1.0]])]});
            var Q63;
            Q63=makeQuery(id+"F1.imprint","IMPRINT",FACE,{"disambiguationData":[TD([[makeQuery(id+"F1.imprint","IMPRINT",EDGE,{"derivedFrom":sQuery(id+"F1.wireOp",EDGE,"E8.0.6.8")}),1.0]])]});
            var Q64;
            Q64=makeQuery(id+"F1.imprint","IMPRINT",FACE,{"disambiguationData":[TD([[makeQuery(id+"F1.imprint","IMPRINT",EDGE,{"derivedFrom":sQuery(id+"F1.wireOp",EDGE,"E8.0.6.3")}),1.0]])]});
            var Q65;
            Q65=makeQuery(id+"F1.imprint","IMPRINT",FACE,{"disambiguationData":[TD([[makeQuery(id+"F1.imprint","IMPRINT",EDGE,{"derivedFrom":sQuery(id+"F1.wireOp",EDGE,"E8.0.5.4")}),1.0]])]});
            var Q66;
            Q66=makeQuery(id+"F1.imprint","IMPRINT",FACE,{"disambiguationData":[TD([[makeQuery(id+"F1.imprint","IMPRINT",EDGE,{"derivedFrom":sQuery(id+"F1.wireOp",EDGE,"E8.0.5.1")}),1.0]])]});
            var Q67;
            Q67=makeQuery(id+"F1.imprint","IMPRINT",FACE,{"disambiguationData":[TD([[makeQuery(id+"F1.imprint","IMPRINT",EDGE,{"derivedFrom":sQuery(id+"F1.wireOp",EDGE,"E6.0.7.8")}),1.0]])]});
            var Q68;
            Q68=makeQuery(id+"F1.imprint","IMPRINT",FACE,{"disambiguationData":[TD([[makeQuery(id+"F1.imprint","IMPRINT",EDGE,{"derivedFrom":sQuery(id+"F1.wireOp",EDGE,"E6.0.5.9")}),1.0]])]});
            var Q69;
            Q69=makeQuery(id+"F1.imprint","IMPRINT",FACE,{"disambiguationData":[TD([[makeQuery(id+"F1.imprint","IMPRINT",EDGE,{"derivedFrom":sQuery(id+"F1.wireOp",EDGE,"E8.0.4.9")}),1.0]])]});
            var Q70;
            Q70=makeQuery(id+"F1.imprint","IMPRINT",FACE,{"disambiguationData":[TD([[makeQuery(id+"F1.imprint","IMPRINT",EDGE,{"derivedFrom":sQuery(id+"F1.wireOp",EDGE,"E8.0.6.7")}),1.0]])]});
            var Q71;
            Q71=makeQuery(id+"F1.imprint","IMPRINT",FACE,{"disambiguationData":[TD([[makeQuery(id+"F1.imprint","IMPRINT",EDGE,{"derivedFrom":sQuery(id+"F1.wireOp",EDGE,"E6.0.7.1")}),1.0]])]});
            var Q72;
            Q72=makeQuery(id+"F1.imprint","IMPRINT",FACE,{"disambiguationData":[TD([[makeQuery(id+"F1.imprint","IMPRINT",EDGE,{"derivedFrom":sQuery(id+"F1.wireOp",EDGE,"E6.0.3.8")}),1.0]])]});
            var Q73;
            Q73=makeQuery(id+"F1.imprint","IMPRINT",FACE,{"disambiguationData":[TD([[makeQuery(id+"F1.imprint","IMPRINT",EDGE,{"derivedFrom":sQuery(id+"F1.wireOp",EDGE,"E6.0.8.6")}),1.0]])]});
            var Q74;
            Q74=makeQuery(id+"F1.imprint","IMPRINT",FACE,{"disambiguationData":[TD([[makeQuery(id+"F1.imprint","IMPRINT",EDGE,{"derivedFrom":sQuery(id+"F1.wireOp",EDGE,"E6.0.1.8")}),1.0]])]});
            var Q75;
            Q75=makeQuery(id+"F1.imprint","IMPRINT",FACE,{"disambiguationData":[TD([[makeQuery(id+"F1.imprint","IMPRINT",EDGE,{"derivedFrom":sQuery(id+"F1.wireOp",EDGE,"E6.0.8.5")}),1.0]])]});
            var Q76;
            Q76=makeQuery(id+"F1.imprint","IMPRINT",FACE,{"disambiguationData":[TD([[makeQuery(id+"F1.imprint","IMPRINT",EDGE,{"derivedFrom":sQuery(id+"F1.wireOp",EDGE,"E6.0.7.10")}),1.0]])]});
            var Q77;
            Q77=makeQuery(id+"F1.imprint","IMPRINT",FACE,{"disambiguationData":[TD([[makeQuery(id+"F1.imprint","IMPRINT",EDGE,{"derivedFrom":sQuery(id+"F1.wireOp",EDGE,"E6.0.0.2")}),1.0]])]});
            var Q78;
            Q78=makeQuery(id+"F1.imprint","IMPRINT",FACE,{"disambiguationData":[TD([[makeQuery(id+"F1.imprint","IMPRINT",EDGE,{"derivedFrom":sQuery(id+"F1.wireOp",EDGE,"E8.0.4.3")}),1.0]])]});
            var Q79;
            Q79=makeQuery(id+"F1.imprint","IMPRINT",FACE,{"disambiguationData":[TD([[makeQuery(id+"F1.imprint","IMPRINT",EDGE,{"derivedFrom":sQuery(id+"F1.wireOp",EDGE,"E8.0.6.1")}),1.0]])]});
            var Q80;
            Q80=makeQuery(id+"F1.imprint","IMPRINT",FACE,{"disambiguationData":[TD([[makeQuery(id+"F1.imprint","IMPRINT",EDGE,{"derivedFrom":sQuery(id+"F1.wireOp",EDGE,"E6.0.6.9")}),1.0]])]});
            var Q81;
            Q81=makeQuery(id+"F1.imprint","IMPRINT",FACE,{"disambiguationData":[TD([[makeQuery(id+"F1.imprint","IMPRINT",EDGE,{"derivedFrom":sQuery(id+"F1.wireOp",EDGE,"E6.0.3.7")}),1.0]])]});
            var Q82;
            Q82=makeQuery(id+"F1.imprint","IMPRINT",FACE,{"disambiguationData":[TD([[makeQuery(id+"F1.imprint","IMPRINT",EDGE,{"derivedFrom":sQuery(id+"F1.wireOp",EDGE,"E6.0.5.3")}),1.0]])]});
            var Q83;
            Q83=makeQuery(id+"F1.imprint","IMPRINT",FACE,{"disambiguationData":[TD([[makeQuery(id+"F1.imprint","IMPRINT",EDGE,{"derivedFrom":sQuery(id+"F1.wireOp",EDGE,"E7.0.0.10")}),1.0]])]});
            var Q84;
            Q84=makeQuery(id+"F1.imprint","IMPRINT",FACE,{"disambiguationData":[TD([[makeQuery(id+"F1.imprint","IMPRINT",EDGE,{"derivedFrom":sQuery(id+"F1.wireOp",EDGE,"E8.0.7.9")}),1.0]])]});
            var Q85;
            Q85=makeQuery(id+"F1.imprint","IMPRINT",FACE,{"disambiguationData":[TD([[makeQuery(id+"F1.imprint","IMPRINT",EDGE,{"derivedFrom":sQuery(id+"F1.wireOp",EDGE,"E8.0.3.0")}),1.0]])]});
            var Q86;
            Q86=makeQuery(id+"F1.imprint","IMPRINT",FACE,{"disambiguationData":[TD([[makeQuery(id+"F1.imprint","IMPRINT",EDGE,{"derivedFrom":sQuery(id+"F1.wireOp",EDGE,"E6.0.3.11")}),1.0]])]});
            var Q87;
            Q87=makeQuery(id+"F1.imprint","IMPRINT",FACE,{"disambiguationData":[TD([[makeQuery(id+"F1.imprint","IMPRINT",EDGE,{"derivedFrom":sQuery(id+"F1.wireOp",EDGE,"E6.0.8.8")}),1.0]])]});
            var Q88;
            Q88=makeQuery(id+"F1.imprint","IMPRINT",FACE,{"disambiguationData":[TD([[makeQuery(id+"F1.imprint","IMPRINT",EDGE,{"derivedFrom":sQuery(id+"F1.wireOp",EDGE,"E6.0.0.9")}),1.0]])]});
            var Q89;
            Q89=makeQuery(id+"F1.imprint","IMPRINT",FACE,{"disambiguationData":[TD([[makeQuery(id+"F1.imprint","IMPRINT",EDGE,{"derivedFrom":sQuery(id+"F1.wireOp",EDGE,"E8.0.1.0")}),1.0]])]});
            var Q90;
            Q90=makeQuery(id+"F1.imprint","IMPRINT",FACE,{"disambiguationData":[TD([[makeQuery(id+"F1.imprint","IMPRINT",EDGE,{"derivedFrom":sQuery(id+"F1.wireOp",EDGE,"E6.0.8.9")}),1.0]])]});
            var Q91;
            Q91=makeQuery(id+"F1.imprint","IMPRINT",FACE,{"disambiguationData":[TD([[makeQuery(id+"F1.imprint","IMPRINT",EDGE,{"derivedFrom":sQuery(id+"F1.wireOp",EDGE,"E6.0.4.9")}),1.0]])]});
            var Q92;
            Q92=makeQuery(id+"F1.imprint","IMPRINT",FACE,{"disambiguationData":[TD([[makeQuery(id+"F1.imprint","IMPRINT",EDGE,{"derivedFrom":sQuery(id+"F1.wireOp",EDGE,"E6.0.2.7")}),1.0]])]});
            var Q93;
            Q93=makeQuery(id+"F1.imprint","IMPRINT",FACE,{"disambiguationData":[TD([[makeQuery(id+"F1.imprint","IMPRINT",EDGE,{"derivedFrom":sQuery(id+"F1.wireOp",EDGE,"E8.0.5.9")}),1.0]])]});
            var Q94;
            Q94=makeQuery(id+"F1.imprint","IMPRINT",FACE,{"disambiguationData":[TD([[makeQuery(id+"F1.imprint","IMPRINT",EDGE,{"derivedFrom":sQuery(id+"F1.wireOp",EDGE,"E8.0.2.4")}),1.0]])]});
            var Q95;
            Q95=makeQuery(id+"F1.imprint","IMPRINT",FACE,{"disambiguationData":[TD([[makeQuery(id+"F1.imprint","IMPRINT",EDGE,{"derivedFrom":sQuery(id+"F1.wireOp",EDGE,"E8.0.4.2")}),1.0]])]});
            var Q96;
            Q96=makeQuery(id+"F1.imprint","IMPRINT",FACE,{"disambiguationData":[TD([[makeQuery(id+"F1.imprint","IMPRINT",EDGE,{"derivedFrom":sQuery(id+"F1.wireOp",EDGE,"E8.0.7.8")}),1.0]])]});
            var Q97;
            Q97=makeQuery(id+"F1.imprint","IMPRINT",FACE,{"disambiguationData":[TD([[makeQuery(id+"F1.imprint","IMPRINT",EDGE,{"derivedFrom":sQuery(id+"F1.wireOp",EDGE,"E8.0.4.5")}),1.0]])]});
            var Q98;
            Q98=makeQuery(id+"F1.imprint","IMPRINT",FACE,{"disambiguationData":[TD([[makeQuery(id+"F1.imprint","IMPRINT",EDGE,{"derivedFrom":sQuery(id+"F1.wireOp",EDGE,"E6.0.5.1")}),1.0]])]});
            var Q99;
            Q99=makeQuery(id+"F1.imprint","IMPRINT",FACE,{"disambiguationData":[TD([[makeQuery(id+"F1.imprint","IMPRINT",EDGE,{"derivedFrom":sQuery(id+"F1.wireOp",EDGE,"E8.0.6.4")}),1.0]])]});
            var Q100;
            Q100=makeQuery(id+"F1.imprint","IMPRINT",FACE,{"disambiguationData":[TD([[makeQuery(id+"F1.imprint","IMPRINT",EDGE,{"derivedFrom":sQuery(id+"F1.wireOp",EDGE,"E6.0.1.7")}),1.0]])]});
            var Q101;
            Q101=makeQuery(id+"F1.imprint","IMPRINT",FACE,{"disambiguationData":[TD([[makeQuery(id+"F1.imprint","IMPRINT",EDGE,{"derivedFrom":sQuery(id+"F1.wireOp",EDGE,"E8.0.1.2")}),1.0]])]});
            var Q102;
            Q102=makeQuery(id+"F1.imprint","IMPRINT",FACE,{"disambiguationData":[TD([[makeQuery(id+"F1.imprint","IMPRINT",EDGE,{"derivedFrom":sQuery(id+"F1.wireOp",EDGE,"E8.0.2.9")}),1.0]])]});
            var Q103;
            Q103=makeQuery(id+"F1.imprint","IMPRINT",FACE,{"disambiguationData":[TD([[makeQuery(id+"F1.imprint","IMPRINT",EDGE,{"derivedFrom":sQuery(id+"F1.wireOp",EDGE,"E6.0.6.5")}),1.0]])]});
            var Q104;
            Q104=makeQuery(id+"F1.imprint","IMPRINT",FACE,{"disambiguationData":[TD([[makeQuery(id+"F1.imprint","IMPRINT",EDGE,{"derivedFrom":sQuery(id+"F1.wireOp",EDGE,"E3.bottom")}),-1.0]])]});
            var Q105;
            Q105=makeQuery(id+"F1.imprint","IMPRINT",FACE,{"disambiguationData":[TD([[makeQuery(id+"F1.imprint","IMPRINT",EDGE,{"derivedFrom":sQuery(id+"F1.wireOp",EDGE,"E8.0.4.1")}),1.0]])]});
            var Q106;
            Q106=makeQuery(id+"F1.imprint","IMPRINT",FACE,{"disambiguationData":[TD([[makeQuery(id+"F1.imprint","IMPRINT",EDGE,{"derivedFrom":sQuery(id+"F1.wireOp",EDGE,"E8.0.2.3")}),1.0]])]});
            var Q107;
            Q107=makeQuery(id+"F1.imprint","IMPRINT",FACE,{"disambiguationData":[TD([[makeQuery(id+"F1.imprint","IMPRINT",EDGE,{"derivedFrom":sQuery(id+"F1.wireOp",EDGE,"E8.0.5.10")}),1.0]])]});
            var Q108;
            Q108=makeQuery(id+"F1.imprint","IMPRINT",FACE,{"disambiguationData":[TD([[makeQuery(id+"F1.imprint","IMPRINT",EDGE,{"derivedFrom":sQuery(id+"F1.wireOp",EDGE,"E8.0.4.0")}),1.0]])]});
            var Q109;
            Q109=makeQuery(id+"F1.imprint","IMPRINT",FACE,{"disambiguationData":[TD([[makeQuery(id+"F1.imprint","IMPRINT",EDGE,{"derivedFrom":sQuery(id+"F1.wireOp",EDGE,"E8.0.2.1")}),1.0]])]});
            var Q110;
            Q110=makeQuery(id+"F1.imprint","IMPRINT",FACE,{"disambiguationData":[TD([[makeQuery(id+"F1.imprint","IMPRINT",EDGE,{"derivedFrom":sQuery(id+"F1.wireOp",EDGE,"E7.0.0.3")}),1.0]])]});
            var Q111;
            Q111=makeQuery(id+"F1.imprint","IMPRINT",FACE,{"disambiguationData":[TD([[makeQuery(id+"F1.imprint","IMPRINT",EDGE,{"derivedFrom":sQuery(id+"F1.wireOp",EDGE,"E8.0.7.5")}),1.0]])]});
            var Q112;
            Q112=makeQuery(id+"F1.imprint","IMPRINT",FACE,{"disambiguationData":[TD([[makeQuery(id+"F1.imprint","IMPRINT",EDGE,{"derivedFrom":sQuery(id+"F1.wireOp",EDGE,"E6.0.5.6")}),1.0]])]});
            var Q113;
            Q113=makeQuery(id+"F1.imprint","IMPRINT",FACE,{"disambiguationData":[TD([[makeQuery(id+"F1.imprint","IMPRINT",EDGE,{"derivedFrom":sQuery(id+"F1.wireOp",EDGE,"E6.0.3.5")}),1.0]])]});
            var Q114;
            Q114=makeQuery(id+"F1.imprint","IMPRINT",FACE,{"disambiguationData":[TD([[makeQuery(id+"F1.imprint","IMPRINT",EDGE,{"derivedFrom":sQuery(id+"F1.wireOp",EDGE,"E6.0.2.1")}),1.0]])]});
            var Q115;
            Q115=makeQuery(id+"F1.imprint","IMPRINT",FACE,{"disambiguationData":[TD([[makeQuery(id+"F1.imprint","IMPRINT",EDGE,{"derivedFrom":sQuery(id+"F1.wireOp",EDGE,"E7.0.0.1")}),1.0]])]});
            var Q116;
            Q116=makeQuery(id+"F1.imprint","IMPRINT",FACE,{"disambiguationData":[TD([[makeQuery(id+"F1.imprint","IMPRINT",EDGE,{"derivedFrom":sQuery(id+"F1.wireOp",EDGE,"E8.0.7.4")}),1.0]])]});
            var Q117;
            Q117=makeQuery(id+"F1.imprint","IMPRINT",FACE,{"disambiguationData":[TD([[makeQuery(id+"F1.imprint","IMPRINT",EDGE,{"derivedFrom":sQuery(id+"F1.wireOp",EDGE,"E6.0.0.8")}),1.0]])]});
            var Q118;
            Q118=makeQuery(id+"F1.imprint","IMPRINT",FACE,{"disambiguationData":[TD([[makeQuery(id+"F1.imprint","IMPRINT",EDGE,{"derivedFrom":sQuery(id+"F1.wireOp",EDGE,"E7.0.0.9")}),1.0]])]});
            var Q119;
            Q119=makeQuery(id+"F1.imprint","IMPRINT",FACE,{"disambiguationData":[TD([[makeQuery(id+"F1.imprint","IMPRINT",EDGE,{"derivedFrom":sQuery(id+"F1.wireOp",EDGE,"E6.0.4.1")}),1.0]])]});
            var Q120;
            Q120=makeQuery(id+"F1.imprint","IMPRINT",FACE,{"disambiguationData":[TD([[makeQuery(id+"F1.imprint","IMPRINT",EDGE,{"derivedFrom":sQuery(id+"F1.wireOp",EDGE,"E6.0.6.2")}),1.0]])]});
            var Q121;
            Q121=makeQuery(id+"F1.imprint","IMPRINT",FACE,{"disambiguationData":[TD([[makeQuery(id+"F1.imprint","IMPRINT",EDGE,{"derivedFrom":sQuery(id+"F1.wireOp",EDGE,"E6.0.2.10")}),1.0]])]});
            var Q122;
            Q122=makeQuery(id+"F1.imprint","IMPRINT",FACE,{"disambiguationData":[TD([[makeQuery(id+"F1.imprint","IMPRINT",EDGE,{"derivedFrom":sQuery(id+"F1.wireOp",EDGE,"E8.0.3.10")}),1.0]])]});
            var Q123;
            Q123=makeQuery(id+"F1.imprint","IMPRINT",FACE,{"disambiguationData":[TD([[makeQuery(id+"F1.imprint","IMPRINT",EDGE,{"derivedFrom":sQuery(id+"F1.wireOp",EDGE,"E6.0.2.11")}),1.0]])]});
            var Q124;
            Q124=makeQuery(id+"F1.imprint","IMPRINT",FACE,{"disambiguationData":[TD([[makeQuery(id+"F1.imprint","IMPRINT",EDGE,{"derivedFrom":sQuery(id+"F1.wireOp",EDGE,"E6.0.7.6")}),1.0]])]});
            var Q125;
            Q125=makeQuery(id+"F1.imprint","IMPRINT",FACE,{"disambiguationData":[TD([[makeQuery(id+"F1.imprint","IMPRINT",EDGE,{"derivedFrom":sQuery(id+"F1.wireOp",EDGE,"E6.0.4.8")}),1.0]])]});
            var Q126;
            Q126=makeQuery(id+"F1.imprint","IMPRINT",FACE,{"disambiguationData":[TD([[makeQuery(id+"F1.imprint","IMPRINT",EDGE,{"derivedFrom":sQuery(id+"F1.wireOp",EDGE,"E6.0.7.5")}),1.0]])]});
            var Q127;
            Q127=makeQuery(id+"F1.imprint","IMPRINT",FACE,{"disambiguationData":[TD([[makeQuery(id+"F1.imprint","IMPRINT",EDGE,{"derivedFrom":sQuery(id+"F1.wireOp",EDGE,"E6.0.6.10")}),1.0]])]});
            var Q128;
            Q128=makeQuery(id+"F1.imprint","IMPRINT",FACE,{"disambiguationData":[TD([[makeQuery(id+"F1.imprint","IMPRINT",EDGE,{"derivedFrom":sQuery(id+"F1.wireOp",EDGE,"E6.0.4.11")}),1.0]])]});
            var Q129;
            Q129=makeQuery(id+"F1.imprint","IMPRINT",FACE,{"disambiguationData":[TD([[makeQuery(id+"F1.imprint","IMPRINT",EDGE,{"derivedFrom":sQuery(id+"F1.wireOp",EDGE,"E8.0.7.6")}),1.0]])]});
            var Q130;
            Q130=makeQuery(id+"F1.imprint","IMPRINT",FACE,{"disambiguationData":[TD([[makeQuery(id+"F1.imprint","IMPRINT",EDGE,{"derivedFrom":sQuery(id+"F1.wireOp",EDGE,"E6.0.7.4")}),1.0]])]});
            var Q131;
            Q131=makeQuery(id+"F1.imprint","IMPRINT",FACE,{"disambiguationData":[TD([[makeQuery(id+"F1.imprint","IMPRINT",EDGE,{"derivedFrom":sQuery(id+"F1.wireOp",EDGE,"E6.0.4.7")}),1.0]])]});
            var Q132;
            Q132=makeQuery(id+"F1.imprint","IMPRINT",FACE,{"disambiguationData":[TD([[makeQuery(id+"F1.imprint","IMPRINT",EDGE,{"derivedFrom":sQuery(id+"F1.wireOp",EDGE,"E8.0.5.8")}),1.0]])]});
            var Q133;
            Q133=makeQuery(id+"F1.imprint","IMPRINT",FACE,{"disambiguationData":[TD([[makeQuery(id+"F1.imprint","IMPRINT",EDGE,{"derivedFrom":sQuery(id+"F1.wireOp",EDGE,"E6.0.3.10")}),1.0]])]});
            var Q134;
            Q134=makeQuery(id+"F1.imprint","IMPRINT",FACE,{"disambiguationData":[TD([[makeQuery(id+"F1.imprint","IMPRINT",EDGE,{"derivedFrom":sQuery(id+"F1.wireOp",EDGE,"E6.0.5.8")}),1.0]])]});
            var Q135;
            Q135=makeQuery(id+"F1.imprint","IMPRINT",FACE,{"disambiguationData":[TD([[makeQuery(id+"F1.imprint","IMPRINT",EDGE,{"derivedFrom":sQuery(id+"F1.wireOp",EDGE,"E6.0.1.5")}),1.0]])]});
            var Q136;
            Q136=makeQuery(id+"F1.imprint","IMPRINT",FACE,{"disambiguationData":[TD([[makeQuery(id+"F1.imprint","IMPRINT",EDGE,{"derivedFrom":sQuery(id+"F1.wireOp",EDGE,"E6.0.0.10")}),1.0]])]});
            var Q137;
            Q137=makeQuery(id+"F1.imprint","IMPRINT",FACE,{"disambiguationData":[TD([[makeQuery(id+"F1.imprint","IMPRINT",EDGE,{"derivedFrom":sQuery(id+"F1.wireOp",EDGE,"E6.0.8.3")}),1.0]])]});
            var Q138;
            Q138=makeQuery(id+"F1.imprint","IMPRINT",FACE,{"disambiguationData":[TD([[makeQuery(id+"F1.imprint","IMPRINT",EDGE,{"derivedFrom":sQuery(id+"F1.wireOp",EDGE,"E6.0.2.6")}),1.0]])]});
            var Q139;
            Q139=makeQuery(id+"F1.imprint","IMPRINT",FACE,{"disambiguationData":[TD([[makeQuery(id+"F1.imprint","IMPRINT",EDGE,{"derivedFrom":sQuery(id+"F1.wireOp",EDGE,"E8.0.1.7")}),1.0]])]});
            var Q140;
            Q140=makeQuery(id+"F1.imprint","IMPRINT",FACE,{"disambiguationData":[TD([[makeQuery(id+"F1.imprint","IMPRINT",EDGE,{"derivedFrom":sQuery(id+"F1.wireOp",EDGE,"E7.0.0.6")}),1.0]])]});
            var Q141;
            Q141=makeQuery(id+"F1.imprint","IMPRINT",FACE,{"disambiguationData":[TD([[makeQuery(id+"F1.imprint","IMPRINT",EDGE,{"derivedFrom":sQuery(id+"F1.wireOp",EDGE,"E6.0.1.2")}),1.0]])]});
            var Q142;
            Q142=makeQuery(id+"F1.imprint","IMPRINT",FACE,{"disambiguationData":[TD([[makeQuery(id+"F1.imprint","IMPRINT",EDGE,{"derivedFrom":sQuery(id+"F1.wireOp",EDGE,"E8.0.2.8")}),1.0]])]});
            var Q143;
            Q143=makeQuery(id+"F1.imprint","IMPRINT",FACE,{"disambiguationData":[TD([[makeQuery(id+"F1.imprint","IMPRINT",EDGE,{"derivedFrom":sQuery(id+"F1.wireOp",EDGE,"E8.0.1.8")}),1.0]])]});
            var Q144;
            Q144=makeQuery(id+"F1.imprint","IMPRINT",FACE,{"disambiguationData":[TD([[makeQuery(id+"F1.imprint","IMPRINT",EDGE,{"derivedFrom":sQuery(id+"F1.wireOp",EDGE,"E8.0.4.4")}),1.0]])]});
            var Q145;
            Q145=makeQuery(id+"F1.imprint","IMPRINT",FACE,{"disambiguationData":[TD([[makeQuery(id+"F1.imprint","IMPRINT",EDGE,{"derivedFrom":sQuery(id+"F1.wireOp",EDGE,"E8.0.4.8")}),1.0]])]});
            var Q146;
            Q146=makeQuery(id+"F1.imprint","IMPRINT",FACE,{"disambiguationData":[TD([[makeQuery(id+"F1.imprint","IMPRINT",EDGE,{"derivedFrom":sQuery(id+"F1.wireOp",EDGE,"E6.0.1.4")}),1.0]])]});
            var Q147;
            Q147=makeQuery(id+"F1.imprint","IMPRINT",FACE,{"disambiguationData":[TD([[makeQuery(id+"F1.imprint","IMPRINT",EDGE,{"derivedFrom":sQuery(id+"F1.wireOp",EDGE,"E8.0.5.0")}),1.0]])]});
            var Q148;
            Q148=makeQuery(id+"F1.imprint","IMPRINT",FACE,{"disambiguationData":[TD([[makeQuery(id+"F1.imprint","IMPRINT",EDGE,{"derivedFrom":sQuery(id+"F1.wireOp",EDGE,"E6.0.7.11")}),1.0]])]});
            var Q149;
            Q149=makeQuery(id+"F1.imprint","IMPRINT",FACE,{"disambiguationData":[TD([[makeQuery(id+"F1.imprint","IMPRINT",EDGE,{"derivedFrom":sQuery(id+"F1.wireOp",EDGE,"E8.0.4.10")}),1.0]])]});
            var Q150;
            Q150=makeQuery(id+"F1.imprint","IMPRINT",FACE,{"disambiguationData":[TD([[makeQuery(id+"F1.imprint","IMPRINT",EDGE,{"derivedFrom":sQuery(id+"F1.wireOp",EDGE,"E8.0.3.3")}),1.0]])]});
            var Q151;
            Q151=makeQuery(id+"F1.imprint","IMPRINT",FACE,{"disambiguationData":[TD([[makeQuery(id+"F1.imprint","IMPRINT",EDGE,{"derivedFrom":sQuery(id+"F1.wireOp",EDGE,"E8.0.5.5")}),1.0]])]});
            var Q152;
            Q152=makeQuery(id+"F1.imprint","IMPRINT",FACE,{"disambiguationData":[TD([[makeQuery(id+"F1.imprint","IMPRINT",EDGE,{"derivedFrom":sQuery(id+"F1.wireOp",EDGE,"E8.0.7.2")}),1.0]])]});
            var Q153;
            Q153=makeQuery(id+"F1.imprint","IMPRINT",FACE,{"disambiguationData":[TD([[makeQuery(id+"F1.imprint","IMPRINT",EDGE,{"derivedFrom":sQuery(id+"F1.wireOp",EDGE,"E8.0.2.7")}),1.0]])]});
            var Q154;
            Q154=makeQuery(id+"F1.imprint","IMPRINT",FACE,{"disambiguationData":[TD([[makeQuery(id+"F1.imprint","IMPRINT",EDGE,{"derivedFrom":sQuery(id+"F1.wireOp",EDGE,"E8.0.7.10")}),1.0]])]});
            var Q155;
            Q155=makeQuery(id+"F1.imprint","IMPRINT",FACE,{"disambiguationData":[TD([[makeQuery(id+"F1.imprint","IMPRINT",EDGE,{"derivedFrom":sQuery(id+"F1.wireOp",EDGE,"E6.0.3.3")}),1.0]])]});
            var Q156;
            Q156=makeQuery(id+"F1.imprint","IMPRINT",FACE,{"disambiguationData":[TD([[makeQuery(id+"F1.imprint","IMPRINT",EDGE,{"derivedFrom":sQuery(id+"F1.wireOp",EDGE,"E6.0.3.2")}),1.0]])]});
            var Q157;
            Q157=makeQuery(id+"F1.imprint","IMPRINT",FACE,{"disambiguationData":[TD([[makeQuery(id+"F1.imprint","IMPRINT",EDGE,{"derivedFrom":sQuery(id+"F1.wireOp",EDGE,"E8.0.5.3")}),1.0]])]});
            var Q158;
            Q158=makeQuery(id+"F1.imprint","IMPRINT",FACE,{"disambiguationData":[TD([[makeQuery(id+"F1.imprint","IMPRINT",EDGE,{"derivedFrom":sQuery(id+"F1.wireOp",EDGE,"E6.0.1.6")}),1.0]])]});
            var Q159;
            Q159=makeQuery(id+"F1.imprint","IMPRINT",FACE,{"disambiguationData":[TD([[makeQuery(id+"F1.imprint","IMPRINT",EDGE,{"derivedFrom":sQuery(id+"F1.wireOp",EDGE,"E6.0.3.4")}),1.0]])]});
            var Q160;
            Q160=makeQuery(id+"F1.imprint","IMPRINT",FACE,{"disambiguationData":[TD([[makeQuery(id+"F1.imprint","IMPRINT",EDGE,{"derivedFrom":sQuery(id+"F1.wireOp",EDGE,"E5.0.3.0")}),1.0]])]});
            var Q161;
            Q161=makeQuery(id+"F1.imprint","IMPRINT",FACE,{"disambiguationData":[TD([[makeQuery(id+"F1.imprint","IMPRINT",EDGE,{"derivedFrom":sQuery(id+"F1.wireOp",EDGE,"E8.0.1.4")}),1.0]])]});
            var Q162;
            Q162=makeQuery(id+"F1.imprint","IMPRINT",FACE,{"disambiguationData":[TD([[makeQuery(id+"F1.imprint","IMPRINT",EDGE,{"derivedFrom":sQuery(id+"F1.wireOp",EDGE,"E6.0.4.2")}),1.0]])]});
            var Q163;
            Q163=makeQuery(id+"F1.imprint","IMPRINT",FACE,{"disambiguationData":[TD([[makeQuery(id+"F1.imprint","IMPRINT",EDGE,{"derivedFrom":sQuery(id+"F1.wireOp",EDGE,"E8.0.3.2")}),1.0]])]});
            var Q164;
            Q164=makeQuery(id+"F1.imprint","IMPRINT",FACE,{"disambiguationData":[TD([[makeQuery(id+"F1.imprint","IMPRINT",EDGE,{"derivedFrom":sQuery(id+"F1.wireOp",EDGE,"E8.0.5.7")}),1.0]])]});
            var Q165;
            Q165=makeQuery(id+"F1.imprint","IMPRINT",FACE,{"disambiguationData":[TD([[makeQuery(id+"F1.imprint","IMPRINT",EDGE,{"derivedFrom":sQuery(id+"F1.wireOp",EDGE,"E6.0.5.10")}),1.0]])]});
            var Q166;
            Q166=makeQuery(id+"F1.imprint","IMPRINT",FACE,{"disambiguationData":[TD([[makeQuery(id+"F1.imprint","IMPRINT",EDGE,{"derivedFrom":sQuery(id+"F1.wireOp",EDGE,"E6.0.7.9")}),1.0]])]});
            var Q167;
            Q167=makeQuery(id+"F1.imprint","IMPRINT",FACE,{"disambiguationData":[TD([[makeQuery(id+"F1.imprint","IMPRINT",EDGE,{"derivedFrom":sQuery(id+"F1.wireOp",EDGE,"E6.0.3.6")}),1.0]])]});
            var Q168;
            Q168=makeQuery(id+"F1.imprint","IMPRINT",FACE,{"disambiguationData":[TD([[makeQuery(id+"F1.imprint","IMPRINT",EDGE,{"derivedFrom":sQuery(id+"F1.wireOp",EDGE,"E6.0.4.4")}),1.0]])]});
            var Q169;
            Q169=makeQuery(id+"F1.imprint","IMPRINT",FACE,{"disambiguationData":[TD([[makeQuery(id+"F1.imprint","IMPRINT",EDGE,{"derivedFrom":sQuery(id+"F1.wireOp",EDGE,"E6.0.2.8")}),1.0]])]});
            var Q170;
            Q170=makeQuery(id+"F1.imprint","IMPRINT",FACE,{"disambiguationData":[TD([[makeQuery(id+"F1.imprint","IMPRINT",EDGE,{"derivedFrom":sQuery(id+"F1.wireOp",EDGE,"E6.0.5.2")}),1.0]])]});
            var Q171;
            Q171=makeQuery(id+"F1.imprint","IMPRINT",FACE,{"disambiguationData":[TD([[makeQuery(id+"F1.imprint","IMPRINT",EDGE,{"derivedFrom":sQuery(id+"F1.wireOp",EDGE,"E8.0.2.0")}),1.0]])]});
            var Q172;
            Q172=makeQuery(id+"F1.imprint","IMPRINT",FACE,{"disambiguationData":[TD([[makeQuery(id+"F1.imprint","IMPRINT",EDGE,{"derivedFrom":sQuery(id+"F1.wireOp",EDGE,"E6.0.8.10")}),1.0]])]});
            var Q173;
            Q173=makeQuery(id+"F1.imprint","IMPRINT",FACE,{"disambiguationData":[TD([[makeQuery(id+"F1.imprint","IMPRINT",EDGE,{"derivedFrom":sQuery(id+"F1.wireOp",EDGE,"E6.0.0.5")}),1.0]])]});
            var Q174;
            Q174=makeQuery(id+"F1.imprint","IMPRINT",FACE,{"disambiguationData":[TD([[makeQuery(id+"F1.imprint","IMPRINT",EDGE,{"derivedFrom":sQuery(id+"F1.wireOp",EDGE,"E8.0.3.9")}),1.0]])]});
            var Q175;
            Q175=makeQuery(id+"F1.imprint","IMPRINT",FACE,{"disambiguationData":[TD([[makeQuery(id+"F1.imprint","IMPRINT",EDGE,{"derivedFrom":sQuery(id+"F1.wireOp",EDGE,"E6.0.6.8")}),1.0]])]});
            var Q176;
            Q176=makeQuery(id+"F1.imprint","IMPRINT",FACE,{"disambiguationData":[TD([[makeQuery(id+"F1.imprint","IMPRINT",EDGE,{"derivedFrom":sQuery(id+"F1.wireOp",EDGE,"E8.0.7.7")}),1.0]])]});
            var Q177;
            Q177=makeQuery(id+"F1.imprint","IMPRINT",FACE,{"disambiguationData":[TD([[makeQuery(id+"F1.imprint","IMPRINT",EDGE,{"derivedFrom":sQuery(id+"F1.wireOp",EDGE,"E6.0.1.10")}),1.0]])]});
            var Q178;
            Q178=makeQuery(id+"F1.imprint","IMPRINT",FACE,{"disambiguationData":[TD([[makeQuery(id+"F1.imprint","IMPRINT",EDGE,{"derivedFrom":sQuery(id+"F1.wireOp",EDGE,"E6.0.6.11")}),1.0]])]});
            var Q179;
            Q179=makeQuery(id+"F1.imprint","IMPRINT",FACE,{"disambiguationData":[TD([[makeQuery(id+"F1.imprint","IMPRINT",EDGE,{"derivedFrom":sQuery(id+"F1.wireOp",EDGE,"E8.0.4.7")}),1.0]])]});
            var Q180;
            Q180=makeQuery(id+"F1.imprint","IMPRINT",FACE,{"disambiguationData":[TD([[makeQuery(id+"F1.imprint","IMPRINT",EDGE,{"derivedFrom":sQuery(id+"F1.wireOp",EDGE,"E6.0.1.9")}),1.0]])]});
            var Q181;
            Q181=makeQuery(id+"F1.imprint","IMPRINT",FACE,{"disambiguationData":[TD([[makeQuery(id+"F1.imprint","IMPRINT",EDGE,{"derivedFrom":sQuery(id+"F1.wireOp",EDGE,"E6.0.6.7")}),1.0]])]});
            var Q182;
            Q182=makeQuery(id+"F1.imprint","IMPRINT",FACE,{"disambiguationData":[TD([[makeQuery(id+"F1.imprint","IMPRINT",EDGE,{"derivedFrom":sQuery(id+"F1.wireOp",EDGE,"E8.0.3.6")}),1.0]])]});
            var Q183;
            Q183=makeQuery(id+"F1.imprint","IMPRINT",FACE,{"disambiguationData":[TD([[makeQuery(id+"F1.imprint","IMPRINT",EDGE,{"derivedFrom":sQuery(id+"F1.wireOp",EDGE,"E6.0.8.4")}),1.0]])]});
            var Q184;
            Q184=makeQuery(id+"F1.imprint","IMPRINT",FACE,{"disambiguationData":[TD([[makeQuery(id+"F1.imprint","IMPRINT",EDGE,{"derivedFrom":sQuery(id+"F1.wireOp",EDGE,"E8.0.7.1")}),1.0]])]});
            var Q185;
            Q185=makeQuery(id+"F1.imprint","IMPRINT",FACE,{"disambiguationData":[TD([[makeQuery(id+"F1.imprint","IMPRINT",EDGE,{"derivedFrom":sQuery(id+"F1.wireOp",EDGE,"E5.0.2.0")}),1.0]])]});
            var Q186;
            Q186=makeQuery(id+"F1.imprint","IMPRINT",FACE,{"disambiguationData":[TD([[makeQuery(id+"F1.imprint","IMPRINT",EDGE,{"derivedFrom":sQuery(id+"F1.wireOp",EDGE,"E5.0.7.0")}),1.0]])]});
            var Q187;
            Q187=makeQuery(id+"F1.imprint","IMPRINT",FACE,{"disambiguationData":[TD([[makeQuery(id+"F1.imprint","IMPRINT",EDGE,{"derivedFrom":sQuery(id+"F1.wireOp",EDGE,"E5.0.1.0")}),1.0]])]});
            var Q188;
            Q188=makeQuery(id+"F1.imprint","IMPRINT",FACE,{"disambiguationData":[TD([[makeQuery(id+"F1.imprint","IMPRINT",EDGE,{"derivedFrom":sQuery(id+"F1.wireOp",EDGE,"E6.0.8.11")}),1.0]])]});
            var Q189;
            Q189=makeQuery(id+"F1.imprint","IMPRINT",FACE,{"disambiguationData":[TD([[makeQuery(id+"F1.imprint","IMPRINT",EDGE,{"derivedFrom":sQuery(id+"F1.wireOp",EDGE,"E6.0.0.11")}),1.0]])]});
            var Q190;
            Q190=makeQuery(id+"F1.imprint","IMPRINT",FACE,{"disambiguationData":[TD([[makeQuery(id+"F1.imprint","IMPRINT",EDGE,{"derivedFrom":sQuery(id+"F1.wireOp",EDGE,"E5.0.8.0")}),1.0]])]});
            var Q191;
            Q191=makeQuery(id+"F1.imprint","IMPRINT",FACE,{"disambiguationData":[TD([[makeQuery(id+"F1.imprint","IMPRINT",EDGE,{"derivedFrom":sQuery(id+"F1.wireOp",EDGE,"E6.0.0.3")}),1.0]])]});
            var Q192;
            Q192=makeQuery(id+"F1.imprint","IMPRINT",FACE,{"disambiguationData":[TD([[makeQuery(id+"F1.imprint","IMPRINT",EDGE,{"derivedFrom":sQuery(id+"F1.wireOp",EDGE,"E5.0.4.0")}),1.0]])]});
            var Q193;
            Q193=makeQuery(id+"F1.imprint","IMPRINT",FACE,{"disambiguationData":[TD([[makeQuery(id+"F1.imprint","IMPRINT",EDGE,{"derivedFrom":sQuery(id+"F1.wireOp",EDGE,"E8.0.2.5")}),1.0]])]});
            var Q194;
            Q194=makeQuery(id+"F1.imprint","IMPRINT",FACE,{"disambiguationData":[TD([[makeQuery(id+"F1.imprint","IMPRINT",EDGE,{"derivedFrom":sQuery(id+"F1.wireOp",EDGE,"E6.0.5.4")}),1.0]])]});
            var Q195;
            Q195=makeQuery(id+"F1.imprint","IMPRINT",FACE,{"disambiguationData":[TD([[makeQuery(id+"F1.imprint","IMPRINT",EDGE,{"derivedFrom":sQuery(id+"F1.wireOp",EDGE,"E1.bottom")}),1.0]])]});
            var Q196;
            Q196=makeQuery(id+"F1.imprint","IMPRINT",FACE,{"disambiguationData":[TD([[makeQuery(id+"F1.imprint","IMPRINT",EDGE,{"derivedFrom":sQuery(id+"F1.wireOp",EDGE,"E1.bottom")}),1.0]])]});
            extrude(context, id + "F5", {"entities" : qUnion([Q0, Q1, Q2, Q3, Q4, Q5, Q6, Q7, Q8, Q9, Q10, Q11, Q12, Q13, Q14, Q15, Q16, Q17, Q18, Q19, Q20, Q21, Q22, Q23, Q24, Q25, Q26, Q27, Q28, Q29, Q30, Q31, Q32, Q33, Q34, Q35, Q36, Q37, Q38, Q39, Q40, Q41, Q42, Q43, Q44, Q45, Q46, Q47, Q48, Q49, Q50, Q51, Q52, Q53, Q54, Q55, Q56, Q57, Q58, Q59, Q60, Q61, Q62, Q63, Q64, Q65, Q66, Q67, Q68, Q69, Q70, Q71, Q72, Q73, Q74, Q75, Q76, Q77, Q78, Q79, Q80, Q81, Q82, Q83, Q84, Q85, Q86, Q87, Q88, Q89, Q90, Q91, Q92, Q93, Q94, Q95, Q96, Q97, Q98, Q99, Q100, Q101, Q102, Q103, Q104, Q105, Q106, Q107, Q108, Q109, Q110, Q111, Q112, Q113, Q114, Q115, Q116, Q117, Q118, Q119, Q120, Q121, Q122, Q123, Q124, Q125, Q126, Q127, Q128, Q129, Q130, Q131, Q132, Q133, Q134, Q135, Q136, Q137, Q138, Q139, Q140, Q141, Q142, Q143, Q144, Q145, Q146, Q147, Q148, Q149, Q150, Q151, Q152, Q153, Q154, Q155, Q156, Q157, Q158, Q159, Q160, Q161, Q162, Q163, Q164, Q165, Q166, Q167, Q168, Q169, Q170, Q171, Q172, Q173, Q174, Q175, Q176, Q177, Q178, Q179, Q180, Q181, Q182, Q183, Q184, Q185, Q186, Q187, Q188, Q189, Q190, Q191, Q192, Q193, Q194, Q195, Q196]), "depth" : 3 * mm, "offsetDistance" : 25 * mm});
        }
        {
            var Q0;
            Q0=makeQuery(id+"F3.imprint","IMPRINT",FACE,{"disambiguationData":[TD([[makeQuery(id+"F3.imprint","IMPRINT",EDGE,{"derivedFrom":sQuery(id+"F3.wireOp",EDGE,"E21")}),-1.0]])]});
            extrude(context, id + "F6", {"entities" : qUnion([Q0]), "depth" : 3 * mm, "offsetDistance" : 25 * mm});
        }
    });
